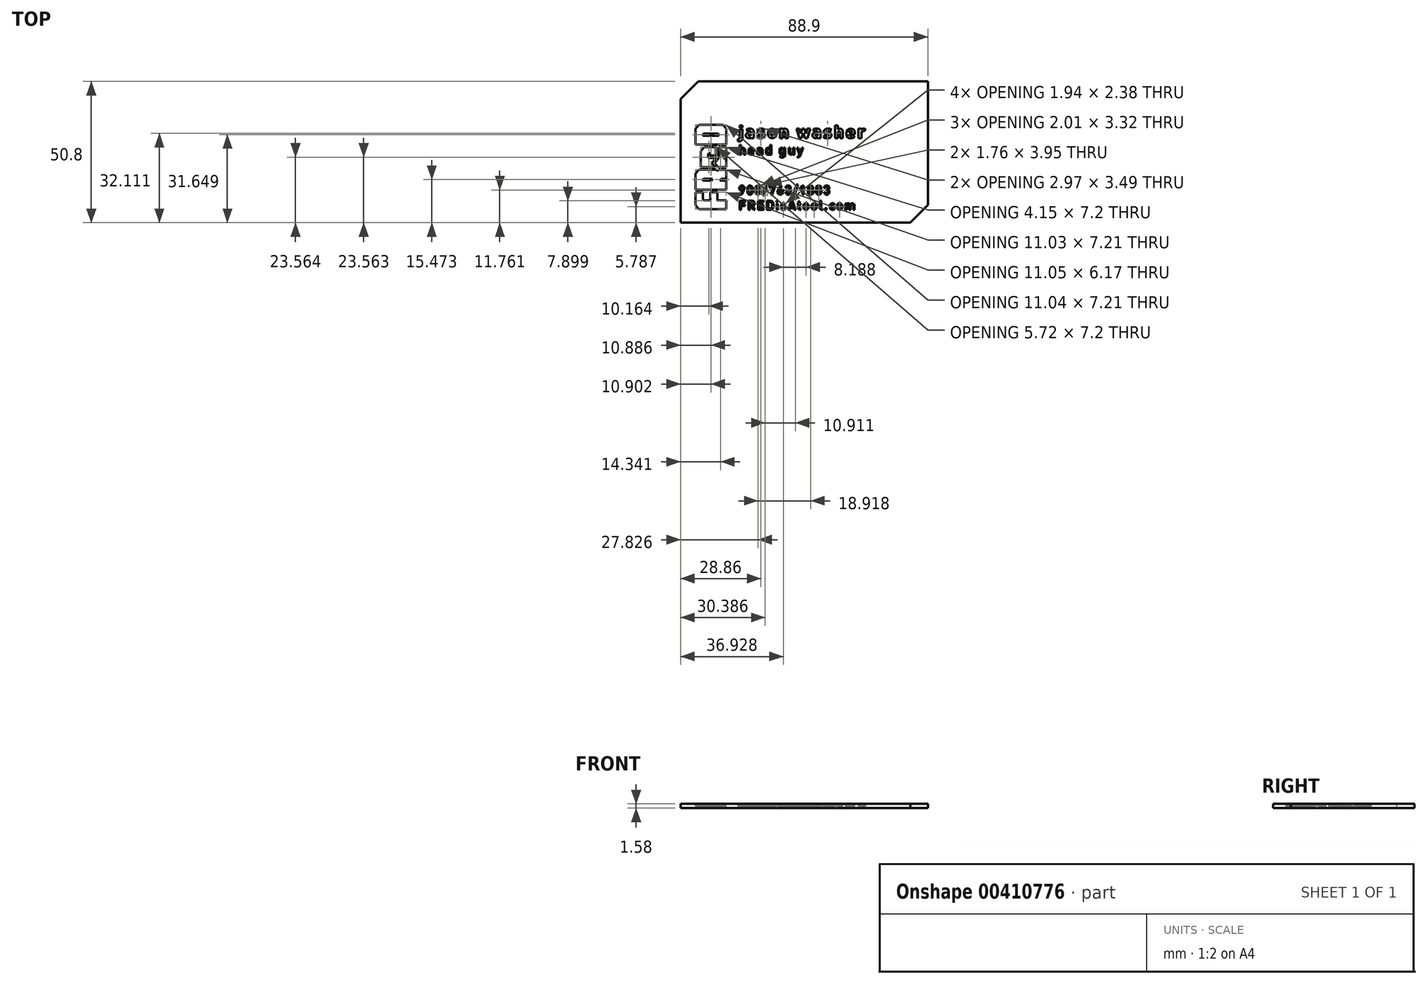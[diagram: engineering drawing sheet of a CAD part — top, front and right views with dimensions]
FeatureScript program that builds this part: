
annotation { "Feature Type Name" : "Feature", "Feature Type Description" : "" }
export const myFeature = defineFeature(function(context is Context, id is Id, definition is map)
    precondition{}
    {
        {
            var Q0;
            Q0=qCreatedBy(makeId("Top.planeOp"),FACE);
            var sketch = newSketch(context, id + "F0", { "sketchPlane" : qUnion([Q0])});
            skLineSegment(sketch, "E0", {"start": v(-19.03, 1.16) * mm, "end": v(-19.15, 1.16) * mm});
            skLineSegment(sketch, "E1", {"start": v(-19.15, 1.16) * mm, "end": v(-19.5, 0.9) * mm});
            skLineSegment(sketch, "E2", {"start": v(-19.5, 0.9) * mm, "end": v(-19.53, 0.84) * mm});
            skLineSegment(sketch, "E3", {"start": v(-19.53, 0.84) * mm, "end": v(-19.54, 0.82) * mm});
            skLineSegment(sketch, "E4", {"start": v(-19.54, 0.82) * mm, "end": v(-19.6, 0.54) * mm});
            skLineSegment(sketch, "E5", {"start": v(-19.6, 0.54) * mm, "end": v(-19.6, 0.5) * mm});
            skLineSegment(sketch, "E6", {"start": v(-19.6, 0.5) * mm, "end": v(-18.46, 0.5) * mm});
            skLineSegment(sketch, "E7", {"start": v(-18.46, 0.5) * mm, "end": v(-18.47, 0.54) * mm});
            skLineSegment(sketch, "E8", {"start": v(-18.47, 0.54) * mm, "end": v(-18.52, 0.82) * mm});
            skLineSegment(sketch, "E9", {"start": v(-18.52, 0.82) * mm, "end": v(-18.53, 0.84) * mm});
            skLineSegment(sketch, "E10", {"start": v(-18.53, 0.84) * mm, "end": v(-18.56, 0.9) * mm});
            skLineSegment(sketch, "E11", {"start": v(-18.56, 0.9) * mm, "end": v(-18.91, 1.16) * mm});
            skLineSegment(sketch, "E12", {"start": v(-18.91, 1.16) * mm, "end": v(-19.03, 1.16) * mm});
            skLineSegment(sketch, "E13", {"start": v(16.69, 7.6) * mm, "end": v(16.58, 7.6) * mm});
            skLineSegment(sketch, "E14", {"start": v(16.58, 7.6) * mm, "end": v(16.25, 7.37) * mm});
            skLineSegment(sketch, "E15", {"start": v(16.25, 7.37) * mm, "end": v(16.24, 7.33) * mm});
            skLineSegment(sketch, "E16", {"start": v(16.24, 7.33) * mm, "end": v(16.23, 7.31) * mm});
            skLineSegment(sketch, "E17", {"start": v(16.23, 7.31) * mm, "end": v(16.18, 7.13) * mm});
            skLineSegment(sketch, "E18", {"start": v(16.18, 7.13) * mm, "end": v(16.18, 7.07) * mm});
            skLineSegment(sketch, "E19", {"start": v(16.18, 7.07) * mm, "end": v(17.2, 7.07) * mm});
            skLineSegment(sketch, "E20", {"start": v(17.2, 7.07) * mm, "end": v(17.2, 7.13) * mm});
            skLineSegment(sketch, "E21", {"start": v(17.2, 7.13) * mm, "end": v(17.15, 7.31) * mm});
            skLineSegment(sketch, "E22", {"start": v(17.15, 7.31) * mm, "end": v(17.14, 7.33) * mm});
            skLineSegment(sketch, "E23", {"start": v(17.14, 7.33) * mm, "end": v(17.12, 7.37) * mm});
            skLineSegment(sketch, "E24", {"start": v(17.12, 7.37) * mm, "end": v(16.8, 7.6) * mm});
            skLineSegment(sketch, "E25", {"start": v(16.8, 7.6) * mm, "end": v(16.69, 7.6) * mm});
            skLineSegment(sketch, "E26", {"start": v(3.94, 6.1) * mm, "end": v(3.94, 6.05) * mm});
            skLineSegment(sketch, "E27", {"start": v(3.94, 6.05) * mm, "end": v(4.02, 5.9) * mm});
            skLineSegment(sketch, "E28", {"start": v(4.02, 5.9) * mm, "end": v(4.22, 5.82) * mm});
            skLineSegment(sketch, "E29", {"start": v(4.22, 5.82) * mm, "end": v(4.28, 5.82) * mm});
            skLineSegment(sketch, "E30", {"start": v(4.28, 5.82) * mm, "end": v(4.39, 5.82) * mm});
            skLineSegment(sketch, "E31", {"start": v(4.39, 5.82) * mm, "end": v(4.67, 5.92) * mm});
            skLineSegment(sketch, "E32", {"start": v(4.67, 5.92) * mm, "end": v(4.7, 5.94) * mm});
            skLineSegment(sketch, "E33", {"start": v(4.7, 5.94) * mm, "end": v(4.71, 5.96) * mm});
            skLineSegment(sketch, "E34", {"start": v(4.71, 5.96) * mm, "end": v(4.8, 6.2) * mm});
            skLineSegment(sketch, "E35", {"start": v(4.8, 6.2) * mm, "end": v(4.8, 6.29) * mm});
            skLineSegment(sketch, "E36", {"start": v(4.8, 6.29) * mm, "end": v(4.8, 6.37) * mm});
            skLineSegment(sketch, "E37", {"start": v(4.8, 6.37) * mm, "end": v(4.27, 6.37) * mm});
            skLineSegment(sketch, "E38", {"start": v(4.27, 6.37) * mm, "end": v(4.2, 6.37) * mm});
            skLineSegment(sketch, "E39", {"start": v(4.2, 6.37) * mm, "end": v(4.03, 6.3) * mm});
            skLineSegment(sketch, "E40", {"start": v(4.03, 6.3) * mm, "end": v(3.94, 6.15) * mm});
            skLineSegment(sketch, "E41", {"start": v(3.94, 6.15) * mm, "end": v(3.94, 6.1) * mm});
            skLineSegment(sketch, "E42", {"start": v(-12.79, -0.53) * mm, "end": v(-12.68, -0.53) * mm});
            skLineSegment(sketch, "E43", {"start": v(-12.68, -0.53) * mm, "end": v(-12.36, -0.28) * mm});
            skLineSegment(sketch, "E44", {"start": v(-12.36, -0.28) * mm, "end": v(-12.27, 0.16) * mm});
            skLineSegment(sketch, "E45", {"start": v(-12.27, 0.16) * mm, "end": v(-12.27, 0.3) * mm});
            skLineSegment(sketch, "E46", {"start": v(-12.27, 0.3) * mm, "end": v(-12.27, 0.45) * mm});
            skLineSegment(sketch, "E47", {"start": v(-12.27, 0.45) * mm, "end": v(-12.36, 0.88) * mm});
            skLineSegment(sketch, "E48", {"start": v(-12.36, 0.88) * mm, "end": v(-12.68, 1.13) * mm});
            skLineSegment(sketch, "E49", {"start": v(-12.68, 1.13) * mm, "end": v(-12.79, 1.13) * mm});
            skLineSegment(sketch, "E50", {"start": v(-12.79, 1.13) * mm, "end": v(-12.9, 1.13) * mm});
            skLineSegment(sketch, "E51", {"start": v(-12.9, 1.13) * mm, "end": v(-13.22, 0.88) * mm});
            skLineSegment(sketch, "E52", {"start": v(-13.22, 0.88) * mm, "end": v(-13.3, 0.45) * mm});
            skLineSegment(sketch, "E53", {"start": v(-13.3, 0.45) * mm, "end": v(-13.3, 0.3) * mm});
            skLineSegment(sketch, "E54", {"start": v(-13.3, 0.3) * mm, "end": v(-13.3, 0.16) * mm});
            skLineSegment(sketch, "E55", {"start": v(-13.3, 0.16) * mm, "end": v(-13.22, -0.28) * mm});
            skLineSegment(sketch, "E56", {"start": v(-13.22, -0.28) * mm, "end": v(-12.9, -0.53) * mm});
            skLineSegment(sketch, "E57", {"start": v(-12.9, -0.53) * mm, "end": v(-12.79, -0.53) * mm});
            skLineSegment(sketch, "E58", {"start": v(-38.1, 25.4) * mm, "end": v(-44.45, 19.05) * mm});
            skLineSegment(sketch, "E59", {"start": v(-44.45, 19.05) * mm, "end": v(-44.45, -25.4) * mm});
            skLineSegment(sketch, "E60", {"start": v(-44.45, -25.4) * mm, "end": v(38.1, -25.4) * mm});
            skLineSegment(sketch, "E61", {"start": v(38.1, -25.4) * mm, "end": v(44.45, -19.05) * mm});
            skLineSegment(sketch, "E62", {"start": v(44.45, -19.05) * mm, "end": v(44.45, 25.4) * mm});
            skLineSegment(sketch, "E63", {"start": v(44.45, 25.4) * mm, "end": v(-38.1, 25.4) * mm});
            skLineSegment(sketch, "E64", {"start": v(4.28, 7.58) * mm, "end": v(4.2, 7.58) * mm});
            skLineSegment(sketch, "E65", {"start": v(4.2, 7.58) * mm, "end": v(3.97, 7.53) * mm});
            skLineSegment(sketch, "E66", {"start": v(3.97, 7.53) * mm, "end": v(3.78, 7.4) * mm});
            skLineSegment(sketch, "E67", {"start": v(3.78, 7.4) * mm, "end": v(3.74, 7.35) * mm});
            skLineSegment(sketch, "E68", {"start": v(3.74, 7.35) * mm, "end": v(3.09, 8) * mm});
            skLineSegment(sketch, "E69", {"start": v(3.09, 8) * mm, "end": v(3.17, 8.09) * mm});
            skLineSegment(sketch, "E70", {"start": v(3.17, 8.09) * mm, "end": v(3.62, 8.36) * mm});
            skLineSegment(sketch, "E71", {"start": v(3.62, 8.36) * mm, "end": v(4.15, 8.46) * mm});
            skLineSegment(sketch, "E72", {"start": v(4.15, 8.46) * mm, "end": v(4.33, 8.46) * mm});
            skLineSegment(sketch, "E73", {"start": v(4.33, 8.46) * mm, "end": v(4.5, 8.46) * mm});
            skLineSegment(sketch, "E74", {"start": v(4.5, 8.46) * mm, "end": v(4.98, 8.38) * mm});
            skLineSegment(sketch, "E75", {"start": v(4.98, 8.38) * mm, "end": v(5.45, 8.15) * mm});
            skLineSegment(sketch, "E76", {"start": v(5.45, 8.15) * mm, "end": v(5.74, 7.76) * mm});
            skLineSegment(sketch, "E77", {"start": v(5.74, 7.76) * mm, "end": v(5.84, 7.35) * mm});
            skLineSegment(sketch, "E78", {"start": v(5.84, 7.35) * mm, "end": v(5.84, 7.22) * mm});
            skLineSegment(sketch, "E79", {"start": v(5.84, 7.22) * mm, "end": v(5.84, 5) * mm});
            skLineSegment(sketch, "E80", {"start": v(5.84, 5) * mm, "end": v(4.82, 5) * mm});
            skLineSegment(sketch, "E81", {"start": v(4.82, 5) * mm, "end": v(4.82, 5.28) * mm});
            skLineSegment(sketch, "E82", {"start": v(4.82, 5.28) * mm, "end": v(4.77, 5.23) * mm});
            skLineSegment(sketch, "E83", {"start": v(4.77, 5.23) * mm, "end": v(4.5, 5.05) * mm});
            skLineSegment(sketch, "E84", {"start": v(4.5, 5.05) * mm, "end": v(4.17, 4.97) * mm});
            skLineSegment(sketch, "E85", {"start": v(4.17, 4.97) * mm, "end": v(4.06, 4.97) * mm});
            skLineSegment(sketch, "E86", {"start": v(4.06, 4.97) * mm, "end": v(3.85, 4.97) * mm});
            skLineSegment(sketch, "E87", {"start": v(3.85, 4.97) * mm, "end": v(3.29, 5.23) * mm});
            skLineSegment(sketch, "E88", {"start": v(3.29, 5.23) * mm, "end": v(3.24, 5.28) * mm});
            skLineSegment(sketch, "E89", {"start": v(3.24, 5.28) * mm, "end": v(3.2, 5.32) * mm});
            skLineSegment(sketch, "E90", {"start": v(3.2, 5.32) * mm, "end": v(2.94, 5.89) * mm});
            skLineSegment(sketch, "E91", {"start": v(2.94, 5.89) * mm, "end": v(2.94, 6.08) * mm});
            skLineSegment(sketch, "E92", {"start": v(2.94, 6.08) * mm, "end": v(2.94, 6.17) * mm});
            skLineSegment(sketch, "E93", {"start": v(2.94, 6.17) * mm, "end": v(3, 6.45) * mm});
            skLineSegment(sketch, "E94", {"start": v(3, 6.45) * mm, "end": v(3.22, 6.76) * mm});
            skLineSegment(sketch, "E95", {"start": v(3.22, 6.76) * mm, "end": v(3.58, 6.99) * mm});
            skLineSegment(sketch, "E96", {"start": v(3.58, 6.99) * mm, "end": v(3.97, 7.07) * mm});
            skLineSegment(sketch, "E97", {"start": v(3.97, 7.07) * mm, "end": v(4.1, 7.07) * mm});
            skLineSegment(sketch, "E98", {"start": v(4.1, 7.07) * mm, "end": v(4.8, 7.07) * mm});
            skLineSegment(sketch, "E99", {"start": v(4.8, 7.07) * mm, "end": v(4.8, 7.15) * mm});
            skLineSegment(sketch, "E100", {"start": v(4.8, 7.15) * mm, "end": v(4.8, 7.24) * mm});
            skLineSegment(sketch, "E101", {"start": v(4.8, 7.24) * mm, "end": v(4.67, 7.49) * mm});
            skLineSegment(sketch, "E102", {"start": v(4.67, 7.49) * mm, "end": v(4.38, 7.58) * mm});
            skLineSegment(sketch, "E103", {"start": v(4.38, 7.58) * mm, "end": v(4.28, 7.58) * mm});
            skLineSegment(sketch, "E104", {"start": v(-1.72, 8.42) * mm, "end": v(-1.3, 6.65) * mm});
            skLineSegment(sketch, "E105", {"start": v(-1.3, 6.65) * mm, "end": v(-0.7, 8.42) * mm});
            skLineSegment(sketch, "E106", {"start": v(-0.7, 8.42) * mm, "end": v(0.02, 8.42) * mm});
            skLineSegment(sketch, "E107", {"start": v(0.02, 8.42) * mm, "end": v(0.61, 6.65) * mm});
            skLineSegment(sketch, "E108", {"start": v(0.61, 6.65) * mm, "end": v(1.04, 8.42) * mm});
            skLineSegment(sketch, "E109", {"start": v(1.04, 8.42) * mm, "end": v(2.14, 8.42) * mm});
            skLineSegment(sketch, "E110", {"start": v(2.14, 8.42) * mm, "end": v(1.1, 5) * mm});
            skLineSegment(sketch, "E111", {"start": v(1.1, 5) * mm, "end": v(0.28, 5) * mm});
            skLineSegment(sketch, "E112", {"start": v(0.28, 5) * mm, "end": v(-0.34, 6.88) * mm});
            skLineSegment(sketch, "E113", {"start": v(-0.34, 6.88) * mm, "end": v(-0.96, 5) * mm});
            skLineSegment(sketch, "E114", {"start": v(-0.96, 5) * mm, "end": v(-1.79, 5) * mm});
            skLineSegment(sketch, "E115", {"start": v(-1.79, 5) * mm, "end": v(-2.82, 8.42) * mm});
            skLineSegment(sketch, "E116", {"start": v(-2.82, 8.42) * mm, "end": v(-1.72, 8.42) * mm});
            skLineSegment(sketch, "E117", {"start": v(-2.4, -1.95) * mm, "end": v(-2.4, -1.5) * mm});
            skLineSegment(sketch, "E118", {"start": v(-2.4, -1.5) * mm, "end": v(-2.27, -1.5) * mm});
            skLineSegment(sketch, "E119", {"start": v(-2.27, -1.5) * mm, "end": v(-2.21, -1.5) * mm});
            skLineSegment(sketch, "E120", {"start": v(-2.21, -1.5) * mm, "end": v(-2.04, -1.43) * mm});
            skLineSegment(sketch, "E121", {"start": v(-2.04, -1.43) * mm, "end": v(-1.93, -1.27) * mm});
            skLineSegment(sketch, "E122", {"start": v(-1.93, -1.27) * mm, "end": v(-1.9, -1.23) * mm});
            skLineSegment(sketch, "E123", {"start": v(-1.9, -1.23) * mm, "end": v(-1.77, -0.84) * mm});
            skLineSegment(sketch, "E124", {"start": v(-1.77, -0.84) * mm, "end": v(-2.65, 1.55) * mm});
            skLineSegment(sketch, "E125", {"start": v(-2.65, 1.55) * mm, "end": v(-2.11, 1.55) * mm});
            skLineSegment(sketch, "E126", {"start": v(-2.11, 1.55) * mm, "end": v(-1.52, -0.21) * mm});
            skLineSegment(sketch, "E127", {"start": v(-1.52, -0.21) * mm, "end": v(-0.93, 1.55) * mm});
            skLineSegment(sketch, "E128", {"start": v(-0.93, 1.55) * mm, "end": v(-0.4, 1.55) * mm});
            skLineSegment(sketch, "E129", {"start": v(-0.4, 1.55) * mm, "end": v(-1.5, -1.45) * mm});
            skLineSegment(sketch, "E130", {"start": v(-1.5, -1.45) * mm, "end": v(-1.51, -1.49) * mm});
            skLineSegment(sketch, "E131", {"start": v(-1.51, -1.49) * mm, "end": v(-1.66, -1.74) * mm});
            skLineSegment(sketch, "E132", {"start": v(-1.66, -1.74) * mm, "end": v(-1.68, -1.76) * mm});
            skLineSegment(sketch, "E133", {"start": v(-1.68, -1.76) * mm, "end": v(-1.72, -1.8) * mm});
            skLineSegment(sketch, "E134", {"start": v(-1.72, -1.8) * mm, "end": v(-2.08, -1.95) * mm});
            skLineSegment(sketch, "E135", {"start": v(-2.08, -1.95) * mm, "end": v(-2.2, -1.95) * mm});
            skLineSegment(sketch, "E136", {"start": v(-2.2, -1.95) * mm, "end": v(-2.4, -1.95) * mm});
            skLineSegment(sketch, "E137", {"start": v(-2.27, -11.67) * mm, "end": v(-3.58, -15.61) * mm});
            skLineSegment(sketch, "E138", {"start": v(-3.58, -15.61) * mm, "end": v(-4.03, -15.61) * mm});
            skLineSegment(sketch, "E139", {"start": v(-4.03, -15.61) * mm, "end": v(-2.73, -11.67) * mm});
            skLineSegment(sketch, "E140", {"start": v(-2.73, -11.67) * mm, "end": v(-2.27, -11.67) * mm});
            skLineSegment(sketch, "E141", {"start": v(-5.6, 1.55) * mm, "end": v(-5.1, 1.55) * mm});
            skLineSegment(sketch, "E142", {"start": v(-5.1, 1.55) * mm, "end": v(-5.1, 0.02) * mm});
            skLineSegment(sketch, "E143", {"start": v(-5.1, 0.02) * mm, "end": v(-5.1, -0.08) * mm});
            skLineSegment(sketch, "E144", {"start": v(-5.1, -0.08) * mm, "end": v(-4.96, -0.4) * mm});
            skLineSegment(sketch, "E145", {"start": v(-4.96, -0.4) * mm, "end": v(-4.7, -0.53) * mm});
            skLineSegment(sketch, "E146", {"start": v(-4.7, -0.53) * mm, "end": v(-4.6, -0.53) * mm});
            skLineSegment(sketch, "E147", {"start": v(-4.6, -0.53) * mm, "end": v(-4.51, -0.53) * mm});
            skLineSegment(sketch, "E148", {"start": v(-4.51, -0.53) * mm, "end": v(-4.24, -0.4) * mm});
            skLineSegment(sketch, "E149", {"start": v(-4.24, -0.4) * mm, "end": v(-4.08, -0.08) * mm});
            skLineSegment(sketch, "E150", {"start": v(-4.08, -0.08) * mm, "end": v(-4.08, 0.02) * mm});
            skLineSegment(sketch, "E151", {"start": v(-4.08, 0.02) * mm, "end": v(-4.08, 1.55) * mm});
            skLineSegment(sketch, "E152", {"start": v(-4.08, 1.55) * mm, "end": v(-3.58, 1.55) * mm});
            skLineSegment(sketch, "E153", {"start": v(-3.58, 1.55) * mm, "end": v(-3.58, -0.95) * mm});
            skLineSegment(sketch, "E154", {"start": v(-3.58, -0.95) * mm, "end": v(-4.07, -0.95) * mm});
            skLineSegment(sketch, "E155", {"start": v(-4.07, -0.95) * mm, "end": v(-4.07, -0.7) * mm});
            skLineSegment(sketch, "E156", {"start": v(-4.07, -0.7) * mm, "end": v(-4.12, -0.75) * mm});
            skLineSegment(sketch, "E157", {"start": v(-4.12, -0.75) * mm, "end": v(-4.58, -0.98) * mm});
            skLineSegment(sketch, "E158", {"start": v(-4.58, -0.98) * mm, "end": v(-4.74, -0.98) * mm});
            skLineSegment(sketch, "E159", {"start": v(-4.74, -0.98) * mm, "end": v(-4.9, -0.98) * mm});
            skLineSegment(sketch, "E160", {"start": v(-4.9, -0.98) * mm, "end": v(-5.32, -0.8) * mm});
            skLineSegment(sketch, "E161", {"start": v(-5.32, -0.8) * mm, "end": v(-5.36, -0.76) * mm});
            skLineSegment(sketch, "E162", {"start": v(-5.36, -0.76) * mm, "end": v(-5.4, -0.7) * mm});
            skLineSegment(sketch, "E163", {"start": v(-5.4, -0.7) * mm, "end": v(-5.6, -0.21) * mm});
            skLineSegment(sketch, "E164", {"start": v(-5.6, -0.21) * mm, "end": v(-5.6, -0.05) * mm});
            skLineSegment(sketch, "E165", {"start": v(-5.6, -0.05) * mm, "end": v(-5.6, 1.55) * mm});
            skLineSegment(sketch, "E166", {"start": v(-8.78, 8.42) * mm, "end": v(-7.76, 8.42) * mm});
            skLineSegment(sketch, "E167", {"start": v(-7.76, 8.42) * mm, "end": v(-7.76, 8.14) * mm});
            skLineSegment(sketch, "E168", {"start": v(-7.76, 8.14) * mm, "end": v(-7.71, 8.2) * mm});
            skLineSegment(sketch, "E169", {"start": v(-7.71, 8.2) * mm, "end": v(-7.16, 8.46) * mm});
            skLineSegment(sketch, "E170", {"start": v(-7.16, 8.46) * mm, "end": v(-6.97, 8.46) * mm});
            skLineSegment(sketch, "E171", {"start": v(-6.97, 8.46) * mm, "end": v(-6.78, 8.46) * mm});
            skLineSegment(sketch, "E172", {"start": v(-6.78, 8.46) * mm, "end": v(-6.25, 8.21) * mm});
            skLineSegment(sketch, "E173", {"start": v(-6.25, 8.21) * mm, "end": v(-6.2, 8.17) * mm});
            skLineSegment(sketch, "E174", {"start": v(-6.2, 8.17) * mm, "end": v(-6.13, 8.1) * mm});
            skLineSegment(sketch, "E175", {"start": v(-6.13, 8.1) * mm, "end": v(-5.92, 7.7) * mm});
            skLineSegment(sketch, "E176", {"start": v(-5.92, 7.7) * mm, "end": v(-5.86, 7.32) * mm});
            skLineSegment(sketch, "E177", {"start": v(-5.86, 7.32) * mm, "end": v(-5.86, 7.19) * mm});
            skLineSegment(sketch, "E178", {"start": v(-5.86, 7.19) * mm, "end": v(-5.86, 5) * mm});
            skLineSegment(sketch, "E179", {"start": v(-5.86, 5) * mm, "end": v(-6.9, 5) * mm});
            skLineSegment(sketch, "E180", {"start": v(-6.9, 5) * mm, "end": v(-6.9, 7.05) * mm});
            skLineSegment(sketch, "E181", {"start": v(-6.9, 7.05) * mm, "end": v(-6.9, 7.14) * mm});
            skLineSegment(sketch, "E182", {"start": v(-6.9, 7.14) * mm, "end": v(-7.06, 7.43) * mm});
            skLineSegment(sketch, "E183", {"start": v(-7.06, 7.43) * mm, "end": v(-7.25, 7.52) * mm});
            skLineSegment(sketch, "E184", {"start": v(-7.25, 7.52) * mm, "end": v(-7.32, 7.52) * mm});
            skLineSegment(sketch, "E185", {"start": v(-7.32, 7.52) * mm, "end": v(-7.39, 7.52) * mm});
            skLineSegment(sketch, "E186", {"start": v(-7.39, 7.52) * mm, "end": v(-7.58, 7.43) * mm});
            skLineSegment(sketch, "E187", {"start": v(-7.58, 7.43) * mm, "end": v(-7.74, 7.14) * mm});
            skLineSegment(sketch, "E188", {"start": v(-7.74, 7.14) * mm, "end": v(-7.74, 7.05) * mm});
            skLineSegment(sketch, "E189", {"start": v(-7.74, 7.05) * mm, "end": v(-7.74, 5) * mm});
            skLineSegment(sketch, "E190", {"start": v(-7.74, 5) * mm, "end": v(-8.78, 5) * mm});
            skLineSegment(sketch, "E191", {"start": v(-8.78, 5) * mm, "end": v(-8.78, 8.42) * mm});
            skLineSegment(sketch, "E192", {"start": v(-8.63, 1.36) * mm, "end": v(-8.6, 1.4) * mm});
            skLineSegment(sketch, "E193", {"start": v(-8.6, 1.4) * mm, "end": v(-8.17, 1.58) * mm});
            skLineSegment(sketch, "E194", {"start": v(-8.17, 1.58) * mm, "end": v(-8.02, 1.58) * mm});
            skLineSegment(sketch, "E195", {"start": v(-8.02, 1.58) * mm, "end": v(-7.86, 1.58) * mm});
            skLineSegment(sketch, "E196", {"start": v(-7.86, 1.58) * mm, "end": v(-7.41, 1.34) * mm});
            skLineSegment(sketch, "E197", {"start": v(-7.41, 1.34) * mm, "end": v(-7.37, 1.29) * mm});
            skLineSegment(sketch, "E198", {"start": v(-7.37, 1.29) * mm, "end": v(-7.37, 1.55) * mm});
            skLineSegment(sketch, "E199", {"start": v(-7.37, 1.55) * mm, "end": v(-6.88, 1.55) * mm});
            skLineSegment(sketch, "E200", {"start": v(-6.88, 1.55) * mm, "end": v(-6.88, -0.94) * mm});
            skLineSegment(sketch, "E201", {"start": v(-6.88, -0.94) * mm, "end": v(-6.88, -1.13) * mm});
            skLineSegment(sketch, "E202", {"start": v(-6.88, -1.13) * mm, "end": v(-7.16, -1.7) * mm});
            skLineSegment(sketch, "E203", {"start": v(-7.16, -1.7) * mm, "end": v(-7.75, -2) * mm});
            skLineSegment(sketch, "E204", {"start": v(-7.75, -2) * mm, "end": v(-7.95, -2) * mm});
            skLineSegment(sketch, "E205", {"start": v(-7.95, -2) * mm, "end": v(-8.07, -2) * mm});
            skLineSegment(sketch, "E206", {"start": v(-8.07, -2) * mm, "end": v(-8.44, -1.92) * mm});
            skLineSegment(sketch, "E207", {"start": v(-8.44, -1.92) * mm, "end": v(-8.77, -1.73) * mm});
            skLineSegment(sketch, "E208", {"start": v(-8.77, -1.73) * mm, "end": v(-8.83, -1.66) * mm});
            skLineSegment(sketch, "E209", {"start": v(-8.83, -1.66) * mm, "end": v(-8.51, -1.34) * mm});
            skLineSegment(sketch, "E210", {"start": v(-8.51, -1.34) * mm, "end": v(-8.47, -1.38) * mm});
            skLineSegment(sketch, "E211", {"start": v(-8.47, -1.38) * mm, "end": v(-8.1, -1.57) * mm});
            skLineSegment(sketch, "E212", {"start": v(-8.1, -1.57) * mm, "end": v(-7.97, -1.57) * mm});
            skLineSegment(sketch, "E213", {"start": v(-7.97, -1.57) * mm, "end": v(-7.86, -1.57) * mm});
            skLineSegment(sketch, "E214", {"start": v(-7.86, -1.57) * mm, "end": v(-7.52, -1.37) * mm});
            skLineSegment(sketch, "E215", {"start": v(-7.52, -1.37) * mm, "end": v(-7.38, -1.04) * mm});
            skLineSegment(sketch, "E216", {"start": v(-7.38, -1.04) * mm, "end": v(-7.38, -0.93) * mm});
            skLineSegment(sketch, "E217", {"start": v(-7.38, -0.93) * mm, "end": v(-7.38, -0.6) * mm});
            skLineSegment(sketch, "E218", {"start": v(-7.38, -0.6) * mm, "end": v(-7.43, -0.66) * mm});
            skLineSegment(sketch, "E219", {"start": v(-7.43, -0.66) * mm, "end": v(-7.88, -0.9) * mm});
            skLineSegment(sketch, "E220", {"start": v(-7.88, -0.9) * mm, "end": v(-8.03, -0.9) * mm});
            skLineSegment(sketch, "E221", {"start": v(-8.03, -0.9) * mm, "end": v(-8.18, -0.9) * mm});
            skLineSegment(sketch, "E222", {"start": v(-8.18, -0.9) * mm, "end": v(-8.6, -0.7) * mm});
            skLineSegment(sketch, "E223", {"start": v(-8.6, -0.7) * mm, "end": v(-8.63, -0.67) * mm});
            skLineSegment(sketch, "E224", {"start": v(-8.63, -0.67) * mm, "end": v(-8.69, -0.61) * mm});
            skLineSegment(sketch, "E225", {"start": v(-8.69, -0.61) * mm, "end": v(-8.86, -0.23) * mm});
            skLineSegment(sketch, "E226", {"start": v(-8.86, -0.23) * mm, "end": v(-8.9, 0.2) * mm});
            skLineSegment(sketch, "E227", {"start": v(-8.9, 0.2) * mm, "end": v(-8.9, 0.35) * mm});
            skLineSegment(sketch, "E228", {"start": v(-8.9, 0.35) * mm, "end": v(-8.9, 0.5) * mm});
            skLineSegment(sketch, "E229", {"start": v(-8.9, 0.5) * mm, "end": v(-8.86, 0.92) * mm});
            skLineSegment(sketch, "E230", {"start": v(-8.86, 0.92) * mm, "end": v(-8.69, 1.3) * mm});
            skLineSegment(sketch, "E231", {"start": v(-8.69, 1.3) * mm, "end": v(-8.63, 1.36) * mm});
            skLineSegment(sketch, "E232", {"start": v(-13.53, 1.36) * mm, "end": v(-13.5, 1.4) * mm});
            skLineSegment(sketch, "E233", {"start": v(-13.5, 1.4) * mm, "end": v(-13.07, 1.58) * mm});
            skLineSegment(sketch, "E234", {"start": v(-13.07, 1.58) * mm, "end": v(-12.92, 1.58) * mm});
            skLineSegment(sketch, "E235", {"start": v(-12.92, 1.58) * mm, "end": v(-12.76, 1.58) * mm});
            skLineSegment(sketch, "E236", {"start": v(-12.76, 1.58) * mm, "end": v(-12.31, 1.35) * mm});
            skLineSegment(sketch, "E237", {"start": v(-12.31, 1.35) * mm, "end": v(-12.27, 1.3) * mm});
            skLineSegment(sketch, "E238", {"start": v(-12.27, 1.3) * mm, "end": v(-12.27, 2.56) * mm});
            skLineSegment(sketch, "E239", {"start": v(-12.27, 2.56) * mm, "end": v(-11.76, 2.56) * mm});
            skLineSegment(sketch, "E240", {"start": v(-11.76, 2.56) * mm, "end": v(-11.76, -0.95) * mm});
            skLineSegment(sketch, "E241", {"start": v(-11.76, -0.95) * mm, "end": v(-12.26, -0.95) * mm});
            skLineSegment(sketch, "E242", {"start": v(-12.26, -0.95) * mm, "end": v(-12.26, -0.69) * mm});
            skLineSegment(sketch, "E243", {"start": v(-12.26, -0.69) * mm, "end": v(-12.3, -0.74) * mm});
            skLineSegment(sketch, "E244", {"start": v(-12.3, -0.74) * mm, "end": v(-12.77, -0.98) * mm});
            skLineSegment(sketch, "E245", {"start": v(-12.77, -0.98) * mm, "end": v(-12.92, -0.98) * mm});
            skLineSegment(sketch, "E246", {"start": v(-12.92, -0.98) * mm, "end": v(-13.07, -0.98) * mm});
            skLineSegment(sketch, "E247", {"start": v(-13.07, -0.98) * mm, "end": v(-13.5, -0.8) * mm});
            skLineSegment(sketch, "E248", {"start": v(-13.5, -0.8) * mm, "end": v(-13.53, -0.76) * mm});
            skLineSegment(sketch, "E249", {"start": v(-13.53, -0.76) * mm, "end": v(-13.6, -0.7) * mm});
            skLineSegment(sketch, "E250", {"start": v(-13.6, -0.7) * mm, "end": v(-13.77, -0.28) * mm});
            skLineSegment(sketch, "E251", {"start": v(-13.77, -0.28) * mm, "end": v(-13.81, 0.16) * mm});
            skLineSegment(sketch, "E252", {"start": v(-13.81, 0.16) * mm, "end": v(-13.81, 0.3) * mm});
            skLineSegment(sketch, "E253", {"start": v(-13.81, 0.3) * mm, "end": v(-13.81, 0.45) * mm});
            skLineSegment(sketch, "E254", {"start": v(-13.81, 0.45) * mm, "end": v(-13.77, 0.88) * mm});
            skLineSegment(sketch, "E255", {"start": v(-13.77, 0.88) * mm, "end": v(-13.6, 1.3) * mm});
            skLineSegment(sketch, "E256", {"start": v(-13.6, 1.3) * mm, "end": v(-13.53, 1.36) * mm});
            skLineSegment(sketch, "E257", {"start": v(-15.37, 6.29) * mm, "end": v(-15.9, 6.34) * mm});
            skLineSegment(sketch, "E258", {"start": v(-15.9, 6.34) * mm, "end": v(-16.05, 6.35) * mm});
            skLineSegment(sketch, "E259", {"start": v(-16.05, 6.35) * mm, "end": v(-16.62, 6.6) * mm});
            skLineSegment(sketch, "E260", {"start": v(-16.62, 6.6) * mm, "end": v(-16.89, 7.15) * mm});
            skLineSegment(sketch, "E261", {"start": v(-16.89, 7.15) * mm, "end": v(-16.89, 7.33) * mm});
            skLineSegment(sketch, "E262", {"start": v(-16.89, 7.33) * mm, "end": v(-16.89, 7.45) * mm});
            skLineSegment(sketch, "E263", {"start": v(-16.89, 7.45) * mm, "end": v(-16.77, 7.82) * mm});
            skLineSegment(sketch, "E264", {"start": v(-16.77, 7.82) * mm, "end": v(-16.46, 8.18) * mm});
            skLineSegment(sketch, "E265", {"start": v(-16.46, 8.18) * mm, "end": v(-16.03, 8.39) * mm});
            skLineSegment(sketch, "E266", {"start": v(-16.03, 8.39) * mm, "end": v(-15.66, 8.46) * mm});
            skLineSegment(sketch, "E267", {"start": v(-15.66, 8.46) * mm, "end": v(-15.53, 8.46) * mm});
            skLineSegment(sketch, "E268", {"start": v(-15.53, 8.46) * mm, "end": v(-15.34, 8.46) * mm});
            skLineSegment(sketch, "E269", {"start": v(-15.34, 8.46) * mm, "end": v(-14.77, 8.37) * mm});
            skLineSegment(sketch, "E270", {"start": v(-14.77, 8.37) * mm, "end": v(-14.27, 8.12) * mm});
            skLineSegment(sketch, "E271", {"start": v(-14.27, 8.12) * mm, "end": v(-14.18, 8.04) * mm});
            skLineSegment(sketch, "E272", {"start": v(-14.18, 8.04) * mm, "end": v(-14.82, 7.4) * mm});
            skLineSegment(sketch, "E273", {"start": v(-14.82, 7.4) * mm, "end": v(-14.87, 7.44) * mm});
            skLineSegment(sketch, "E274", {"start": v(-14.87, 7.44) * mm, "end": v(-15.15, 7.56) * mm});
            skLineSegment(sketch, "E275", {"start": v(-15.15, 7.56) * mm, "end": v(-15.45, 7.6) * mm});
            skLineSegment(sketch, "E276", {"start": v(-15.45, 7.6) * mm, "end": v(-15.55, 7.6) * mm});
            skLineSegment(sketch, "E277", {"start": v(-15.55, 7.6) * mm, "end": v(-15.61, 7.6) * mm});
            skLineSegment(sketch, "E278", {"start": v(-15.61, 7.6) * mm, "end": v(-15.81, 7.53) * mm});
            skLineSegment(sketch, "E279", {"start": v(-15.81, 7.53) * mm, "end": v(-15.89, 7.44) * mm});
            skLineSegment(sketch, "E280", {"start": v(-15.89, 7.44) * mm, "end": v(-15.89, 7.4) * mm});
            skLineSegment(sketch, "E281", {"start": v(-15.89, 7.4) * mm, "end": v(-15.89, 7.38) * mm});
            skLineSegment(sketch, "E282", {"start": v(-15.89, 7.38) * mm, "end": v(-15.86, 7.3) * mm});
            skLineSegment(sketch, "E283", {"start": v(-15.86, 7.3) * mm, "end": v(-15.72, 7.22) * mm});
            skLineSegment(sketch, "E284", {"start": v(-15.72, 7.22) * mm, "end": v(-15.66, 7.21) * mm});
            skLineSegment(sketch, "E285", {"start": v(-15.66, 7.21) * mm, "end": v(-15.14, 7.16) * mm});
            skLineSegment(sketch, "E286", {"start": v(-15.14, 7.16) * mm, "end": v(-14.96, 7.15) * mm});
            skLineSegment(sketch, "E287", {"start": v(-14.96, 7.15) * mm, "end": v(-14.35, 6.82) * mm});
            skLineSegment(sketch, "E288", {"start": v(-14.35, 6.82) * mm, "end": v(-14.1, 6.3) * mm});
            skLineSegment(sketch, "E289", {"start": v(-14.1, 6.3) * mm, "end": v(-14.1, 6.12) * mm});
            skLineSegment(sketch, "E290", {"start": v(-14.1, 6.12) * mm, "end": v(-14.1, 6) * mm});
            skLineSegment(sketch, "E291", {"start": v(-14.1, 6) * mm, "end": v(-14.23, 5.6) * mm});
            skLineSegment(sketch, "E292", {"start": v(-14.23, 5.6) * mm, "end": v(-14.55, 5.24) * mm});
            skLineSegment(sketch, "E293", {"start": v(-14.55, 5.24) * mm, "end": v(-15.02, 5.03) * mm});
            skLineSegment(sketch, "E294", {"start": v(-15.02, 5.03) * mm, "end": v(-15.45, 4.96) * mm});
            skLineSegment(sketch, "E295", {"start": v(-15.45, 4.96) * mm, "end": v(-15.59, 4.96) * mm});
            skLineSegment(sketch, "E296", {"start": v(-15.59, 4.96) * mm, "end": v(-15.78, 4.96) * mm});
            skLineSegment(sketch, "E297", {"start": v(-15.78, 4.96) * mm, "end": v(-16.35, 5.04) * mm});
            skLineSegment(sketch, "E298", {"start": v(-16.35, 5.04) * mm, "end": v(-16.96, 5.34) * mm});
            skLineSegment(sketch, "E299", {"start": v(-16.96, 5.34) * mm, "end": v(-17.07, 5.46) * mm});
            skLineSegment(sketch, "E300", {"start": v(-17.07, 5.46) * mm, "end": v(-16.4, 6.13) * mm});
            skLineSegment(sketch, "E301", {"start": v(-16.4, 6.13) * mm, "end": v(-16.33, 6.06) * mm});
            skLineSegment(sketch, "E302", {"start": v(-16.33, 6.06) * mm, "end": v(-15.94, 5.88) * mm});
            skLineSegment(sketch, "E303", {"start": v(-15.94, 5.88) * mm, "end": v(-15.66, 5.85) * mm});
            skLineSegment(sketch, "E304", {"start": v(-15.66, 5.85) * mm, "end": v(-15.57, 5.85) * mm});
            skLineSegment(sketch, "E305", {"start": v(-15.57, 5.85) * mm, "end": v(-15.5, 5.85) * mm});
            skLineSegment(sketch, "E306", {"start": v(-15.5, 5.85) * mm, "end": v(-15.29, 5.9) * mm});
            skLineSegment(sketch, "E307", {"start": v(-15.29, 5.9) * mm, "end": v(-15.12, 6.02) * mm});
            skLineSegment(sketch, "E308", {"start": v(-15.12, 6.02) * mm, "end": v(-15.12, 6.07) * mm});
            skLineSegment(sketch, "E309", {"start": v(-15.12, 6.07) * mm, "end": v(-15.12, 6.1) * mm});
            skLineSegment(sketch, "E310", {"start": v(-15.12, 6.1) * mm, "end": v(-15.17, 6.2) * mm});
            skLineSegment(sketch, "E311", {"start": v(-15.17, 6.2) * mm, "end": v(-15.32, 6.28) * mm});
            skLineSegment(sketch, "E312", {"start": v(-15.32, 6.28) * mm, "end": v(-15.37, 6.29) * mm});
            skLineSegment(sketch, "E313", {"start": v(-16.12, -0.98) * mm, "end": v(-16.3, -0.98) * mm});
            skLineSegment(sketch, "E314", {"start": v(-16.3, -0.98) * mm, "end": v(-16.76, -0.8) * mm});
            skLineSegment(sketch, "E315", {"start": v(-16.76, -0.8) * mm, "end": v(-16.8, -0.76) * mm});
            skLineSegment(sketch, "E316", {"start": v(-16.8, -0.76) * mm, "end": v(-16.83, -0.72) * mm});
            skLineSegment(sketch, "E317", {"start": v(-16.83, -0.72) * mm, "end": v(-17, -0.34) * mm});
            skLineSegment(sketch, "E318", {"start": v(-17, -0.34) * mm, "end": v(-17, -0.22) * mm});
            skLineSegment(sketch, "E319", {"start": v(-17, -0.22) * mm, "end": v(-17, -0.09) * mm});
            skLineSegment(sketch, "E320", {"start": v(-17, -0.09) * mm, "end": v(-16.78, 0.3) * mm});
            skLineSegment(sketch, "E321", {"start": v(-16.78, 0.3) * mm, "end": v(-16.3, 0.5) * mm});
            skLineSegment(sketch, "E322", {"start": v(-16.3, 0.5) * mm, "end": v(-16.13, 0.5) * mm});
            skLineSegment(sketch, "E323", {"start": v(-16.13, 0.5) * mm, "end": v(-15.47, 0.5) * mm});
            skLineSegment(sketch, "E324", {"start": v(-15.47, 0.5) * mm, "end": v(-15.47, 0.68) * mm});
            skLineSegment(sketch, "E325", {"start": v(-15.47, 0.68) * mm, "end": v(-15.47, 0.77) * mm});
            skLineSegment(sketch, "E326", {"start": v(-15.47, 0.77) * mm, "end": v(-15.6, 1.04) * mm});
            skLineSegment(sketch, "E327", {"start": v(-15.6, 1.04) * mm, "end": v(-15.91, 1.15) * mm});
            skLineSegment(sketch, "E328", {"start": v(-15.91, 1.15) * mm, "end": v(-16.02, 1.15) * mm});
            skLineSegment(sketch, "E329", {"start": v(-16.02, 1.15) * mm, "end": v(-16.1, 1.15) * mm});
            skLineSegment(sketch, "E330", {"start": v(-16.1, 1.15) * mm, "end": v(-16.34, 1.1) * mm});
            skLineSegment(sketch, "E331", {"start": v(-16.34, 1.1) * mm, "end": v(-16.53, 0.95) * mm});
            skLineSegment(sketch, "E332", {"start": v(-16.53, 0.95) * mm, "end": v(-16.56, 0.9) * mm});
            skLineSegment(sketch, "E333", {"start": v(-16.56, 0.9) * mm, "end": v(-16.9, 1.22) * mm});
            skLineSegment(sketch, "E334", {"start": v(-16.9, 1.22) * mm, "end": v(-16.84, 1.3) * mm});
            skLineSegment(sketch, "E335", {"start": v(-16.84, 1.3) * mm, "end": v(-16.51, 1.5) * mm});
            skLineSegment(sketch, "E336", {"start": v(-16.51, 1.5) * mm, "end": v(-16.13, 1.58) * mm});
            skLineSegment(sketch, "E337", {"start": v(-16.13, 1.58) * mm, "end": v(-16, 1.58) * mm});
            skLineSegment(sketch, "E338", {"start": v(-16, 1.58) * mm, "end": v(-15.8, 1.58) * mm});
            skLineSegment(sketch, "E339", {"start": v(-15.8, 1.58) * mm, "end": v(-15.22, 1.37) * mm});
            skLineSegment(sketch, "E340", {"start": v(-15.22, 1.37) * mm, "end": v(-14.96, 0.88) * mm});
            skLineSegment(sketch, "E341", {"start": v(-14.96, 0.88) * mm, "end": v(-14.96, 0.72) * mm});
            skLineSegment(sketch, "E342", {"start": v(-14.96, 0.72) * mm, "end": v(-14.96, -0.95) * mm});
            skLineSegment(sketch, "E343", {"start": v(-14.96, -0.95) * mm, "end": v(-15.46, -0.95) * mm});
            skLineSegment(sketch, "E344", {"start": v(-15.46, -0.95) * mm, "end": v(-15.46, -0.73) * mm});
            skLineSegment(sketch, "E345", {"start": v(-15.46, -0.73) * mm, "end": v(-15.5, -0.77) * mm});
            skLineSegment(sketch, "E346", {"start": v(-15.5, -0.77) * mm, "end": v(-15.74, -0.92) * mm});
            skLineSegment(sketch, "E347", {"start": v(-15.74, -0.92) * mm, "end": v(-16.03, -0.98) * mm});
            skLineSegment(sketch, "E348", {"start": v(-16.03, -0.98) * mm, "end": v(-16.12, -0.98) * mm});
            skLineSegment(sketch, "E349", {"start": v(-18.95, -0.55) * mm, "end": v(-18.8, -0.55) * mm});
            skLineSegment(sketch, "E350", {"start": v(-18.8, -0.55) * mm, "end": v(-18.4, -0.33) * mm});
            skLineSegment(sketch, "E351", {"start": v(-18.4, -0.33) * mm, "end": v(-18.35, -0.3) * mm});
            skLineSegment(sketch, "E352", {"start": v(-18.35, -0.3) * mm, "end": v(-18.02, -0.6) * mm});
            skLineSegment(sketch, "E353", {"start": v(-18.02, -0.6) * mm, "end": v(-18.09, -0.66) * mm});
            skLineSegment(sketch, "E354", {"start": v(-18.09, -0.66) * mm, "end": v(-18.43, -0.88) * mm});
            skLineSegment(sketch, "E355", {"start": v(-18.43, -0.88) * mm, "end": v(-18.83, -0.98) * mm});
            skLineSegment(sketch, "E356", {"start": v(-18.83, -0.98) * mm, "end": v(-18.96, -0.98) * mm});
            skLineSegment(sketch, "E357", {"start": v(-18.96, -0.98) * mm, "end": v(-19.07, -0.98) * mm});
            skLineSegment(sketch, "E358", {"start": v(-19.07, -0.98) * mm, "end": v(-19.4, -0.91) * mm});
            skLineSegment(sketch, "E359", {"start": v(-19.4, -0.91) * mm, "end": v(-19.76, -0.7) * mm});
            skLineSegment(sketch, "E360", {"start": v(-19.76, -0.7) * mm, "end": v(-20, -0.3) * mm});
            skLineSegment(sketch, "E361", {"start": v(-20, -0.3) * mm, "end": v(-20.1, 0.15) * mm});
            skLineSegment(sketch, "E362", {"start": v(-20.1, 0.15) * mm, "end": v(-20.1, 0.3) * mm});
            skLineSegment(sketch, "E363", {"start": v(-20.1, 0.3) * mm, "end": v(-20.1, 0.54) * mm});
            skLineSegment(sketch, "E364", {"start": v(-20.1, 0.54) * mm, "end": v(-19.8, 1.25) * mm});
            skLineSegment(sketch, "E365", {"start": v(-19.8, 1.25) * mm, "end": v(-19.22, 1.58) * mm});
            skLineSegment(sketch, "E366", {"start": v(-19.22, 1.58) * mm, "end": v(-19.03, 1.58) * mm});
            skLineSegment(sketch, "E367", {"start": v(-19.03, 1.58) * mm, "end": v(-18.83, 1.58) * mm});
            skLineSegment(sketch, "E368", {"start": v(-18.83, 1.58) * mm, "end": v(-18.25, 1.25) * mm});
            skLineSegment(sketch, "E369", {"start": v(-18.25, 1.25) * mm, "end": v(-17.97, 0.6) * mm});
            skLineSegment(sketch, "E370", {"start": v(-17.97, 0.6) * mm, "end": v(-17.97, 0.38) * mm});
            skLineSegment(sketch, "E371", {"start": v(-17.97, 0.38) * mm, "end": v(-17.97, 0.15) * mm});
            skLineSegment(sketch, "E372", {"start": v(-17.97, 0.15) * mm, "end": v(-19.6, 0.15) * mm});
            skLineSegment(sketch, "E373", {"start": v(-19.6, 0.15) * mm, "end": v(-19.6, 0.03) * mm});
            skLineSegment(sketch, "E374", {"start": v(-19.6, 0.03) * mm, "end": v(-19.43, -0.36) * mm});
            skLineSegment(sketch, "E375", {"start": v(-19.43, -0.36) * mm, "end": v(-19.07, -0.55) * mm});
            skLineSegment(sketch, "E376", {"start": v(-19.07, -0.55) * mm, "end": v(-18.95, -0.55) * mm});
            skLineSegment(sketch, "E377", {"start": v(-21.23, 0.66) * mm, "end": v(-21.23, -0.95) * mm});
            skLineSegment(sketch, "E378", {"start": v(-21.23, -0.95) * mm, "end": v(-21.73, -0.95) * mm});
            skLineSegment(sketch, "E379", {"start": v(-21.73, -0.95) * mm, "end": v(-21.73, 0.58) * mm});
            skLineSegment(sketch, "E380", {"start": v(-21.73, 0.58) * mm, "end": v(-21.73, 0.69) * mm});
            skLineSegment(sketch, "E381", {"start": v(-21.73, 0.69) * mm, "end": v(-21.88, 1) * mm});
            skLineSegment(sketch, "E382", {"start": v(-21.88, 1) * mm, "end": v(-22.15, 1.13) * mm});
            skLineSegment(sketch, "E383", {"start": v(-22.15, 1.13) * mm, "end": v(-22.24, 1.13) * mm});
            skLineSegment(sketch, "E384", {"start": v(-22.24, 1.13) * mm, "end": v(-22.33, 1.13) * mm});
            skLineSegment(sketch, "E385", {"start": v(-22.33, 1.13) * mm, "end": v(-22.6, 1) * mm});
            skLineSegment(sketch, "E386", {"start": v(-22.6, 1) * mm, "end": v(-22.75, 0.69) * mm});
            skLineSegment(sketch, "E387", {"start": v(-22.75, 0.69) * mm, "end": v(-22.75, 0.58) * mm});
            skLineSegment(sketch, "E388", {"start": v(-22.75, 0.58) * mm, "end": v(-22.75, -0.95) * mm});
            skLineSegment(sketch, "E389", {"start": v(-22.75, -0.95) * mm, "end": v(-23.25, -0.95) * mm});
            skLineSegment(sketch, "E390", {"start": v(-23.25, -0.95) * mm, "end": v(-23.25, 2.56) * mm});
            skLineSegment(sketch, "E391", {"start": v(-23.25, 2.56) * mm, "end": v(-22.75, 2.56) * mm});
            skLineSegment(sketch, "E392", {"start": v(-22.75, 2.56) * mm, "end": v(-22.75, 1.3) * mm});
            skLineSegment(sketch, "E393", {"start": v(-22.75, 1.3) * mm, "end": v(-22.7, 1.35) * mm});
            skLineSegment(sketch, "E394", {"start": v(-22.7, 1.35) * mm, "end": v(-22.25, 1.58) * mm});
            skLineSegment(sketch, "E395", {"start": v(-22.25, 1.58) * mm, "end": v(-22.1, 1.58) * mm});
            skLineSegment(sketch, "E396", {"start": v(-22.1, 1.58) * mm, "end": v(-21.94, 1.58) * mm});
            skLineSegment(sketch, "E397", {"start": v(-21.94, 1.58) * mm, "end": v(-21.46, 1.33) * mm});
            skLineSegment(sketch, "E398", {"start": v(-21.46, 1.33) * mm, "end": v(-21.23, 0.83) * mm});
            skLineSegment(sketch, "E399", {"start": v(-21.23, 0.83) * mm, "end": v(-21.23, 0.66) * mm});
            skLineSegment(sketch, "E400", {"start": v(-23.25, 9.56) * mm, "end": v(-22.2, 9.56) * mm});
            skLineSegment(sketch, "E401", {"start": v(-22.2, 9.56) * mm, "end": v(-22.2, 8.77) * mm});
            skLineSegment(sketch, "E402", {"start": v(-22.2, 8.77) * mm, "end": v(-23.25, 8.77) * mm});
            skLineSegment(sketch, "E403", {"start": v(-23.25, 8.77) * mm, "end": v(-23.25, 9.56) * mm});
            skLineSegment(sketch, "E404", {"start": v(-28.03, -2.18) * mm, "end": v(-28.03, -5.44) * mm});
            skLineSegment(sketch, "E405", {"start": v(-28.03, -5.44) * mm, "end": v(-31, -5.44) * mm});
            skLineSegment(sketch, "E406", {"start": v(-31, -5.44) * mm, "end": v(-32.19, -4) * mm});
            skLineSegment(sketch, "E407", {"start": v(-32.19, -4) * mm, "end": v(-30.7, -2.18) * mm});
            skLineSegment(sketch, "E408", {"start": v(-30.7, -2.18) * mm, "end": v(-30.7, -2.18) * mm});
            skLineSegment(sketch, "E409", {"start": v(-30.7, -2.18) * mm, "end": v(-30.7, 1.77) * mm});
            skLineSegment(sketch, "E410", {"start": v(-30.7, 1.77) * mm, "end": v(-28.04, 1.77) * mm});
            skLineSegment(sketch, "E411", {"start": v(-28.04, 1.77) * mm, "end": v(-28.04, -2.18) * mm});
            skLineSegment(sketch, "E412", {"start": v(-28.04, -2.18) * mm, "end": v(-28.03, -2.18) * mm});
            skLineSegment(sketch, "E413", {"start": v(-28.03, -10.28) * mm, "end": v(-28.03, -13.53) * mm});
            skLineSegment(sketch, "E414", {"start": v(-28.03, -13.53) * mm, "end": v(-39.06, -13.53) * mm});
            skLineSegment(sketch, "E415", {"start": v(-39.06, -13.53) * mm, "end": v(-39.06, -7.76) * mm});
            skLineSegment(sketch, "E416", {"start": v(-39.06, -7.76) * mm, "end": v(-37.88, -6.32) * mm});
            skLineSegment(sketch, "E417", {"start": v(-37.88, -6.32) * mm, "end": v(-31.61, -6.32) * mm});
            skLineSegment(sketch, "E418", {"start": v(-31.61, -6.32) * mm, "end": v(-31.16, -6.87) * mm});
            skLineSegment(sketch, "E419", {"start": v(-31.16, -6.87) * mm, "end": v(-30.72, -6.32) * mm});
            skLineSegment(sketch, "E420", {"start": v(-30.72, -6.32) * mm, "end": v(-28.03, -6.32) * mm});
            skLineSegment(sketch, "E421", {"start": v(-28.03, -6.32) * mm, "end": v(-28.03, -9.57) * mm});
            skLineSegment(sketch, "E422", {"start": v(-28.03, -9.57) * mm, "end": v(-29.8, -9.57) * mm});
            skLineSegment(sketch, "E423", {"start": v(-29.8, -9.57) * mm, "end": v(-30.3, -10.28) * mm});
            skLineSegment(sketch, "E424", {"start": v(-30.3, -10.28) * mm, "end": v(-28.03, -10.28) * mm});
            skLineSegment(sketch, "E425", {"start": v(-34.2, -0.4) * mm, "end": v(-34.57, -0.87) * mm});
            skLineSegment(sketch, "E426", {"start": v(-34.57, -0.87) * mm, "end": v(-34.57, -2.17) * mm});
            skLineSegment(sketch, "E427", {"start": v(-34.57, -2.17) * mm, "end": v(-31.72, -2.18) * mm});
            skLineSegment(sketch, "E428", {"start": v(-31.72, -2.18) * mm, "end": v(-33.2, -4) * mm});
            skLineSegment(sketch, "E429", {"start": v(-33.2, -4) * mm, "end": v(-32.02, -5.44) * mm});
            skLineSegment(sketch, "E430", {"start": v(-32.02, -5.44) * mm, "end": v(-37.15, -5.44) * mm});
            skLineSegment(sketch, "E431", {"start": v(-37.15, -5.44) * mm, "end": v(-37.15, 0.34) * mm});
            skLineSegment(sketch, "E432", {"start": v(-37.15, 0.34) * mm, "end": v(-35.95, 1.76) * mm});
            skLineSegment(sketch, "E433", {"start": v(-35.95, 1.76) * mm, "end": v(-31.43, 1.76) * mm});
            skLineSegment(sketch, "E434", {"start": v(-31.43, 1.76) * mm, "end": v(-31.43, -1.29) * mm});
            skLineSegment(sketch, "E435", {"start": v(-31.43, -1.29) * mm, "end": v(-33.85, -1.29) * mm});
            skLineSegment(sketch, "E436", {"start": v(-33.85, -1.29) * mm, "end": v(-33.85, -1.29) * mm});
            skLineSegment(sketch, "E437", {"start": v(-33.85, -1.29) * mm, "end": v(-33.84, -1.29) * mm});
            skLineSegment(sketch, "E438", {"start": v(-33.84, -1.29) * mm, "end": v(-33.84, -0.4) * mm});
            skLineSegment(sketch, "E439", {"start": v(-33.84, -0.4) * mm, "end": v(-34.2, -0.4) * mm});
            skLineSegment(sketch, "E440", {"start": v(-39.08, 8.4) * mm, "end": v(-37.87, 9.85) * mm});
            skLineSegment(sketch, "E441", {"start": v(-37.87, 9.85) * mm, "end": v(-29.21, 9.85) * mm});
            skLineSegment(sketch, "E442", {"start": v(-29.21, 9.85) * mm, "end": v(-28.04, 8.4) * mm});
            skLineSegment(sketch, "E443", {"start": v(-28.04, 8.4) * mm, "end": v(-28.05, 2.65) * mm});
            skLineSegment(sketch, "E444", {"start": v(-28.05, 2.65) * mm, "end": v(-39.08, 2.65) * mm});
            skLineSegment(sketch, "E445", {"start": v(-39.08, 2.65) * mm, "end": v(-39.08, 8.4) * mm});
            skLineSegment(sketch, "E446", {"start": v(-28.01, -20.59) * mm, "end": v(-37.88, -20.59) * mm});
            skLineSegment(sketch, "E447", {"start": v(-37.88, -20.59) * mm, "end": v(-37.88, -20.57) * mm});
            skLineSegment(sketch, "E448", {"start": v(-37.88, -20.57) * mm, "end": v(-37.88, -20.58) * mm});
            skLineSegment(sketch, "E449", {"start": v(-37.88, -20.58) * mm, "end": v(-39.06, -19.13) * mm});
            skLineSegment(sketch, "E450", {"start": v(-39.06, -19.13) * mm, "end": v(-39.06, -19.13) * mm});
            skLineSegment(sketch, "E451", {"start": v(-39.06, -19.13) * mm, "end": v(-39.06, -14.42) * mm});
            skLineSegment(sketch, "E452", {"start": v(-39.06, -14.42) * mm, "end": v(-36.4, -14.42) * mm});
            skLineSegment(sketch, "E453", {"start": v(-36.4, -14.42) * mm, "end": v(-36.4, -17.04) * mm});
            skLineSegment(sketch, "E454", {"start": v(-36.4, -17.04) * mm, "end": v(-36.17, -17.33) * mm});
            skLineSegment(sketch, "E455", {"start": v(-36.17, -17.33) * mm, "end": v(-33.8, -17.33) * mm});
            skLineSegment(sketch, "E456", {"start": v(-33.8, -17.33) * mm, "end": v(-33.8, -14.42) * mm});
            skLineSegment(sketch, "E457", {"start": v(-33.8, -14.42) * mm, "end": v(-31.2, -14.42) * mm});
            skLineSegment(sketch, "E458", {"start": v(-31.2, -14.42) * mm, "end": v(-31.2, -17.33) * mm});
            skLineSegment(sketch, "E459", {"start": v(-31.2, -17.33) * mm, "end": v(-28.01, -17.33) * mm});
            skLineSegment(sketch, "E460", {"start": v(-28.01, -17.33) * mm, "end": v(-28.01, -20.59) * mm});
            skLineSegment(sketch, "E461", {"start": v(-23.82, 4.74) * mm, "end": v(-23.46, 4.74) * mm});
            skLineSegment(sketch, "E462", {"start": v(-23.46, 4.74) * mm, "end": v(-23.4, 4.74) * mm});
            skLineSegment(sketch, "E463", {"start": v(-23.4, 4.74) * mm, "end": v(-23.25, 4.9) * mm});
            skLineSegment(sketch, "E464", {"start": v(-23.25, 4.9) * mm, "end": v(-23.25, 4.94) * mm});
            skLineSegment(sketch, "E465", {"start": v(-23.25, 4.94) * mm, "end": v(-23.25, 8.29) * mm});
            skLineSegment(sketch, "E466", {"start": v(-23.25, 8.29) * mm, "end": v(-22.2, 8.29) * mm});
            skLineSegment(sketch, "E467", {"start": v(-22.2, 8.29) * mm, "end": v(-22.2, 4.87) * mm});
            skLineSegment(sketch, "E468", {"start": v(-22.2, 4.87) * mm, "end": v(-22.2, 4.78) * mm});
            skLineSegment(sketch, "E469", {"start": v(-22.2, 4.78) * mm, "end": v(-22.26, 4.51) * mm});
            skLineSegment(sketch, "E470", {"start": v(-22.26, 4.51) * mm, "end": v(-22.45, 4.19) * mm});
            skLineSegment(sketch, "E471", {"start": v(-22.45, 4.19) * mm, "end": v(-22.78, 3.95) * mm});
            skLineSegment(sketch, "E472", {"start": v(-22.78, 3.95) * mm, "end": v(-23.14, 3.86) * mm});
            skLineSegment(sketch, "E473", {"start": v(-23.14, 3.86) * mm, "end": v(-23.26, 3.86) * mm});
            skLineSegment(sketch, "E474", {"start": v(-23.26, 3.86) * mm, "end": v(-23.82, 3.86) * mm});
            skLineSegment(sketch, "E475", {"start": v(-23.82, 3.86) * mm, "end": v(-23.82, 4.74) * mm});
            skLineSegment(sketch, "E476", {"start": v(-22.43, -11.98) * mm, "end": v(-22.26, -11.98) * mm});
            skLineSegment(sketch, "E477", {"start": v(-22.26, -11.98) * mm, "end": v(-21.74, -12.24) * mm});
            skLineSegment(sketch, "E478", {"start": v(-21.74, -12.24) * mm, "end": v(-21.46, -12.78) * mm});
            skLineSegment(sketch, "E479", {"start": v(-21.46, -12.78) * mm, "end": v(-21.46, -12.96) * mm});
            skLineSegment(sketch, "E480", {"start": v(-21.46, -12.96) * mm, "end": v(-21.46, -13.16) * mm});
            skLineSegment(sketch, "E481", {"start": v(-21.46, -13.16) * mm, "end": v(-21.67, -13.69) * mm});
            skLineSegment(sketch, "E482", {"start": v(-21.67, -13.69) * mm, "end": v(-21.7, -13.76) * mm});
            skLineSegment(sketch, "E483", {"start": v(-21.7, -13.76) * mm, "end": v(-22.45, -15.27) * mm});
            skLineSegment(sketch, "E484", {"start": v(-22.45, -15.27) * mm, "end": v(-22.95, -15.27) * mm});
            skLineSegment(sketch, "E485", {"start": v(-22.95, -15.27) * mm, "end": v(-22.25, -13.87) * mm});
            skLineSegment(sketch, "E486", {"start": v(-22.25, -13.87) * mm, "end": v(-22.27, -13.88) * mm});
            skLineSegment(sketch, "E487", {"start": v(-22.27, -13.88) * mm, "end": v(-22.47, -13.92) * mm});
            skLineSegment(sketch, "E488", {"start": v(-22.47, -13.92) * mm, "end": v(-22.54, -13.92) * mm});
            skLineSegment(sketch, "E489", {"start": v(-22.54, -13.92) * mm, "end": v(-22.7, -13.92) * mm});
            skLineSegment(sketch, "E490", {"start": v(-22.7, -13.92) * mm, "end": v(-23.15, -13.66) * mm});
            skLineSegment(sketch, "E491", {"start": v(-23.15, -13.66) * mm, "end": v(-23.4, -13.15) * mm});
            skLineSegment(sketch, "E492", {"start": v(-23.4, -13.15) * mm, "end": v(-23.4, -12.97) * mm});
            skLineSegment(sketch, "E493", {"start": v(-23.4, -12.97) * mm, "end": v(-23.4, -12.8) * mm});
            skLineSegment(sketch, "E494", {"start": v(-23.4, -12.8) * mm, "end": v(-23.12, -12.25) * mm});
            skLineSegment(sketch, "E495", {"start": v(-23.12, -12.25) * mm, "end": v(-22.6, -11.98) * mm});
            skLineSegment(sketch, "E496", {"start": v(-22.6, -11.98) * mm, "end": v(-22.43, -11.98) * mm});
            skLineSegment(sketch, "E497", {"start": v(-21.14, -17.95) * mm, "end": v(-22.73, -17.95) * mm});
            skLineSegment(sketch, "E498", {"start": v(-22.73, -17.95) * mm, "end": v(-22.73, -18.95) * mm});
            skLineSegment(sketch, "E499", {"start": v(-22.73, -18.95) * mm, "end": v(-21.37, -18.95) * mm});
            skLineSegment(sketch, "E500", {"start": v(-21.37, -18.95) * mm, "end": v(-21.37, -19.4) * mm});
            skLineSegment(sketch, "E501", {"start": v(-21.37, -19.4) * mm, "end": v(-22.73, -19.4) * mm});
            skLineSegment(sketch, "E502", {"start": v(-22.73, -19.4) * mm, "end": v(-22.73, -20.78) * mm});
            skLineSegment(sketch, "E503", {"start": v(-22.73, -20.78) * mm, "end": v(-23.23, -20.78) * mm});
            skLineSegment(sketch, "E504", {"start": v(-23.23, -20.78) * mm, "end": v(-23.23, -17.5) * mm});
            skLineSegment(sketch, "E505", {"start": v(-23.23, -17.5) * mm, "end": v(-21.14, -17.5) * mm});
            skLineSegment(sketch, "E506", {"start": v(-21.14, -17.5) * mm, "end": v(-21.14, -17.95) * mm});
            skLineSegment(sketch, "E507", {"start": v(-21, 6.08) * mm, "end": v(-21, 6.25) * mm});
            skLineSegment(sketch, "E508", {"start": v(-21, 6.25) * mm, "end": v(-20.73, 6.76) * mm});
            skLineSegment(sketch, "E509", {"start": v(-20.73, 6.76) * mm, "end": v(-20.06, 7.07) * mm});
            skLineSegment(sketch, "E510", {"start": v(-20.06, 7.07) * mm, "end": v(-19.84, 7.07) * mm});
            skLineSegment(sketch, "E511", {"start": v(-19.84, 7.07) * mm, "end": v(-19.15, 7.07) * mm});
            skLineSegment(sketch, "E512", {"start": v(-19.15, 7.07) * mm, "end": v(-19.15, 7.15) * mm});
            skLineSegment(sketch, "E513", {"start": v(-19.15, 7.15) * mm, "end": v(-19.15, 7.24) * mm});
            skLineSegment(sketch, "E514", {"start": v(-19.15, 7.24) * mm, "end": v(-19.27, 7.49) * mm});
            skLineSegment(sketch, "E515", {"start": v(-19.27, 7.49) * mm, "end": v(-19.57, 7.58) * mm});
            skLineSegment(sketch, "E516", {"start": v(-19.57, 7.58) * mm, "end": v(-19.66, 7.58) * mm});
            skLineSegment(sketch, "E517", {"start": v(-19.66, 7.58) * mm, "end": v(-19.74, 7.58) * mm});
            skLineSegment(sketch, "E518", {"start": v(-19.74, 7.58) * mm, "end": v(-19.98, 7.53) * mm});
            skLineSegment(sketch, "E519", {"start": v(-19.98, 7.53) * mm, "end": v(-20.17, 7.4) * mm});
            skLineSegment(sketch, "E520", {"start": v(-20.17, 7.4) * mm, "end": v(-20.21, 7.35) * mm});
            skLineSegment(sketch, "E521", {"start": v(-20.21, 7.35) * mm, "end": v(-20.86, 8) * mm});
            skLineSegment(sketch, "E522", {"start": v(-20.86, 8) * mm, "end": v(-20.77, 8.09) * mm});
            skLineSegment(sketch, "E523", {"start": v(-20.77, 8.09) * mm, "end": v(-20.32, 8.36) * mm});
            skLineSegment(sketch, "E524", {"start": v(-20.32, 8.36) * mm, "end": v(-19.79, 8.46) * mm});
            skLineSegment(sketch, "E525", {"start": v(-19.79, 8.46) * mm, "end": v(-19.61, 8.46) * mm});
            skLineSegment(sketch, "E526", {"start": v(-19.61, 8.46) * mm, "end": v(-19.45, 8.46) * mm});
            skLineSegment(sketch, "E527", {"start": v(-19.45, 8.46) * mm, "end": v(-18.97, 8.38) * mm});
            skLineSegment(sketch, "E528", {"start": v(-18.97, 8.38) * mm, "end": v(-18.5, 8.15) * mm});
            skLineSegment(sketch, "E529", {"start": v(-18.5, 8.15) * mm, "end": v(-18.2, 7.76) * mm});
            skLineSegment(sketch, "E530", {"start": v(-18.2, 7.76) * mm, "end": v(-18.1, 7.35) * mm});
            skLineSegment(sketch, "E531", {"start": v(-18.1, 7.35) * mm, "end": v(-18.1, 7.22) * mm});
            skLineSegment(sketch, "E532", {"start": v(-18.1, 7.22) * mm, "end": v(-18.1, 5) * mm});
            skLineSegment(sketch, "E533", {"start": v(-18.1, 5) * mm, "end": v(-19.12, 5) * mm});
            skLineSegment(sketch, "E534", {"start": v(-19.12, 5) * mm, "end": v(-19.12, 5.28) * mm});
            skLineSegment(sketch, "E535", {"start": v(-19.12, 5.28) * mm, "end": v(-19.18, 5.23) * mm});
            skLineSegment(sketch, "E536", {"start": v(-19.18, 5.23) * mm, "end": v(-19.45, 5.05) * mm});
            skLineSegment(sketch, "E537", {"start": v(-19.45, 5.05) * mm, "end": v(-19.78, 4.97) * mm});
            skLineSegment(sketch, "E538", {"start": v(-19.78, 4.97) * mm, "end": v(-19.89, 4.97) * mm});
            skLineSegment(sketch, "E539", {"start": v(-19.89, 4.97) * mm, "end": v(-20.1, 4.97) * mm});
            skLineSegment(sketch, "E540", {"start": v(-20.1, 4.97) * mm, "end": v(-20.66, 5.23) * mm});
            skLineSegment(sketch, "E541", {"start": v(-20.66, 5.23) * mm, "end": v(-20.7, 5.28) * mm});
            skLineSegment(sketch, "E542", {"start": v(-20.7, 5.28) * mm, "end": v(-20.75, 5.32) * mm});
            skLineSegment(sketch, "E543", {"start": v(-20.75, 5.32) * mm, "end": v(-21, 5.89) * mm});
            skLineSegment(sketch, "E544", {"start": v(-21, 5.89) * mm, "end": v(-21, 6.08) * mm});
            skLineSegment(sketch, "E545", {"start": v(-20.47, -14.36) * mm, "end": v(-20.47, -12.91) * mm});
            skLineSegment(sketch, "E546", {"start": v(-20.47, -12.91) * mm, "end": v(-20.47, -12.74) * mm});
            skLineSegment(sketch, "E547", {"start": v(-20.47, -12.74) * mm, "end": v(-20.2, -12.23) * mm});
            skLineSegment(sketch, "E548", {"start": v(-20.2, -12.23) * mm, "end": v(-19.7, -11.98) * mm});
            skLineSegment(sketch, "E549", {"start": v(-19.7, -11.98) * mm, "end": v(-19.53, -11.98) * mm});
            skLineSegment(sketch, "E550", {"start": v(-19.53, -11.98) * mm, "end": v(-19.36, -11.98) * mm});
            skLineSegment(sketch, "E551", {"start": v(-19.36, -11.98) * mm, "end": v(-18.86, -12.23) * mm});
            skLineSegment(sketch, "E552", {"start": v(-18.86, -12.23) * mm, "end": v(-18.58, -12.74) * mm});
            skLineSegment(sketch, "E553", {"start": v(-18.58, -12.74) * mm, "end": v(-18.58, -12.91) * mm});
            skLineSegment(sketch, "E554", {"start": v(-18.58, -12.91) * mm, "end": v(-18.58, -14.36) * mm});
            skLineSegment(sketch, "E555", {"start": v(-18.58, -14.36) * mm, "end": v(-18.58, -14.54) * mm});
            skLineSegment(sketch, "E556", {"start": v(-18.58, -14.54) * mm, "end": v(-18.86, -15.05) * mm});
            skLineSegment(sketch, "E557", {"start": v(-18.86, -15.05) * mm, "end": v(-19.36, -15.3) * mm});
            skLineSegment(sketch, "E558", {"start": v(-19.36, -15.3) * mm, "end": v(-19.53, -15.3) * mm});
            skLineSegment(sketch, "E559", {"start": v(-19.53, -15.3) * mm, "end": v(-19.7, -15.3) * mm});
            skLineSegment(sketch, "E560", {"start": v(-19.7, -15.3) * mm, "end": v(-20.2, -15.05) * mm});
            skLineSegment(sketch, "E561", {"start": v(-20.2, -15.05) * mm, "end": v(-20.47, -14.54) * mm});
            skLineSegment(sketch, "E562", {"start": v(-20.47, -14.54) * mm, "end": v(-20.47, -14.36) * mm});
            skLineSegment(sketch, "E563", {"start": v(-18.28, -20.78) * mm, "end": v(-18.97, -19.4) * mm});
            skLineSegment(sketch, "E564", {"start": v(-18.97, -19.4) * mm, "end": v(-19.59, -19.4) * mm});
            skLineSegment(sketch, "E565", {"start": v(-19.59, -19.4) * mm, "end": v(-19.59, -20.78) * mm});
            skLineSegment(sketch, "E566", {"start": v(-19.59, -20.78) * mm, "end": v(-20.08, -20.78) * mm});
            skLineSegment(sketch, "E567", {"start": v(-20.08, -20.78) * mm, "end": v(-20.08, -17.5) * mm});
            skLineSegment(sketch, "E568", {"start": v(-20.08, -17.5) * mm, "end": v(-18.82, -17.5) * mm});
            skLineSegment(sketch, "E569", {"start": v(-18.82, -17.5) * mm, "end": v(-18.63, -17.5) * mm});
            skLineSegment(sketch, "E570", {"start": v(-18.63, -17.5) * mm, "end": v(-18.08, -17.78) * mm});
            skLineSegment(sketch, "E571", {"start": v(-18.08, -17.78) * mm, "end": v(-17.8, -18.3) * mm});
            skLineSegment(sketch, "E572", {"start": v(-17.8, -18.3) * mm, "end": v(-17.8, -18.46) * mm});
            skLineSegment(sketch, "E573", {"start": v(-17.8, -18.46) * mm, "end": v(-17.8, -18.6) * mm});
            skLineSegment(sketch, "E574", {"start": v(-17.8, -18.6) * mm, "end": v(-18, -19.03) * mm});
            skLineSegment(sketch, "E575", {"start": v(-18, -19.03) * mm, "end": v(-18.37, -19.3) * mm});
            skLineSegment(sketch, "E576", {"start": v(-18.37, -19.3) * mm, "end": v(-18.46, -19.33) * mm});
            skLineSegment(sketch, "E577", {"start": v(-18.46, -19.33) * mm, "end": v(-17.7, -20.78) * mm});
            skLineSegment(sketch, "E578", {"start": v(-17.7, -20.78) * mm, "end": v(-18.28, -20.78) * mm});
            skLineSegment(sketch, "E579", {"start": v(-17.63, -14.35) * mm, "end": v(-17.63, -14.23) * mm});
            skLineSegment(sketch, "E580", {"start": v(-17.63, -14.23) * mm, "end": v(-17.5, -13.87) * mm});
            skLineSegment(sketch, "E581", {"start": v(-17.5, -13.87) * mm, "end": v(-17.24, -13.62) * mm});
            skLineSegment(sketch, "E582", {"start": v(-17.24, -13.62) * mm, "end": v(-17.18, -13.58) * mm});
            skLineSegment(sketch, "E583", {"start": v(-17.18, -13.58) * mm, "end": v(-17.23, -13.55) * mm});
            skLineSegment(sketch, "E584", {"start": v(-17.23, -13.55) * mm, "end": v(-17.46, -13.31) * mm});
            skLineSegment(sketch, "E585", {"start": v(-17.46, -13.31) * mm, "end": v(-17.58, -13) * mm});
            skLineSegment(sketch, "E586", {"start": v(-17.58, -13) * mm, "end": v(-17.58, -12.88) * mm});
            skLineSegment(sketch, "E587", {"start": v(-17.58, -12.88) * mm, "end": v(-17.58, -12.72) * mm});
            skLineSegment(sketch, "E588", {"start": v(-17.58, -12.72) * mm, "end": v(-17.3, -12.23) * mm});
            skLineSegment(sketch, "E589", {"start": v(-17.3, -12.23) * mm, "end": v(-16.8, -11.98) * mm});
            skLineSegment(sketch, "E590", {"start": v(-16.8, -11.98) * mm, "end": v(-16.63, -11.98) * mm});
            skLineSegment(sketch, "E591", {"start": v(-16.63, -11.98) * mm, "end": v(-16.46, -11.98) * mm});
            skLineSegment(sketch, "E592", {"start": v(-16.46, -11.98) * mm, "end": v(-15.95, -12.23) * mm});
            skLineSegment(sketch, "E593", {"start": v(-15.95, -12.23) * mm, "end": v(-15.67, -12.72) * mm});
            skLineSegment(sketch, "E594", {"start": v(-15.67, -12.72) * mm, "end": v(-15.67, -12.88) * mm});
            skLineSegment(sketch, "E595", {"start": v(-15.67, -12.88) * mm, "end": v(-15.67, -13) * mm});
            skLineSegment(sketch, "E596", {"start": v(-15.67, -13) * mm, "end": v(-15.8, -13.31) * mm});
            skLineSegment(sketch, "E597", {"start": v(-15.8, -13.31) * mm, "end": v(-16.01, -13.55) * mm});
            skLineSegment(sketch, "E598", {"start": v(-16.01, -13.55) * mm, "end": v(-16.07, -13.58) * mm});
            skLineSegment(sketch, "E599", {"start": v(-16.07, -13.58) * mm, "end": v(-16, -13.62) * mm});
            skLineSegment(sketch, "E600", {"start": v(-16, -13.62) * mm, "end": v(-15.76, -13.87) * mm});
            skLineSegment(sketch, "E601", {"start": v(-15.76, -13.87) * mm, "end": v(-15.62, -14.23) * mm});
            skLineSegment(sketch, "E602", {"start": v(-15.62, -14.23) * mm, "end": v(-15.62, -14.35) * mm});
            skLineSegment(sketch, "E603", {"start": v(-15.62, -14.35) * mm, "end": v(-15.62, -14.52) * mm});
            skLineSegment(sketch, "E604", {"start": v(-15.62, -14.52) * mm, "end": v(-15.91, -15.05) * mm});
            skLineSegment(sketch, "E605", {"start": v(-15.91, -15.05) * mm, "end": v(-16.45, -15.3) * mm});
            skLineSegment(sketch, "E606", {"start": v(-16.45, -15.3) * mm, "end": v(-16.63, -15.3) * mm});
            skLineSegment(sketch, "E607", {"start": v(-16.63, -15.3) * mm, "end": v(-16.8, -15.3) * mm});
            skLineSegment(sketch, "E608", {"start": v(-16.8, -15.3) * mm, "end": v(-17.34, -15.05) * mm});
            skLineSegment(sketch, "E609", {"start": v(-17.34, -15.05) * mm, "end": v(-17.63, -14.52) * mm});
            skLineSegment(sketch, "E610", {"start": v(-17.63, -14.52) * mm, "end": v(-17.63, -14.35) * mm});
            skLineSegment(sketch, "E611", {"start": v(-14.53, -17.95) * mm, "end": v(-16.13, -17.95) * mm});
            skLineSegment(sketch, "E612", {"start": v(-16.13, -17.95) * mm, "end": v(-16.13, -18.9) * mm});
            skLineSegment(sketch, "E613", {"start": v(-16.13, -18.9) * mm, "end": v(-14.77, -18.9) * mm});
            skLineSegment(sketch, "E614", {"start": v(-14.77, -18.9) * mm, "end": v(-14.77, -19.35) * mm});
            skLineSegment(sketch, "E615", {"start": v(-14.77, -19.35) * mm, "end": v(-16.13, -19.35) * mm});
            skLineSegment(sketch, "E616", {"start": v(-16.13, -19.35) * mm, "end": v(-16.13, -20.33) * mm});
            skLineSegment(sketch, "E617", {"start": v(-16.13, -20.33) * mm, "end": v(-14.53, -20.33) * mm});
            skLineSegment(sketch, "E618", {"start": v(-14.53, -20.33) * mm, "end": v(-14.53, -20.78) * mm});
            skLineSegment(sketch, "E619", {"start": v(-14.53, -20.78) * mm, "end": v(-16.62, -20.78) * mm});
            skLineSegment(sketch, "E620", {"start": v(-16.62, -20.78) * mm, "end": v(-16.62, -17.5) * mm});
            skLineSegment(sketch, "E621", {"start": v(-16.62, -17.5) * mm, "end": v(-14.53, -17.5) * mm});
            skLineSegment(sketch, "E622", {"start": v(-14.53, -17.5) * mm, "end": v(-14.53, -17.95) * mm});
            skLineSegment(sketch, "E623", {"start": v(-14.94, -15.61) * mm, "end": v(-13.64, -11.67) * mm});
            skLineSegment(sketch, "E624", {"start": v(-13.64, -11.67) * mm, "end": v(-13.19, -11.67) * mm});
            skLineSegment(sketch, "E625", {"start": v(-13.19, -11.67) * mm, "end": v(-14.5, -15.61) * mm});
            skLineSegment(sketch, "E626", {"start": v(-14.5, -15.61) * mm, "end": v(-14.94, -15.61) * mm});
            skLineSegment(sketch, "E627", {"start": v(-11.4, -20.47) * mm, "end": v(-11.46, -20.52) * mm});
            skLineSegment(sketch, "E628", {"start": v(-11.46, -20.52) * mm, "end": v(-12.05, -20.78) * mm});
            skLineSegment(sketch, "E629", {"start": v(-12.05, -20.78) * mm, "end": v(-12.25, -20.78) * mm});
            skLineSegment(sketch, "E630", {"start": v(-12.25, -20.78) * mm, "end": v(-13.4, -20.78) * mm});
            skLineSegment(sketch, "E631", {"start": v(-13.4, -20.78) * mm, "end": v(-13.4, -17.5) * mm});
            skLineSegment(sketch, "E632", {"start": v(-13.4, -17.5) * mm, "end": v(-12.25, -17.5) * mm});
            skLineSegment(sketch, "E633", {"start": v(-12.25, -17.5) * mm, "end": v(-12.04, -17.5) * mm});
            skLineSegment(sketch, "E634", {"start": v(-12.04, -17.5) * mm, "end": v(-11.46, -17.76) * mm});
            skLineSegment(sketch, "E635", {"start": v(-11.46, -17.76) * mm, "end": v(-11.4, -17.82) * mm});
            skLineSegment(sketch, "E636", {"start": v(-11.4, -17.82) * mm, "end": v(-11.32, -17.9) * mm});
            skLineSegment(sketch, "E637", {"start": v(-11.32, -17.9) * mm, "end": v(-11.1, -18.42) * mm});
            skLineSegment(sketch, "E638", {"start": v(-11.1, -18.42) * mm, "end": v(-11.08, -18.94) * mm});
            skLineSegment(sketch, "E639", {"start": v(-11.08, -18.94) * mm, "end": v(-11.08, -19.12) * mm});
            skLineSegment(sketch, "E640", {"start": v(-11.08, -19.12) * mm, "end": v(-11.08, -19.3) * mm});
            skLineSegment(sketch, "E641", {"start": v(-11.08, -19.3) * mm, "end": v(-11.1, -19.84) * mm});
            skLineSegment(sketch, "E642", {"start": v(-11.1, -19.84) * mm, "end": v(-11.32, -20.38) * mm});
            skLineSegment(sketch, "E643", {"start": v(-11.32, -20.38) * mm, "end": v(-11.4, -20.47) * mm});
            skLineSegment(sketch, "E644", {"start": v(-10.5, -12.42) * mm, "end": v(-11.6, -15.27) * mm});
            skLineSegment(sketch, "E645", {"start": v(-11.6, -15.27) * mm, "end": v(-12.1, -15.27) * mm});
            skLineSegment(sketch, "E646", {"start": v(-12.1, -15.27) * mm, "end": v(-11, -12.42) * mm});
            skLineSegment(sketch, "E647", {"start": v(-11, -12.42) * mm, "end": v(-12, -12.42) * mm});
            skLineSegment(sketch, "E648", {"start": v(-12, -12.42) * mm, "end": v(-12, -12.94) * mm});
            skLineSegment(sketch, "E649", {"start": v(-12, -12.94) * mm, "end": v(-12.45, -12.94) * mm});
            skLineSegment(sketch, "E650", {"start": v(-12.45, -12.94) * mm, "end": v(-12.45, -12) * mm});
            skLineSegment(sketch, "E651", {"start": v(-12.45, -12) * mm, "end": v(-10.5, -12) * mm});
            skLineSegment(sketch, "E652", {"start": v(-10.5, -12) * mm, "end": v(-10.5, -12.42) * mm});
            skLineSegment(sketch, "E653", {"start": v(-10.46, 5.4) * mm, "end": v(-10.5, 5.35) * mm});
            skLineSegment(sketch, "E654", {"start": v(-10.5, 5.35) * mm, "end": v(-10.88, 5.1) * mm});
            skLineSegment(sketch, "E655", {"start": v(-10.88, 5.1) * mm, "end": v(-11.39, 4.96) * mm});
            skLineSegment(sketch, "E656", {"start": v(-11.39, 4.96) * mm, "end": v(-11.55, 4.96) * mm});
            skLineSegment(sketch, "E657", {"start": v(-11.55, 4.96) * mm, "end": v(-11.73, 4.96) * mm});
            skLineSegment(sketch, "E658", {"start": v(-11.73, 4.96) * mm, "end": v(-12.24, 5.1) * mm});
            skLineSegment(sketch, "E659", {"start": v(-12.24, 5.1) * mm, "end": v(-12.6, 5.35) * mm});
            skLineSegment(sketch, "E660", {"start": v(-12.6, 5.35) * mm, "end": v(-12.65, 5.4) * mm});
            skLineSegment(sketch, "E661", {"start": v(-12.65, 5.4) * mm, "end": v(-12.72, 5.48) * mm});
            skLineSegment(sketch, "E662", {"start": v(-12.72, 5.48) * mm, "end": v(-12.95, 5.92) * mm});
            skLineSegment(sketch, "E663", {"start": v(-12.95, 5.92) * mm, "end": v(-13.03, 6.51) * mm});
            skLineSegment(sketch, "E664", {"start": v(-13.03, 6.51) * mm, "end": v(-13.03, 6.71) * mm});
            skLineSegment(sketch, "E665", {"start": v(-13.03, 6.71) * mm, "end": v(-13.03, 6.9) * mm});
            skLineSegment(sketch, "E666", {"start": v(-13.03, 6.9) * mm, "end": v(-12.95, 7.5) * mm});
            skLineSegment(sketch, "E667", {"start": v(-12.95, 7.5) * mm, "end": v(-12.72, 7.94) * mm});
            skLineSegment(sketch, "E668", {"start": v(-12.72, 7.94) * mm, "end": v(-12.65, 8.02) * mm});
            skLineSegment(sketch, "E669", {"start": v(-12.65, 8.02) * mm, "end": v(-12.6, 8.07) * mm});
            skLineSegment(sketch, "E670", {"start": v(-12.6, 8.07) * mm, "end": v(-12.24, 8.32) * mm});
            skLineSegment(sketch, "E671", {"start": v(-12.24, 8.32) * mm, "end": v(-11.73, 8.46) * mm});
            skLineSegment(sketch, "E672", {"start": v(-11.73, 8.46) * mm, "end": v(-11.55, 8.46) * mm});
            skLineSegment(sketch, "E673", {"start": v(-11.55, 8.46) * mm, "end": v(-11.39, 8.46) * mm});
            skLineSegment(sketch, "E674", {"start": v(-11.39, 8.46) * mm, "end": v(-10.88, 8.32) * mm});
            skLineSegment(sketch, "E675", {"start": v(-10.88, 8.32) * mm, "end": v(-10.5, 8.07) * mm});
            skLineSegment(sketch, "E676", {"start": v(-10.5, 8.07) * mm, "end": v(-10.46, 8.02) * mm});
            skLineSegment(sketch, "E677", {"start": v(-10.46, 8.02) * mm, "end": v(-10.38, 7.94) * mm});
            skLineSegment(sketch, "E678", {"start": v(-10.38, 7.94) * mm, "end": v(-10.16, 7.5) * mm});
            skLineSegment(sketch, "E679", {"start": v(-10.16, 7.5) * mm, "end": v(-10.08, 6.9) * mm});
            skLineSegment(sketch, "E680", {"start": v(-10.08, 6.9) * mm, "end": v(-10.08, 6.71) * mm});
            skLineSegment(sketch, "E681", {"start": v(-10.08, 6.71) * mm, "end": v(-10.08, 6.51) * mm});
            skLineSegment(sketch, "E682", {"start": v(-10.08, 6.51) * mm, "end": v(-10.16, 5.92) * mm});
            skLineSegment(sketch, "E683", {"start": v(-10.16, 5.92) * mm, "end": v(-10.38, 5.48) * mm});
            skLineSegment(sketch, "E684", {"start": v(-10.38, 5.48) * mm, "end": v(-10.46, 5.4) * mm});
            skLineSegment(sketch, "E685", {"start": v(-9.47, -20.78) * mm, "end": v(-9.94, -20.78) * mm});
            skLineSegment(sketch, "E686", {"start": v(-9.94, -20.78) * mm, "end": v(-9.94, -18.45) * mm});
            skLineSegment(sketch, "E687", {"start": v(-9.94, -18.45) * mm, "end": v(-9.47, -18.45) * mm});
            skLineSegment(sketch, "E688", {"start": v(-9.47, -18.45) * mm, "end": v(-9.47, -20.78) * mm});
            skLineSegment(sketch, "E689", {"start": v(-9.46, -18) * mm, "end": v(-9.95, -18) * mm});
            skLineSegment(sketch, "E690", {"start": v(-9.95, -18) * mm, "end": v(-9.95, -17.5) * mm});
            skLineSegment(sketch, "E691", {"start": v(-9.95, -17.5) * mm, "end": v(-9.46, -17.5) * mm});
            skLineSegment(sketch, "E692", {"start": v(-9.46, -17.5) * mm, "end": v(-9.46, -18) * mm});
            skLineSegment(sketch, "E693", {"start": v(-9.58, -14.32) * mm, "end": v(-9.58, -14.12) * mm});
            skLineSegment(sketch, "E694", {"start": v(-9.58, -14.12) * mm, "end": v(-9.37, -13.6) * mm});
            skLineSegment(sketch, "E695", {"start": v(-9.37, -13.6) * mm, "end": v(-9.34, -13.52) * mm});
            skLineSegment(sketch, "E696", {"start": v(-9.34, -13.52) * mm, "end": v(-8.6, -12) * mm});
            skLineSegment(sketch, "E697", {"start": v(-8.6, -12) * mm, "end": v(-8.1, -12) * mm});
            skLineSegment(sketch, "E698", {"start": v(-8.1, -12) * mm, "end": v(-8.8, -13.4) * mm});
            skLineSegment(sketch, "E699", {"start": v(-8.8, -13.4) * mm, "end": v(-8.78, -13.4) * mm});
            skLineSegment(sketch, "E700", {"start": v(-8.78, -13.4) * mm, "end": v(-8.58, -13.36) * mm});
            skLineSegment(sketch, "E701", {"start": v(-8.58, -13.36) * mm, "end": v(-8.5, -13.36) * mm});
            skLineSegment(sketch, "E702", {"start": v(-8.5, -13.36) * mm, "end": v(-8.36, -13.36) * mm});
            skLineSegment(sketch, "E703", {"start": v(-8.36, -13.36) * mm, "end": v(-7.9, -13.62) * mm});
            skLineSegment(sketch, "E704", {"start": v(-7.9, -13.62) * mm, "end": v(-7.65, -14.13) * mm});
            skLineSegment(sketch, "E705", {"start": v(-7.65, -14.13) * mm, "end": v(-7.65, -14.3) * mm});
            skLineSegment(sketch, "E706", {"start": v(-7.65, -14.3) * mm, "end": v(-7.65, -14.48) * mm});
            skLineSegment(sketch, "E707", {"start": v(-7.65, -14.48) * mm, "end": v(-7.92, -15.03) * mm});
            skLineSegment(sketch, "E708", {"start": v(-7.92, -15.03) * mm, "end": v(-8.44, -15.3) * mm});
            skLineSegment(sketch, "E709", {"start": v(-8.44, -15.3) * mm, "end": v(-8.61, -15.3) * mm});
            skLineSegment(sketch, "E710", {"start": v(-8.61, -15.3) * mm, "end": v(-8.79, -15.3) * mm});
            skLineSegment(sketch, "E711", {"start": v(-8.79, -15.3) * mm, "end": v(-9.31, -15.04) * mm});
            skLineSegment(sketch, "E712", {"start": v(-9.31, -15.04) * mm, "end": v(-9.58, -14.5) * mm});
            skLineSegment(sketch, "E713", {"start": v(-9.58, -14.5) * mm, "end": v(-9.58, -14.32) * mm});
            skLineSegment(sketch, "E714", {"start": v(-7.52, -20.8) * mm, "end": v(-7.65, -20.8) * mm});
            skLineSegment(sketch, "E715", {"start": v(-7.65, -20.8) * mm, "end": v(-8.05, -20.74) * mm});
            skLineSegment(sketch, "E716", {"start": v(-8.05, -20.74) * mm, "end": v(-8.43, -20.54) * mm});
            skLineSegment(sketch, "E717", {"start": v(-8.43, -20.54) * mm, "end": v(-8.5, -20.47) * mm});
            skLineSegment(sketch, "E718", {"start": v(-8.5, -20.47) * mm, "end": v(-8.19, -20.16) * mm});
            skLineSegment(sketch, "E719", {"start": v(-8.19, -20.16) * mm, "end": v(-8.14, -20.2) * mm});
            skLineSegment(sketch, "E720", {"start": v(-8.14, -20.2) * mm, "end": v(-7.67, -20.4) * mm});
            skLineSegment(sketch, "E721", {"start": v(-7.67, -20.4) * mm, "end": v(-7.52, -20.4) * mm});
            skLineSegment(sketch, "E722", {"start": v(-7.52, -20.4) * mm, "end": v(-7.43, -20.4) * mm});
            skLineSegment(sketch, "E723", {"start": v(-7.43, -20.4) * mm, "end": v(-7.16, -20.33) * mm});
            skLineSegment(sketch, "E724", {"start": v(-7.16, -20.33) * mm, "end": v(-7, -20.14) * mm});
            skLineSegment(sketch, "E725", {"start": v(-7, -20.14) * mm, "end": v(-7, -20.08) * mm});
            skLineSegment(sketch, "E726", {"start": v(-7, -20.08) * mm, "end": v(-7, -20.01) * mm});
            skLineSegment(sketch, "E727", {"start": v(-7, -20.01) * mm, "end": v(-7.26, -19.81) * mm});
            skLineSegment(sketch, "E728", {"start": v(-7.26, -19.81) * mm, "end": v(-7.32, -19.8) * mm});
            skLineSegment(sketch, "E729", {"start": v(-7.32, -19.8) * mm, "end": v(-7.7, -19.78) * mm});
            skLineSegment(sketch, "E730", {"start": v(-7.7, -19.78) * mm, "end": v(-7.8, -19.77) * mm});
            skLineSegment(sketch, "E731", {"start": v(-7.8, -19.77) * mm, "end": v(-8.2, -19.6) * mm});
            skLineSegment(sketch, "E732", {"start": v(-8.2, -19.6) * mm, "end": v(-8.38, -19.25) * mm});
            skLineSegment(sketch, "E733", {"start": v(-8.38, -19.25) * mm, "end": v(-8.38, -19.13) * mm});
            skLineSegment(sketch, "E734", {"start": v(-8.38, -19.13) * mm, "end": v(-8.38, -19) * mm});
            skLineSegment(sketch, "E735", {"start": v(-8.38, -19) * mm, "end": v(-8.12, -18.6) * mm});
            skLineSegment(sketch, "E736", {"start": v(-8.12, -18.6) * mm, "end": v(-7.66, -18.42) * mm});
            skLineSegment(sketch, "E737", {"start": v(-7.66, -18.42) * mm, "end": v(-7.5, -18.42) * mm});
            skLineSegment(sketch, "E738", {"start": v(-7.5, -18.42) * mm, "end": v(-7.29, -18.42) * mm});
            skLineSegment(sketch, "E739", {"start": v(-7.29, -18.42) * mm, "end": v(-6.7, -18.64) * mm});
            skLineSegment(sketch, "E740", {"start": v(-6.7, -18.64) * mm, "end": v(-6.64, -18.68) * mm});
            skLineSegment(sketch, "E741", {"start": v(-6.64, -18.68) * mm, "end": v(-6.94, -18.98) * mm});
            skLineSegment(sketch, "E742", {"start": v(-6.94, -18.98) * mm, "end": v(-6.97, -18.95) * mm});
            skLineSegment(sketch, "E743", {"start": v(-6.97, -18.95) * mm, "end": v(-7.38, -18.81) * mm});
            skLineSegment(sketch, "E744", {"start": v(-7.38, -18.81) * mm, "end": v(-7.5, -18.81) * mm});
            skLineSegment(sketch, "E745", {"start": v(-7.5, -18.81) * mm, "end": v(-7.59, -18.81) * mm});
            skLineSegment(sketch, "E746", {"start": v(-7.59, -18.81) * mm, "end": v(-7.83, -18.9) * mm});
            skLineSegment(sketch, "E747", {"start": v(-7.83, -18.9) * mm, "end": v(-7.93, -19.06) * mm});
            skLineSegment(sketch, "E748", {"start": v(-7.93, -19.06) * mm, "end": v(-7.93, -19.11) * mm});
            skLineSegment(sketch, "E749", {"start": v(-7.93, -19.11) * mm, "end": v(-7.93, -19.15) * mm});
            skLineSegment(sketch, "E750", {"start": v(-7.93, -19.15) * mm, "end": v(-7.86, -19.29) * mm});
            skLineSegment(sketch, "E751", {"start": v(-7.86, -19.29) * mm, "end": v(-7.67, -19.37) * mm});
            skLineSegment(sketch, "E752", {"start": v(-7.67, -19.37) * mm, "end": v(-7.6, -19.38) * mm});
            skLineSegment(sketch, "E753", {"start": v(-7.6, -19.38) * mm, "end": v(-7.24, -19.4) * mm});
            skLineSegment(sketch, "E754", {"start": v(-7.24, -19.4) * mm, "end": v(-7.13, -19.42) * mm});
            skLineSegment(sketch, "E755", {"start": v(-7.13, -19.42) * mm, "end": v(-6.73, -19.6) * mm});
            skLineSegment(sketch, "E756", {"start": v(-6.73, -19.6) * mm, "end": v(-6.55, -19.95) * mm});
            skLineSegment(sketch, "E757", {"start": v(-6.55, -19.95) * mm, "end": v(-6.55, -20.06) * mm});
            skLineSegment(sketch, "E758", {"start": v(-6.55, -20.06) * mm, "end": v(-6.55, -20.2) * mm});
            skLineSegment(sketch, "E759", {"start": v(-6.55, -20.2) * mm, "end": v(-6.83, -20.62) * mm});
            skLineSegment(sketch, "E760", {"start": v(-6.83, -20.62) * mm, "end": v(-7.34, -20.8) * mm});
            skLineSegment(sketch, "E761", {"start": v(-7.34, -20.8) * mm, "end": v(-7.52, -20.8) * mm});
            skLineSegment(sketch, "E762", {"start": v(-6.74, -14.39) * mm, "end": v(-6.28, -14.39) * mm});
            skLineSegment(sketch, "E763", {"start": v(-6.28, -14.39) * mm, "end": v(-6.27, -14.47) * mm});
            skLineSegment(sketch, "E764", {"start": v(-6.27, -14.47) * mm, "end": v(-6.1, -14.76) * mm});
            skLineSegment(sketch, "E765", {"start": v(-6.1, -14.76) * mm, "end": v(-5.83, -14.88) * mm});
            skLineSegment(sketch, "E766", {"start": v(-5.83, -14.88) * mm, "end": v(-5.74, -14.88) * mm});
            skLineSegment(sketch, "E767", {"start": v(-5.74, -14.88) * mm, "end": v(-5.65, -14.88) * mm});
            skLineSegment(sketch, "E768", {"start": v(-5.65, -14.88) * mm, "end": v(-5.36, -14.74) * mm});
            skLineSegment(sketch, "E769", {"start": v(-5.36, -14.74) * mm, "end": v(-5.21, -14.44) * mm});
            skLineSegment(sketch, "E770", {"start": v(-5.21, -14.44) * mm, "end": v(-5.21, -14.34) * mm});
            skLineSegment(sketch, "E771", {"start": v(-5.21, -14.34) * mm, "end": v(-5.21, -14.24) * mm});
            skLineSegment(sketch, "E772", {"start": v(-5.21, -14.24) * mm, "end": v(-5.35, -13.95) * mm});
            skLineSegment(sketch, "E773", {"start": v(-5.35, -13.95) * mm, "end": v(-5.66, -13.8) * mm});
            skLineSegment(sketch, "E774", {"start": v(-5.66, -13.8) * mm, "end": v(-5.76, -13.8) * mm});
            skLineSegment(sketch, "E775", {"start": v(-5.76, -13.8) * mm, "end": v(-5.83, -13.8) * mm});
            skLineSegment(sketch, "E776", {"start": v(-5.83, -13.8) * mm, "end": v(-5.83, -13.4) * mm});
            skLineSegment(sketch, "E777", {"start": v(-5.83, -13.4) * mm, "end": v(-5.76, -13.4) * mm});
            skLineSegment(sketch, "E778", {"start": v(-5.76, -13.4) * mm, "end": v(-5.66, -13.4) * mm});
            skLineSegment(sketch, "E779", {"start": v(-5.66, -13.4) * mm, "end": v(-5.38, -13.26) * mm});
            skLineSegment(sketch, "E780", {"start": v(-5.38, -13.26) * mm, "end": v(-5.26, -13) * mm});
            skLineSegment(sketch, "E781", {"start": v(-5.26, -13) * mm, "end": v(-5.26, -12.9) * mm});
            skLineSegment(sketch, "E782", {"start": v(-5.26, -12.9) * mm, "end": v(-5.26, -12.8) * mm});
            skLineSegment(sketch, "E783", {"start": v(-5.26, -12.8) * mm, "end": v(-5.4, -12.52) * mm});
            skLineSegment(sketch, "E784", {"start": v(-5.4, -12.52) * mm, "end": v(-5.66, -12.4) * mm});
            skLineSegment(sketch, "E785", {"start": v(-5.66, -12.4) * mm, "end": v(-5.74, -12.4) * mm});
            skLineSegment(sketch, "E786", {"start": v(-5.74, -12.4) * mm, "end": v(-5.83, -12.4) * mm});
            skLineSegment(sketch, "E787", {"start": v(-5.83, -12.4) * mm, "end": v(-6.09, -12.52) * mm});
            skLineSegment(sketch, "E788", {"start": v(-6.09, -12.52) * mm, "end": v(-6.23, -12.8) * mm});
            skLineSegment(sketch, "E789", {"start": v(-6.23, -12.8) * mm, "end": v(-6.23, -12.86) * mm});
            skLineSegment(sketch, "E790", {"start": v(-6.23, -12.86) * mm, "end": v(-6.7, -12.86) * mm});
            skLineSegment(sketch, "E791", {"start": v(-6.7, -12.86) * mm, "end": v(-6.7, -12.72) * mm});
            skLineSegment(sketch, "E792", {"start": v(-6.7, -12.72) * mm, "end": v(-6.4, -12.21) * mm});
            skLineSegment(sketch, "E793", {"start": v(-6.4, -12.21) * mm, "end": v(-5.91, -11.97) * mm});
            skLineSegment(sketch, "E794", {"start": v(-5.91, -11.97) * mm, "end": v(-5.74, -11.97) * mm});
            skLineSegment(sketch, "E795", {"start": v(-5.74, -11.97) * mm, "end": v(-5.57, -11.97) * mm});
            skLineSegment(sketch, "E796", {"start": v(-5.57, -11.97) * mm, "end": v(-5.06, -12.23) * mm});
            skLineSegment(sketch, "E797", {"start": v(-5.06, -12.23) * mm, "end": v(-4.8, -12.72) * mm});
            skLineSegment(sketch, "E798", {"start": v(-4.8, -12.72) * mm, "end": v(-4.8, -12.89) * mm});
            skLineSegment(sketch, "E799", {"start": v(-4.8, -12.89) * mm, "end": v(-4.8, -13) * mm});
            skLineSegment(sketch, "E800", {"start": v(-4.8, -13) * mm, "end": v(-4.9, -13.32) * mm});
            skLineSegment(sketch, "E801", {"start": v(-4.9, -13.32) * mm, "end": v(-5.14, -13.55) * mm});
            skLineSegment(sketch, "E802", {"start": v(-5.14, -13.55) * mm, "end": v(-5.2, -13.58) * mm});
            skLineSegment(sketch, "E803", {"start": v(-5.2, -13.58) * mm, "end": v(-5.13, -13.61) * mm});
            skLineSegment(sketch, "E804", {"start": v(-5.13, -13.61) * mm, "end": v(-4.87, -13.86) * mm});
            skLineSegment(sketch, "E805", {"start": v(-4.87, -13.86) * mm, "end": v(-4.74, -14.23) * mm});
            skLineSegment(sketch, "E806", {"start": v(-4.74, -14.23) * mm, "end": v(-4.74, -14.35) * mm});
            skLineSegment(sketch, "E807", {"start": v(-4.74, -14.35) * mm, "end": v(-4.74, -14.53) * mm});
            skLineSegment(sketch, "E808", {"start": v(-4.74, -14.53) * mm, "end": v(-5.04, -15.06) * mm});
            skLineSegment(sketch, "E809", {"start": v(-5.04, -15.06) * mm, "end": v(-5.57, -15.3) * mm});
            skLineSegment(sketch, "E810", {"start": v(-5.57, -15.3) * mm, "end": v(-5.74, -15.3) * mm});
            skLineSegment(sketch, "E811", {"start": v(-5.74, -15.3) * mm, "end": v(-5.92, -15.3) * mm});
            skLineSegment(sketch, "E812", {"start": v(-5.92, -15.3) * mm, "end": v(-6.43, -15.08) * mm});
            skLineSegment(sketch, "E813", {"start": v(-6.43, -15.08) * mm, "end": v(-6.74, -14.55) * mm});
            skLineSegment(sketch, "E814", {"start": v(-6.74, -14.55) * mm, "end": v(-6.74, -14.39) * mm});
            skLineSegment(sketch, "E815", {"start": v(-3.6, -20.78) * mm, "end": v(-3.82, -20.12) * mm});
            skLineSegment(sketch, "E816", {"start": v(-3.82, -20.12) * mm, "end": v(-5.1, -20.12) * mm});
            skLineSegment(sketch, "E817", {"start": v(-5.1, -20.12) * mm, "end": v(-5.33, -20.78) * mm});
            skLineSegment(sketch, "E818", {"start": v(-5.33, -20.78) * mm, "end": v(-5.86, -20.78) * mm});
            skLineSegment(sketch, "E819", {"start": v(-5.86, -20.78) * mm, "end": v(-4.66, -17.5) * mm});
            skLineSegment(sketch, "E820", {"start": v(-4.66, -17.5) * mm, "end": v(-4.26, -17.5) * mm});
            skLineSegment(sketch, "E821", {"start": v(-4.26, -17.5) * mm, "end": v(-3.06, -20.78) * mm});
            skLineSegment(sketch, "E822", {"start": v(-3.06, -20.78) * mm, "end": v(-3.6, -20.78) * mm});
            skLineSegment(sketch, "E823", {"start": v(-1.23, -18.85) * mm, "end": v(-1.67, -18.85) * mm});
            skLineSegment(sketch, "E824", {"start": v(-1.67, -18.85) * mm, "end": v(-1.67, -20.1) * mm});
            skLineSegment(sketch, "E825", {"start": v(-1.67, -20.1) * mm, "end": v(-1.67, -20.17) * mm});
            skLineSegment(sketch, "E826", {"start": v(-1.67, -20.17) * mm, "end": v(-1.48, -20.38) * mm});
            skLineSegment(sketch, "E827", {"start": v(-1.48, -20.38) * mm, "end": v(-1.42, -20.38) * mm});
            skLineSegment(sketch, "E828", {"start": v(-1.42, -20.38) * mm, "end": v(-1.23, -20.38) * mm});
            skLineSegment(sketch, "E829", {"start": v(-1.23, -20.38) * mm, "end": v(-1.23, -20.78) * mm});
            skLineSegment(sketch, "E830", {"start": v(-1.23, -20.78) * mm, "end": v(-1.5, -20.78) * mm});
            skLineSegment(sketch, "E831", {"start": v(-1.5, -20.78) * mm, "end": v(-1.63, -20.78) * mm});
            skLineSegment(sketch, "E832", {"start": v(-1.63, -20.78) * mm, "end": v(-1.99, -20.58) * mm});
            skLineSegment(sketch, "E833", {"start": v(-1.99, -20.58) * mm, "end": v(-2.14, -20.24) * mm});
            skLineSegment(sketch, "E834", {"start": v(-2.14, -20.24) * mm, "end": v(-2.14, -20.13) * mm});
            skLineSegment(sketch, "E835", {"start": v(-2.14, -20.13) * mm, "end": v(-2.14, -18.85) * mm});
            skLineSegment(sketch, "E836", {"start": v(-2.14, -18.85) * mm, "end": v(-2.4, -18.85) * mm});
            skLineSegment(sketch, "E837", {"start": v(-2.4, -18.85) * mm, "end": v(-2.4, -18.5) * mm});
            skLineSegment(sketch, "E838", {"start": v(-2.4, -18.5) * mm, "end": v(-2.14, -18.5) * mm});
            skLineSegment(sketch, "E839", {"start": v(-2.14, -18.5) * mm, "end": v(-2.14, -17.78) * mm});
            skLineSegment(sketch, "E840", {"start": v(-2.14, -17.78) * mm, "end": v(-1.67, -17.78) * mm});
            skLineSegment(sketch, "E841", {"start": v(-1.67, -17.78) * mm, "end": v(-1.67, -18.5) * mm});
            skLineSegment(sketch, "E842", {"start": v(-1.67, -18.5) * mm, "end": v(-1.23, -18.5) * mm});
            skLineSegment(sketch, "E843", {"start": v(-1.23, -18.5) * mm, "end": v(-1.23, -18.85) * mm});
            skLineSegment(sketch, "E844", {"start": v(-1.3, -13.07) * mm, "end": v(-1.3, -12.56) * mm});
            skLineSegment(sketch, "E845", {"start": v(-1.3, -12.56) * mm, "end": v(-0.67, -12) * mm});
            skLineSegment(sketch, "E846", {"start": v(-0.67, -12) * mm, "end": v(-0.2, -12) * mm});
            skLineSegment(sketch, "E847", {"start": v(-0.2, -12) * mm, "end": v(-0.2, -15.27) * mm});
            skLineSegment(sketch, "E848", {"start": v(-0.2, -15.27) * mm, "end": v(-0.67, -15.27) * mm});
            skLineSegment(sketch, "E849", {"start": v(-0.67, -15.27) * mm, "end": v(-0.67, -12.52) * mm});
            skLineSegment(sketch, "E850", {"start": v(-0.67, -12.52) * mm, "end": v(-1.3, -13.07) * mm});
            skLineSegment(sketch, "E851", {"start": v(1.36, -20.53) * mm, "end": v(1.32, -20.57) * mm});
            skLineSegment(sketch, "E852", {"start": v(1.32, -20.57) * mm, "end": v(0.83, -20.8) * mm});
            skLineSegment(sketch, "E853", {"start": v(0.83, -20.8) * mm, "end": v(0.66, -20.8) * mm});
            skLineSegment(sketch, "E854", {"start": v(0.66, -20.8) * mm, "end": v(0.49, -20.8) * mm});
            skLineSegment(sketch, "E855", {"start": v(0.49, -20.8) * mm, "end": v(0, -20.57) * mm});
            skLineSegment(sketch, "E856", {"start": v(0, -20.57) * mm, "end": v(-0.03, -20.53) * mm});
            skLineSegment(sketch, "E857", {"start": v(-0.03, -20.53) * mm, "end": v(-0.08, -20.47) * mm});
            skLineSegment(sketch, "E858", {"start": v(-0.08, -20.47) * mm, "end": v(-0.25, -20.13) * mm});
            skLineSegment(sketch, "E859", {"start": v(-0.25, -20.13) * mm, "end": v(-0.3, -19.74) * mm});
            skLineSegment(sketch, "E860", {"start": v(-0.3, -19.74) * mm, "end": v(-0.3, -19.61) * mm});
            skLineSegment(sketch, "E861", {"start": v(-0.3, -19.61) * mm, "end": v(-0.3, -19.48) * mm});
            skLineSegment(sketch, "E862", {"start": v(-0.3, -19.48) * mm, "end": v(-0.25, -19.1) * mm});
            skLineSegment(sketch, "E863", {"start": v(-0.25, -19.1) * mm, "end": v(-0.08, -18.75) * mm});
            skLineSegment(sketch, "E864", {"start": v(-0.08, -18.75) * mm, "end": v(-0.03, -18.7) * mm});
            skLineSegment(sketch, "E865", {"start": v(-0.03, -18.7) * mm, "end": v(0, -18.66) * mm});
            skLineSegment(sketch, "E866", {"start": v(0, -18.66) * mm, "end": v(0.5, -18.42) * mm});
            skLineSegment(sketch, "E867", {"start": v(0.5, -18.42) * mm, "end": v(0.66, -18.42) * mm});
            skLineSegment(sketch, "E868", {"start": v(0.66, -18.42) * mm, "end": v(0.84, -18.42) * mm});
            skLineSegment(sketch, "E869", {"start": v(0.84, -18.42) * mm, "end": v(1.32, -18.66) * mm});
            skLineSegment(sketch, "E870", {"start": v(1.32, -18.66) * mm, "end": v(1.36, -18.7) * mm});
            skLineSegment(sketch, "E871", {"start": v(1.36, -18.7) * mm, "end": v(1.42, -18.75) * mm});
            skLineSegment(sketch, "E872", {"start": v(1.42, -18.75) * mm, "end": v(1.58, -19.1) * mm});
            skLineSegment(sketch, "E873", {"start": v(1.58, -19.1) * mm, "end": v(1.64, -19.48) * mm});
            skLineSegment(sketch, "E874", {"start": v(1.64, -19.48) * mm, "end": v(1.64, -19.61) * mm});
            skLineSegment(sketch, "E875", {"start": v(1.64, -19.61) * mm, "end": v(1.64, -19.74) * mm});
            skLineSegment(sketch, "E876", {"start": v(1.64, -19.74) * mm, "end": v(1.58, -20.13) * mm});
            skLineSegment(sketch, "E877", {"start": v(1.58, -20.13) * mm, "end": v(1.42, -20.47) * mm});
            skLineSegment(sketch, "E878", {"start": v(1.42, -20.47) * mm, "end": v(1.36, -20.53) * mm});
            skLineSegment(sketch, "E879", {"start": v(1.29, -14.35) * mm, "end": v(1.29, -14.23) * mm});
            skLineSegment(sketch, "E880", {"start": v(1.29, -14.23) * mm, "end": v(1.42, -13.87) * mm});
            skLineSegment(sketch, "E881", {"start": v(1.42, -13.87) * mm, "end": v(1.68, -13.62) * mm});
            skLineSegment(sketch, "E882", {"start": v(1.68, -13.62) * mm, "end": v(1.74, -13.58) * mm});
            skLineSegment(sketch, "E883", {"start": v(1.74, -13.58) * mm, "end": v(1.68, -13.55) * mm});
            skLineSegment(sketch, "E884", {"start": v(1.68, -13.55) * mm, "end": v(1.46, -13.31) * mm});
            skLineSegment(sketch, "E885", {"start": v(1.46, -13.31) * mm, "end": v(1.34, -13) * mm});
            skLineSegment(sketch, "E886", {"start": v(1.34, -13) * mm, "end": v(1.34, -12.88) * mm});
            skLineSegment(sketch, "E887", {"start": v(1.34, -12.88) * mm, "end": v(1.34, -12.72) * mm});
            skLineSegment(sketch, "E888", {"start": v(1.34, -12.72) * mm, "end": v(1.62, -12.23) * mm});
            skLineSegment(sketch, "E889", {"start": v(1.62, -12.23) * mm, "end": v(2.12, -11.98) * mm});
            skLineSegment(sketch, "E890", {"start": v(2.12, -11.98) * mm, "end": v(2.3, -11.98) * mm});
            skLineSegment(sketch, "E891", {"start": v(2.3, -11.98) * mm, "end": v(2.46, -11.98) * mm});
            skLineSegment(sketch, "E892", {"start": v(2.46, -11.98) * mm, "end": v(2.97, -12.23) * mm});
            skLineSegment(sketch, "E893", {"start": v(2.97, -12.23) * mm, "end": v(3.25, -12.72) * mm});
            skLineSegment(sketch, "E894", {"start": v(3.25, -12.72) * mm, "end": v(3.25, -12.88) * mm});
            skLineSegment(sketch, "E895", {"start": v(3.25, -12.88) * mm, "end": v(3.25, -13) * mm});
            skLineSegment(sketch, "E896", {"start": v(3.25, -13) * mm, "end": v(3.13, -13.31) * mm});
            skLineSegment(sketch, "E897", {"start": v(3.13, -13.31) * mm, "end": v(2.9, -13.55) * mm});
            skLineSegment(sketch, "E898", {"start": v(2.9, -13.55) * mm, "end": v(2.85, -13.58) * mm});
            skLineSegment(sketch, "E899", {"start": v(2.85, -13.58) * mm, "end": v(2.9, -13.62) * mm});
            skLineSegment(sketch, "E900", {"start": v(2.9, -13.62) * mm, "end": v(3.16, -13.87) * mm});
            skLineSegment(sketch, "E901", {"start": v(3.16, -13.87) * mm, "end": v(3.3, -14.23) * mm});
            skLineSegment(sketch, "E902", {"start": v(3.3, -14.23) * mm, "end": v(3.3, -14.35) * mm});
            skLineSegment(sketch, "E903", {"start": v(3.3, -14.35) * mm, "end": v(3.3, -14.52) * mm});
            skLineSegment(sketch, "E904", {"start": v(3.3, -14.52) * mm, "end": v(3, -15.05) * mm});
            skLineSegment(sketch, "E905", {"start": v(3, -15.05) * mm, "end": v(2.47, -15.3) * mm});
            skLineSegment(sketch, "E906", {"start": v(2.47, -15.3) * mm, "end": v(2.3, -15.3) * mm});
            skLineSegment(sketch, "E907", {"start": v(2.3, -15.3) * mm, "end": v(2.11, -15.3) * mm});
            skLineSegment(sketch, "E908", {"start": v(2.11, -15.3) * mm, "end": v(1.58, -15.05) * mm});
            skLineSegment(sketch, "E909", {"start": v(1.58, -15.05) * mm, "end": v(1.29, -14.52) * mm});
            skLineSegment(sketch, "E910", {"start": v(1.29, -14.52) * mm, "end": v(1.29, -14.35) * mm});
            skLineSegment(sketch, "E911", {"start": v(4.28, -20.53) * mm, "end": v(4.24, -20.57) * mm});
            skLineSegment(sketch, "E912", {"start": v(4.24, -20.57) * mm, "end": v(3.75, -20.8) * mm});
            skLineSegment(sketch, "E913", {"start": v(3.75, -20.8) * mm, "end": v(3.58, -20.8) * mm});
            skLineSegment(sketch, "E914", {"start": v(3.58, -20.8) * mm, "end": v(3.41, -20.8) * mm});
            skLineSegment(sketch, "E915", {"start": v(3.41, -20.8) * mm, "end": v(2.93, -20.57) * mm});
            skLineSegment(sketch, "E916", {"start": v(2.93, -20.57) * mm, "end": v(2.9, -20.53) * mm});
            skLineSegment(sketch, "E917", {"start": v(2.9, -20.53) * mm, "end": v(2.84, -20.47) * mm});
            skLineSegment(sketch, "E918", {"start": v(2.84, -20.47) * mm, "end": v(2.67, -20.13) * mm});
            skLineSegment(sketch, "E919", {"start": v(2.67, -20.13) * mm, "end": v(2.62, -19.74) * mm});
            skLineSegment(sketch, "E920", {"start": v(2.62, -19.74) * mm, "end": v(2.62, -19.61) * mm});
            skLineSegment(sketch, "E921", {"start": v(2.62, -19.61) * mm, "end": v(2.62, -19.48) * mm});
            skLineSegment(sketch, "E922", {"start": v(2.62, -19.48) * mm, "end": v(2.67, -19.1) * mm});
            skLineSegment(sketch, "E923", {"start": v(2.67, -19.1) * mm, "end": v(2.84, -18.75) * mm});
            skLineSegment(sketch, "E924", {"start": v(2.84, -18.75) * mm, "end": v(2.9, -18.7) * mm});
            skLineSegment(sketch, "E925", {"start": v(2.9, -18.7) * mm, "end": v(2.93, -18.66) * mm});
            skLineSegment(sketch, "E926", {"start": v(2.93, -18.66) * mm, "end": v(3.42, -18.42) * mm});
            skLineSegment(sketch, "E927", {"start": v(3.42, -18.42) * mm, "end": v(3.58, -18.42) * mm});
            skLineSegment(sketch, "E928", {"start": v(3.58, -18.42) * mm, "end": v(3.76, -18.42) * mm});
            skLineSegment(sketch, "E929", {"start": v(3.76, -18.42) * mm, "end": v(4.24, -18.66) * mm});
            skLineSegment(sketch, "E930", {"start": v(4.24, -18.66) * mm, "end": v(4.28, -18.7) * mm});
            skLineSegment(sketch, "E931", {"start": v(4.28, -18.7) * mm, "end": v(4.34, -18.75) * mm});
            skLineSegment(sketch, "E932", {"start": v(4.34, -18.75) * mm, "end": v(4.5, -19.1) * mm});
            skLineSegment(sketch, "E933", {"start": v(4.5, -19.1) * mm, "end": v(4.56, -19.48) * mm});
            skLineSegment(sketch, "E934", {"start": v(4.56, -19.48) * mm, "end": v(4.56, -19.61) * mm});
            skLineSegment(sketch, "E935", {"start": v(4.56, -19.61) * mm, "end": v(4.56, -19.74) * mm});
            skLineSegment(sketch, "E936", {"start": v(4.56, -19.74) * mm, "end": v(4.5, -20.13) * mm});
            skLineSegment(sketch, "E937", {"start": v(4.5, -20.13) * mm, "end": v(4.34, -20.47) * mm});
            skLineSegment(sketch, "E938", {"start": v(4.34, -20.47) * mm, "end": v(4.28, -20.53) * mm});
            skLineSegment(sketch, "E939", {"start": v(4.2, -14.35) * mm, "end": v(4.2, -14.23) * mm});
            skLineSegment(sketch, "E940", {"start": v(4.2, -14.23) * mm, "end": v(4.33, -13.87) * mm});
            skLineSegment(sketch, "E941", {"start": v(4.33, -13.87) * mm, "end": v(4.58, -13.62) * mm});
            skLineSegment(sketch, "E942", {"start": v(4.58, -13.62) * mm, "end": v(4.64, -13.58) * mm});
            skLineSegment(sketch, "E943", {"start": v(4.64, -13.58) * mm, "end": v(4.59, -13.55) * mm});
            skLineSegment(sketch, "E944", {"start": v(4.59, -13.55) * mm, "end": v(4.36, -13.31) * mm});
            skLineSegment(sketch, "E945", {"start": v(4.36, -13.31) * mm, "end": v(4.24, -13) * mm});
            skLineSegment(sketch, "E946", {"start": v(4.24, -13) * mm, "end": v(4.24, -12.88) * mm});
            skLineSegment(sketch, "E947", {"start": v(4.24, -12.88) * mm, "end": v(4.24, -12.72) * mm});
            skLineSegment(sketch, "E948", {"start": v(4.24, -12.72) * mm, "end": v(4.52, -12.23) * mm});
            skLineSegment(sketch, "E949", {"start": v(4.52, -12.23) * mm, "end": v(5.03, -11.98) * mm});
            skLineSegment(sketch, "E950", {"start": v(5.03, -11.98) * mm, "end": v(5.2, -11.98) * mm});
            skLineSegment(sketch, "E951", {"start": v(5.2, -11.98) * mm, "end": v(5.36, -11.98) * mm});
            skLineSegment(sketch, "E952", {"start": v(5.36, -11.98) * mm, "end": v(5.87, -12.23) * mm});
            skLineSegment(sketch, "E953", {"start": v(5.87, -12.23) * mm, "end": v(6.15, -12.72) * mm});
            skLineSegment(sketch, "E954", {"start": v(6.15, -12.72) * mm, "end": v(6.15, -12.88) * mm});
            skLineSegment(sketch, "E955", {"start": v(6.15, -12.88) * mm, "end": v(6.15, -13) * mm});
            skLineSegment(sketch, "E956", {"start": v(6.15, -13) * mm, "end": v(6.03, -13.31) * mm});
            skLineSegment(sketch, "E957", {"start": v(6.03, -13.31) * mm, "end": v(5.8, -13.55) * mm});
            skLineSegment(sketch, "E958", {"start": v(5.8, -13.55) * mm, "end": v(5.75, -13.58) * mm});
            skLineSegment(sketch, "E959", {"start": v(5.75, -13.58) * mm, "end": v(5.81, -13.62) * mm});
            skLineSegment(sketch, "E960", {"start": v(5.81, -13.62) * mm, "end": v(6.06, -13.87) * mm});
            skLineSegment(sketch, "E961", {"start": v(6.06, -13.87) * mm, "end": v(6.2, -14.23) * mm});
            skLineSegment(sketch, "E962", {"start": v(6.2, -14.23) * mm, "end": v(6.2, -14.35) * mm});
            skLineSegment(sketch, "E963", {"start": v(6.2, -14.35) * mm, "end": v(6.2, -14.52) * mm});
            skLineSegment(sketch, "E964", {"start": v(6.2, -14.52) * mm, "end": v(5.9, -15.05) * mm});
            skLineSegment(sketch, "E965", {"start": v(5.9, -15.05) * mm, "end": v(5.37, -15.3) * mm});
            skLineSegment(sketch, "E966", {"start": v(5.37, -15.3) * mm, "end": v(5.2, -15.3) * mm});
            skLineSegment(sketch, "E967", {"start": v(5.2, -15.3) * mm, "end": v(5.02, -15.3) * mm});
            skLineSegment(sketch, "E968", {"start": v(5.02, -15.3) * mm, "end": v(4.48, -15.05) * mm});
            skLineSegment(sketch, "E969", {"start": v(4.48, -15.05) * mm, "end": v(4.2, -14.52) * mm});
            skLineSegment(sketch, "E970", {"start": v(4.2, -14.52) * mm, "end": v(4.2, -14.35) * mm});
            skLineSegment(sketch, "E971", {"start": v(6.56, -20.78) * mm, "end": v(6.27, -20.78) * mm});
            skLineSegment(sketch, "E972", {"start": v(6.27, -20.78) * mm, "end": v(6.15, -20.78) * mm});
            skLineSegment(sketch, "E973", {"start": v(6.15, -20.78) * mm, "end": v(5.78, -20.58) * mm});
            skLineSegment(sketch, "E974", {"start": v(5.78, -20.58) * mm, "end": v(5.63, -20.24) * mm});
            skLineSegment(sketch, "E975", {"start": v(5.63, -20.24) * mm, "end": v(5.63, -20.13) * mm});
            skLineSegment(sketch, "E976", {"start": v(5.63, -20.13) * mm, "end": v(5.63, -17.5) * mm});
            skLineSegment(sketch, "E977", {"start": v(5.63, -17.5) * mm, "end": v(6.1, -17.5) * mm});
            skLineSegment(sketch, "E978", {"start": v(6.1, -17.5) * mm, "end": v(6.1, -20.1) * mm});
            skLineSegment(sketch, "E979", {"start": v(6.1, -20.1) * mm, "end": v(6.1, -20.17) * mm});
            skLineSegment(sketch, "E980", {"start": v(6.1, -20.17) * mm, "end": v(6.3, -20.38) * mm});
            skLineSegment(sketch, "E981", {"start": v(6.3, -20.38) * mm, "end": v(6.35, -20.38) * mm});
            skLineSegment(sketch, "E982", {"start": v(6.35, -20.38) * mm, "end": v(6.56, -20.38) * mm});
            skLineSegment(sketch, "E983", {"start": v(6.56, -20.38) * mm, "end": v(6.56, -20.78) * mm});
            skLineSegment(sketch, "E984", {"start": v(8.58, 6.29) * mm, "end": v(8.05, 6.34) * mm});
            skLineSegment(sketch, "E985", {"start": v(8.05, 6.34) * mm, "end": v(7.9, 6.35) * mm});
            skLineSegment(sketch, "E986", {"start": v(7.9, 6.35) * mm, "end": v(7.33, 6.6) * mm});
            skLineSegment(sketch, "E987", {"start": v(7.33, 6.6) * mm, "end": v(7.06, 7.15) * mm});
            skLineSegment(sketch, "E988", {"start": v(7.06, 7.15) * mm, "end": v(7.06, 7.33) * mm});
            skLineSegment(sketch, "E989", {"start": v(7.06, 7.33) * mm, "end": v(7.06, 7.45) * mm});
            skLineSegment(sketch, "E990", {"start": v(7.06, 7.45) * mm, "end": v(7.17, 7.82) * mm});
            skLineSegment(sketch, "E991", {"start": v(7.17, 7.82) * mm, "end": v(7.48, 8.18) * mm});
            skLineSegment(sketch, "E992", {"start": v(7.48, 8.18) * mm, "end": v(7.92, 8.39) * mm});
            skLineSegment(sketch, "E993", {"start": v(7.92, 8.39) * mm, "end": v(8.3, 8.46) * mm});
            skLineSegment(sketch, "E994", {"start": v(8.3, 8.46) * mm, "end": v(8.42, 8.46) * mm});
            skLineSegment(sketch, "E995", {"start": v(8.42, 8.46) * mm, "end": v(8.6, 8.46) * mm});
            skLineSegment(sketch, "E996", {"start": v(8.6, 8.46) * mm, "end": v(9.17, 8.37) * mm});
            skLineSegment(sketch, "E997", {"start": v(9.17, 8.37) * mm, "end": v(9.68, 8.12) * mm});
            skLineSegment(sketch, "E998", {"start": v(9.68, 8.12) * mm, "end": v(9.76, 8.04) * mm});
            skLineSegment(sketch, "E999", {"start": v(9.76, 8.04) * mm, "end": v(9.12, 7.4) * mm});
            skLineSegment(sketch, "E1000", {"start": v(9.12, 7.4) * mm, "end": v(9.08, 7.44) * mm});
            skLineSegment(sketch, "E1001", {"start": v(9.08, 7.44) * mm, "end": v(8.8, 7.56) * mm});
            skLineSegment(sketch, "E1002", {"start": v(8.8, 7.56) * mm, "end": v(8.5, 7.6) * mm});
            skLineSegment(sketch, "E1003", {"start": v(8.5, 7.6) * mm, "end": v(8.4, 7.6) * mm});
            skLineSegment(sketch, "E1004", {"start": v(8.4, 7.6) * mm, "end": v(8.33, 7.6) * mm});
            skLineSegment(sketch, "E1005", {"start": v(8.33, 7.6) * mm, "end": v(8.13, 7.53) * mm});
            skLineSegment(sketch, "E1006", {"start": v(8.13, 7.53) * mm, "end": v(8.06, 7.44) * mm});
            skLineSegment(sketch, "E1007", {"start": v(8.06, 7.44) * mm, "end": v(8.06, 7.4) * mm});
            skLineSegment(sketch, "E1008", {"start": v(8.06, 7.4) * mm, "end": v(8.06, 7.38) * mm});
            skLineSegment(sketch, "E1009", {"start": v(8.06, 7.38) * mm, "end": v(8.08, 7.3) * mm});
            skLineSegment(sketch, "E1010", {"start": v(8.08, 7.3) * mm, "end": v(8.23, 7.22) * mm});
            skLineSegment(sketch, "E1011", {"start": v(8.23, 7.22) * mm, "end": v(8.28, 7.21) * mm});
            skLineSegment(sketch, "E1012", {"start": v(8.28, 7.21) * mm, "end": v(8.8, 7.16) * mm});
            skLineSegment(sketch, "E1013", {"start": v(8.8, 7.16) * mm, "end": v(8.99, 7.15) * mm});
            skLineSegment(sketch, "E1014", {"start": v(8.99, 7.15) * mm, "end": v(9.6, 6.82) * mm});
            skLineSegment(sketch, "E1015", {"start": v(9.6, 6.82) * mm, "end": v(9.84, 6.3) * mm});
            skLineSegment(sketch, "E1016", {"start": v(9.84, 6.3) * mm, "end": v(9.84, 6.12) * mm});
            skLineSegment(sketch, "E1017", {"start": v(9.84, 6.12) * mm, "end": v(9.84, 6) * mm});
            skLineSegment(sketch, "E1018", {"start": v(9.84, 6) * mm, "end": v(9.72, 5.6) * mm});
            skLineSegment(sketch, "E1019", {"start": v(9.72, 5.6) * mm, "end": v(9.4, 5.24) * mm});
            skLineSegment(sketch, "E1020", {"start": v(9.4, 5.24) * mm, "end": v(8.92, 5.03) * mm});
            skLineSegment(sketch, "E1021", {"start": v(8.92, 5.03) * mm, "end": v(8.5, 4.96) * mm});
            skLineSegment(sketch, "E1022", {"start": v(8.5, 4.96) * mm, "end": v(8.36, 4.96) * mm});
            skLineSegment(sketch, "E1023", {"start": v(8.36, 4.96) * mm, "end": v(8.17, 4.96) * mm});
            skLineSegment(sketch, "E1024", {"start": v(8.17, 4.96) * mm, "end": v(7.6, 5.04) * mm});
            skLineSegment(sketch, "E1025", {"start": v(7.6, 5.04) * mm, "end": v(6.99, 5.34) * mm});
            skLineSegment(sketch, "E1026", {"start": v(6.99, 5.34) * mm, "end": v(6.87, 5.46) * mm});
            skLineSegment(sketch, "E1027", {"start": v(6.87, 5.46) * mm, "end": v(7.55, 6.13) * mm});
            skLineSegment(sketch, "E1028", {"start": v(7.55, 6.13) * mm, "end": v(7.62, 6.06) * mm});
            skLineSegment(sketch, "E1029", {"start": v(7.62, 6.06) * mm, "end": v(8, 5.88) * mm});
            skLineSegment(sketch, "E1030", {"start": v(8, 5.88) * mm, "end": v(8.28, 5.85) * mm});
            skLineSegment(sketch, "E1031", {"start": v(8.28, 5.85) * mm, "end": v(8.38, 5.85) * mm});
            skLineSegment(sketch, "E1032", {"start": v(8.38, 5.85) * mm, "end": v(8.45, 5.85) * mm});
            skLineSegment(sketch, "E1033", {"start": v(8.45, 5.85) * mm, "end": v(8.66, 5.9) * mm});
            skLineSegment(sketch, "E1034", {"start": v(8.66, 5.9) * mm, "end": v(8.82, 6.02) * mm});
            skLineSegment(sketch, "E1035", {"start": v(8.82, 6.02) * mm, "end": v(8.82, 6.07) * mm});
            skLineSegment(sketch, "E1036", {"start": v(8.82, 6.07) * mm, "end": v(8.82, 6.1) * mm});
            skLineSegment(sketch, "E1037", {"start": v(8.82, 6.1) * mm, "end": v(8.77, 6.2) * mm});
            skLineSegment(sketch, "E1038", {"start": v(8.77, 6.2) * mm, "end": v(8.63, 6.28) * mm});
            skLineSegment(sketch, "E1039", {"start": v(8.63, 6.28) * mm, "end": v(8.58, 6.29) * mm});
            skLineSegment(sketch, "E1040", {"start": v(8.08, -20.78) * mm, "end": v(7.52, -20.78) * mm});
            skLineSegment(sketch, "E1041", {"start": v(7.52, -20.78) * mm, "end": v(7.52, -20.22) * mm});
            skLineSegment(sketch, "E1042", {"start": v(7.52, -20.22) * mm, "end": v(8.08, -20.22) * mm});
            skLineSegment(sketch, "E1043", {"start": v(8.08, -20.22) * mm, "end": v(8.08, -20.78) * mm});
            skLineSegment(sketch, "E1044", {"start": v(8.07, -15.3) * mm, "end": v(7.9, -15.3) * mm});
            skLineSegment(sketch, "E1045", {"start": v(7.9, -15.3) * mm, "end": v(7.38, -15.08) * mm});
            skLineSegment(sketch, "E1046", {"start": v(7.38, -15.08) * mm, "end": v(7.07, -14.55) * mm});
            skLineSegment(sketch, "E1047", {"start": v(7.07, -14.55) * mm, "end": v(7.07, -14.39) * mm});
            skLineSegment(sketch, "E1048", {"start": v(7.07, -14.39) * mm, "end": v(7.54, -14.39) * mm});
            skLineSegment(sketch, "E1049", {"start": v(7.54, -14.39) * mm, "end": v(7.54, -14.47) * mm});
            skLineSegment(sketch, "E1050", {"start": v(7.54, -14.47) * mm, "end": v(7.7, -14.76) * mm});
            skLineSegment(sketch, "E1051", {"start": v(7.7, -14.76) * mm, "end": v(7.98, -14.88) * mm});
            skLineSegment(sketch, "E1052", {"start": v(7.98, -14.88) * mm, "end": v(8.07, -14.88) * mm});
            skLineSegment(sketch, "E1053", {"start": v(8.07, -14.88) * mm, "end": v(8.16, -14.88) * mm});
            skLineSegment(sketch, "E1054", {"start": v(8.16, -14.88) * mm, "end": v(8.45, -14.74) * mm});
            skLineSegment(sketch, "E1055", {"start": v(8.45, -14.74) * mm, "end": v(8.6, -14.44) * mm});
            skLineSegment(sketch, "E1056", {"start": v(8.6, -14.44) * mm, "end": v(8.6, -14.34) * mm});
            skLineSegment(sketch, "E1057", {"start": v(8.6, -14.34) * mm, "end": v(8.6, -14.24) * mm});
            skLineSegment(sketch, "E1058", {"start": v(8.6, -14.24) * mm, "end": v(8.47, -13.95) * mm});
            skLineSegment(sketch, "E1059", {"start": v(8.47, -13.95) * mm, "end": v(8.16, -13.8) * mm});
            skLineSegment(sketch, "E1060", {"start": v(8.16, -13.8) * mm, "end": v(8.06, -13.8) * mm});
            skLineSegment(sketch, "E1061", {"start": v(8.06, -13.8) * mm, "end": v(7.98, -13.8) * mm});
            skLineSegment(sketch, "E1062", {"start": v(7.98, -13.8) * mm, "end": v(7.98, -13.4) * mm});
            skLineSegment(sketch, "E1063", {"start": v(7.98, -13.4) * mm, "end": v(8.06, -13.4) * mm});
            skLineSegment(sketch, "E1064", {"start": v(8.06, -13.4) * mm, "end": v(8.15, -13.4) * mm});
            skLineSegment(sketch, "E1065", {"start": v(8.15, -13.4) * mm, "end": v(8.43, -13.26) * mm});
            skLineSegment(sketch, "E1066", {"start": v(8.43, -13.26) * mm, "end": v(8.55, -13) * mm});
            skLineSegment(sketch, "E1067", {"start": v(8.55, -13) * mm, "end": v(8.55, -12.9) * mm});
            skLineSegment(sketch, "E1068", {"start": v(8.55, -12.9) * mm, "end": v(8.55, -12.8) * mm});
            skLineSegment(sketch, "E1069", {"start": v(8.55, -12.8) * mm, "end": v(8.4, -12.52) * mm});
            skLineSegment(sketch, "E1070", {"start": v(8.4, -12.52) * mm, "end": v(8.15, -12.4) * mm});
            skLineSegment(sketch, "E1071", {"start": v(8.15, -12.4) * mm, "end": v(8.07, -12.4) * mm});
            skLineSegment(sketch, "E1072", {"start": v(8.07, -12.4) * mm, "end": v(7.98, -12.4) * mm});
            skLineSegment(sketch, "E1073", {"start": v(7.98, -12.4) * mm, "end": v(7.73, -12.52) * mm});
            skLineSegment(sketch, "E1074", {"start": v(7.73, -12.52) * mm, "end": v(7.58, -12.8) * mm});
            skLineSegment(sketch, "E1075", {"start": v(7.58, -12.8) * mm, "end": v(7.58, -12.86) * mm});
            skLineSegment(sketch, "E1076", {"start": v(7.58, -12.86) * mm, "end": v(7.11, -12.86) * mm});
            skLineSegment(sketch, "E1077", {"start": v(7.11, -12.86) * mm, "end": v(7.12, -12.72) * mm});
            skLineSegment(sketch, "E1078", {"start": v(7.12, -12.72) * mm, "end": v(7.4, -12.21) * mm});
            skLineSegment(sketch, "E1079", {"start": v(7.4, -12.21) * mm, "end": v(7.9, -11.97) * mm});
            skLineSegment(sketch, "E1080", {"start": v(7.9, -11.97) * mm, "end": v(8.07, -11.97) * mm});
            skLineSegment(sketch, "E1081", {"start": v(8.07, -11.97) * mm, "end": v(8.24, -11.97) * mm});
            skLineSegment(sketch, "E1082", {"start": v(8.24, -11.97) * mm, "end": v(8.75, -12.23) * mm});
            skLineSegment(sketch, "E1083", {"start": v(8.75, -12.23) * mm, "end": v(9.02, -12.72) * mm});
            skLineSegment(sketch, "E1084", {"start": v(9.02, -12.72) * mm, "end": v(9.02, -12.89) * mm});
            skLineSegment(sketch, "E1085", {"start": v(9.02, -12.89) * mm, "end": v(9.02, -13) * mm});
            skLineSegment(sketch, "E1086", {"start": v(9.02, -13) * mm, "end": v(8.9, -13.32) * mm});
            skLineSegment(sketch, "E1087", {"start": v(8.9, -13.32) * mm, "end": v(8.67, -13.55) * mm});
            skLineSegment(sketch, "E1088", {"start": v(8.67, -13.55) * mm, "end": v(8.61, -13.58) * mm});
            skLineSegment(sketch, "E1089", {"start": v(8.61, -13.58) * mm, "end": v(8.68, -13.61) * mm});
            skLineSegment(sketch, "E1090", {"start": v(8.68, -13.61) * mm, "end": v(8.94, -13.86) * mm});
            skLineSegment(sketch, "E1091", {"start": v(8.94, -13.86) * mm, "end": v(9.07, -14.23) * mm});
            skLineSegment(sketch, "E1092", {"start": v(9.07, -14.23) * mm, "end": v(9.07, -14.35) * mm});
            skLineSegment(sketch, "E1093", {"start": v(9.07, -14.35) * mm, "end": v(9.07, -14.53) * mm});
            skLineSegment(sketch, "E1094", {"start": v(9.07, -14.53) * mm, "end": v(8.77, -15.06) * mm});
            skLineSegment(sketch, "E1095", {"start": v(8.77, -15.06) * mm, "end": v(8.24, -15.3) * mm});
            skLineSegment(sketch, "E1096", {"start": v(8.24, -15.3) * mm, "end": v(8.07, -15.3) * mm});
            skLineSegment(sketch, "E1097", {"start": v(9.75, -20.18) * mm, "end": v(9.78, -20.21) * mm});
            skLineSegment(sketch, "E1098", {"start": v(9.78, -20.21) * mm, "end": v(10.08, -20.39) * mm});
            skLineSegment(sketch, "E1099", {"start": v(10.08, -20.39) * mm, "end": v(10.18, -20.39) * mm});
            skLineSegment(sketch, "E1100", {"start": v(10.18, -20.39) * mm, "end": v(10.3, -20.39) * mm});
            skLineSegment(sketch, "E1101", {"start": v(10.3, -20.39) * mm, "end": v(10.6, -20.2) * mm});
            skLineSegment(sketch, "E1102", {"start": v(10.6, -20.2) * mm, "end": v(10.63, -20.16) * mm});
            skLineSegment(sketch, "E1103", {"start": v(10.63, -20.16) * mm, "end": v(10.95, -20.47) * mm});
            skLineSegment(sketch, "E1104", {"start": v(10.95, -20.47) * mm, "end": v(10.9, -20.53) * mm});
            skLineSegment(sketch, "E1105", {"start": v(10.9, -20.53) * mm, "end": v(10.36, -20.8) * mm});
            skLineSegment(sketch, "E1106", {"start": v(10.36, -20.8) * mm, "end": v(10.18, -20.8) * mm});
            skLineSegment(sketch, "E1107", {"start": v(10.18, -20.8) * mm, "end": v(10.09, -20.8) * mm});
            skLineSegment(sketch, "E1108", {"start": v(10.09, -20.8) * mm, "end": v(9.8, -20.74) * mm});
            skLineSegment(sketch, "E1109", {"start": v(9.8, -20.74) * mm, "end": v(9.47, -20.53) * mm});
            skLineSegment(sketch, "E1110", {"start": v(9.47, -20.53) * mm, "end": v(9.24, -20.16) * mm});
            skLineSegment(sketch, "E1111", {"start": v(9.24, -20.16) * mm, "end": v(9.15, -19.75) * mm});
            skLineSegment(sketch, "E1112", {"start": v(9.15, -19.75) * mm, "end": v(9.15, -19.61) * mm});
            skLineSegment(sketch, "E1113", {"start": v(9.15, -19.61) * mm, "end": v(9.15, -19.47) * mm});
            skLineSegment(sketch, "E1114", {"start": v(9.15, -19.47) * mm, "end": v(9.24, -19.06) * mm});
            skLineSegment(sketch, "E1115", {"start": v(9.24, -19.06) * mm, "end": v(9.47, -18.69) * mm});
            skLineSegment(sketch, "E1116", {"start": v(9.47, -18.69) * mm, "end": v(9.8, -18.48) * mm});
            skLineSegment(sketch, "E1117", {"start": v(9.8, -18.48) * mm, "end": v(10.09, -18.42) * mm});
            skLineSegment(sketch, "E1118", {"start": v(10.09, -18.42) * mm, "end": v(10.18, -18.42) * mm});
            skLineSegment(sketch, "E1119", {"start": v(10.18, -18.42) * mm, "end": v(10.29, -18.42) * mm});
            skLineSegment(sketch, "E1120", {"start": v(10.29, -18.42) * mm, "end": v(10.6, -18.5) * mm});
            skLineSegment(sketch, "E1121", {"start": v(10.6, -18.5) * mm, "end": v(10.9, -18.69) * mm});
            skLineSegment(sketch, "E1122", {"start": v(10.9, -18.69) * mm, "end": v(10.95, -18.75) * mm});
            skLineSegment(sketch, "E1123", {"start": v(10.95, -18.75) * mm, "end": v(10.63, -19.06) * mm});
            skLineSegment(sketch, "E1124", {"start": v(10.63, -19.06) * mm, "end": v(10.6, -19.02) * mm});
            skLineSegment(sketch, "E1125", {"start": v(10.6, -19.02) * mm, "end": v(10.29, -18.84) * mm});
            skLineSegment(sketch, "E1126", {"start": v(10.29, -18.84) * mm, "end": v(10.18, -18.84) * mm});
            skLineSegment(sketch, "E1127", {"start": v(10.18, -18.84) * mm, "end": v(10.08, -18.84) * mm});
            skLineSegment(sketch, "E1128", {"start": v(10.08, -18.84) * mm, "end": v(9.78, -19.01) * mm});
            skLineSegment(sketch, "E1129", {"start": v(9.78, -19.01) * mm, "end": v(9.75, -19.05) * mm});
            skLineSegment(sketch, "E1130", {"start": v(9.75, -19.05) * mm, "end": v(9.73, -19.08) * mm});
            skLineSegment(sketch, "E1131", {"start": v(9.73, -19.08) * mm, "end": v(9.61, -19.48) * mm});
            skLineSegment(sketch, "E1132", {"start": v(9.61, -19.48) * mm, "end": v(9.61, -19.61) * mm});
            skLineSegment(sketch, "E1133", {"start": v(9.61, -19.61) * mm, "end": v(9.61, -19.75) * mm});
            skLineSegment(sketch, "E1134", {"start": v(9.61, -19.75) * mm, "end": v(9.73, -20.15) * mm});
            skLineSegment(sketch, "E1135", {"start": v(9.73, -20.15) * mm, "end": v(9.75, -20.18) * mm});
            skLineSegment(sketch, "E1136", {"start": v(13.43, -20.53) * mm, "end": v(13.39, -20.57) * mm});
            skLineSegment(sketch, "E1137", {"start": v(13.39, -20.57) * mm, "end": v(12.9, -20.8) * mm});
            skLineSegment(sketch, "E1138", {"start": v(12.9, -20.8) * mm, "end": v(12.73, -20.8) * mm});
            skLineSegment(sketch, "E1139", {"start": v(12.73, -20.8) * mm, "end": v(12.56, -20.8) * mm});
            skLineSegment(sketch, "E1140", {"start": v(12.56, -20.8) * mm, "end": v(12.07, -20.57) * mm});
            skLineSegment(sketch, "E1141", {"start": v(12.07, -20.57) * mm, "end": v(12.04, -20.53) * mm});
            skLineSegment(sketch, "E1142", {"start": v(12.04, -20.53) * mm, "end": v(11.98, -20.47) * mm});
            skLineSegment(sketch, "E1143", {"start": v(11.98, -20.47) * mm, "end": v(11.82, -20.13) * mm});
            skLineSegment(sketch, "E1144", {"start": v(11.82, -20.13) * mm, "end": v(11.76, -19.74) * mm});
            skLineSegment(sketch, "E1145", {"start": v(11.76, -19.74) * mm, "end": v(11.76, -19.61) * mm});
            skLineSegment(sketch, "E1146", {"start": v(11.76, -19.61) * mm, "end": v(11.76, -19.48) * mm});
            skLineSegment(sketch, "E1147", {"start": v(11.76, -19.48) * mm, "end": v(11.82, -19.1) * mm});
            skLineSegment(sketch, "E1148", {"start": v(11.82, -19.1) * mm, "end": v(11.98, -18.75) * mm});
            skLineSegment(sketch, "E1149", {"start": v(11.98, -18.75) * mm, "end": v(12.04, -18.7) * mm});
            skLineSegment(sketch, "E1150", {"start": v(12.04, -18.7) * mm, "end": v(12.07, -18.66) * mm});
            skLineSegment(sketch, "E1151", {"start": v(12.07, -18.66) * mm, "end": v(12.57, -18.42) * mm});
            skLineSegment(sketch, "E1152", {"start": v(12.57, -18.42) * mm, "end": v(12.73, -18.42) * mm});
            skLineSegment(sketch, "E1153", {"start": v(12.73, -18.42) * mm, "end": v(12.9, -18.42) * mm});
            skLineSegment(sketch, "E1154", {"start": v(12.9, -18.42) * mm, "end": v(13.39, -18.66) * mm});
            skLineSegment(sketch, "E1155", {"start": v(13.39, -18.66) * mm, "end": v(13.43, -18.7) * mm});
            skLineSegment(sketch, "E1156", {"start": v(13.43, -18.7) * mm, "end": v(13.48, -18.75) * mm});
            skLineSegment(sketch, "E1157", {"start": v(13.48, -18.75) * mm, "end": v(13.65, -19.1) * mm});
            skLineSegment(sketch, "E1158", {"start": v(13.65, -19.1) * mm, "end": v(13.7, -19.48) * mm});
            skLineSegment(sketch, "E1159", {"start": v(13.7, -19.48) * mm, "end": v(13.7, -19.61) * mm});
            skLineSegment(sketch, "E1160", {"start": v(13.7, -19.61) * mm, "end": v(13.7, -19.74) * mm});
            skLineSegment(sketch, "E1161", {"start": v(13.7, -19.74) * mm, "end": v(13.65, -20.13) * mm});
            skLineSegment(sketch, "E1162", {"start": v(13.65, -20.13) * mm, "end": v(13.48, -20.47) * mm});
            skLineSegment(sketch, "E1163", {"start": v(13.48, -20.47) * mm, "end": v(13.43, -20.53) * mm});
            skLineSegment(sketch, "E1164", {"start": v(13.92, 5) * mm, "end": v(12.88, 5) * mm});
            skLineSegment(sketch, "E1165", {"start": v(12.88, 5) * mm, "end": v(12.88, 7.07) * mm});
            skLineSegment(sketch, "E1166", {"start": v(12.88, 7.07) * mm, "end": v(12.88, 7.16) * mm});
            skLineSegment(sketch, "E1167", {"start": v(12.88, 7.16) * mm, "end": v(12.73, 7.43) * mm});
            skLineSegment(sketch, "E1168", {"start": v(12.73, 7.43) * mm, "end": v(12.54, 7.52) * mm});
            skLineSegment(sketch, "E1169", {"start": v(12.54, 7.52) * mm, "end": v(12.48, 7.52) * mm});
            skLineSegment(sketch, "E1170", {"start": v(12.48, 7.52) * mm, "end": v(12.42, 7.52) * mm});
            skLineSegment(sketch, "E1171", {"start": v(12.42, 7.52) * mm, "end": v(12.23, 7.43) * mm});
            skLineSegment(sketch, "E1172", {"start": v(12.23, 7.43) * mm, "end": v(12.08, 7.16) * mm});
            skLineSegment(sketch, "E1173", {"start": v(12.08, 7.16) * mm, "end": v(12.08, 7.07) * mm});
            skLineSegment(sketch, "E1174", {"start": v(12.08, 7.07) * mm, "end": v(12.08, 5) * mm});
            skLineSegment(sketch, "E1175", {"start": v(12.08, 5) * mm, "end": v(11.04, 5) * mm});
            skLineSegment(sketch, "E1176", {"start": v(11.04, 5) * mm, "end": v(11.04, 9.52) * mm});
            skLineSegment(sketch, "E1177", {"start": v(11.04, 9.52) * mm, "end": v(12.08, 9.52) * mm});
            skLineSegment(sketch, "E1178", {"start": v(12.08, 9.52) * mm, "end": v(12.08, 8.14) * mm});
            skLineSegment(sketch, "E1179", {"start": v(12.08, 8.14) * mm, "end": v(12.13, 8.2) * mm});
            skLineSegment(sketch, "E1180", {"start": v(12.13, 8.2) * mm, "end": v(12.65, 8.46) * mm});
            skLineSegment(sketch, "E1181", {"start": v(12.65, 8.46) * mm, "end": v(12.83, 8.46) * mm});
            skLineSegment(sketch, "E1182", {"start": v(12.83, 8.46) * mm, "end": v(13.03, 8.46) * mm});
            skLineSegment(sketch, "E1183", {"start": v(13.03, 8.46) * mm, "end": v(13.65, 8.1) * mm});
            skLineSegment(sketch, "E1184", {"start": v(13.65, 8.1) * mm, "end": v(13.92, 7.44) * mm});
            skLineSegment(sketch, "E1185", {"start": v(13.92, 7.44) * mm, "end": v(13.92, 7.22) * mm});
            skLineSegment(sketch, "E1186", {"start": v(13.92, 7.22) * mm, "end": v(13.92, 5) * mm});
            skLineSegment(sketch, "E1187", {"start": v(18.1, -20.78) * mm, "end": v(17.63, -20.78) * mm});
            skLineSegment(sketch, "E1188", {"start": v(17.63, -20.78) * mm, "end": v(17.63, -19.36) * mm});
            skLineSegment(sketch, "E1189", {"start": v(17.63, -19.36) * mm, "end": v(17.63, -19.26) * mm});
            skLineSegment(sketch, "E1190", {"start": v(17.63, -19.26) * mm, "end": v(17.5, -18.96) * mm});
            skLineSegment(sketch, "E1191", {"start": v(17.5, -18.96) * mm, "end": v(17.24, -18.84) * mm});
            skLineSegment(sketch, "E1192", {"start": v(17.24, -18.84) * mm, "end": v(17.16, -18.84) * mm});
            skLineSegment(sketch, "E1193", {"start": v(17.16, -18.84) * mm, "end": v(17.08, -18.84) * mm});
            skLineSegment(sketch, "E1194", {"start": v(17.08, -18.84) * mm, "end": v(16.82, -18.96) * mm});
            skLineSegment(sketch, "E1195", {"start": v(16.82, -18.96) * mm, "end": v(16.68, -19.24) * mm});
            skLineSegment(sketch, "E1196", {"start": v(16.68, -19.24) * mm, "end": v(16.68, -19.34) * mm});
            skLineSegment(sketch, "E1197", {"start": v(16.68, -19.34) * mm, "end": v(16.68, -20.78) * mm});
            skLineSegment(sketch, "E1198", {"start": v(16.68, -20.78) * mm, "end": v(16.2, -20.78) * mm});
            skLineSegment(sketch, "E1199", {"start": v(16.2, -20.78) * mm, "end": v(16.2, -19.36) * mm});
            skLineSegment(sketch, "E1200", {"start": v(16.2, -19.36) * mm, "end": v(16.2, -19.26) * mm});
            skLineSegment(sketch, "E1201", {"start": v(16.2, -19.26) * mm, "end": v(16.07, -18.96) * mm});
            skLineSegment(sketch, "E1202", {"start": v(16.07, -18.96) * mm, "end": v(15.82, -18.84) * mm});
            skLineSegment(sketch, "E1203", {"start": v(15.82, -18.84) * mm, "end": v(15.74, -18.84) * mm});
            skLineSegment(sketch, "E1204", {"start": v(15.74, -18.84) * mm, "end": v(15.66, -18.84) * mm});
            skLineSegment(sketch, "E1205", {"start": v(15.66, -18.84) * mm, "end": v(15.4, -18.96) * mm});
            skLineSegment(sketch, "E1206", {"start": v(15.4, -18.96) * mm, "end": v(15.26, -19.26) * mm});
            skLineSegment(sketch, "E1207", {"start": v(15.26, -19.26) * mm, "end": v(15.26, -19.36) * mm});
            skLineSegment(sketch, "E1208", {"start": v(15.26, -19.36) * mm, "end": v(15.26, -20.78) * mm});
            skLineSegment(sketch, "E1209", {"start": v(15.26, -20.78) * mm, "end": v(14.8, -20.78) * mm});
            skLineSegment(sketch, "E1210", {"start": v(14.8, -20.78) * mm, "end": v(14.8, -18.45) * mm});
            skLineSegment(sketch, "E1211", {"start": v(14.8, -18.45) * mm, "end": v(15.25, -18.45) * mm});
            skLineSegment(sketch, "E1212", {"start": v(15.25, -18.45) * mm, "end": v(15.25, -18.68) * mm});
            skLineSegment(sketch, "E1213", {"start": v(15.25, -18.68) * mm, "end": v(15.29, -18.64) * mm});
            skLineSegment(sketch, "E1214", {"start": v(15.29, -18.64) * mm, "end": v(15.72, -18.42) * mm});
            skLineSegment(sketch, "E1215", {"start": v(15.72, -18.42) * mm, "end": v(15.87, -18.42) * mm});
            skLineSegment(sketch, "E1216", {"start": v(15.87, -18.42) * mm, "end": v(16.03, -18.42) * mm});
            skLineSegment(sketch, "E1217", {"start": v(16.03, -18.42) * mm, "end": v(16.5, -18.7) * mm});
            skLineSegment(sketch, "E1218", {"start": v(16.5, -18.7) * mm, "end": v(16.53, -18.76) * mm});
            skLineSegment(sketch, "E1219", {"start": v(16.53, -18.76) * mm, "end": v(16.58, -18.7) * mm});
            skLineSegment(sketch, "E1220", {"start": v(16.58, -18.7) * mm, "end": v(17.09, -18.42) * mm});
            skLineSegment(sketch, "E1221", {"start": v(17.09, -18.42) * mm, "end": v(17.26, -18.42) * mm});
            skLineSegment(sketch, "E1222", {"start": v(17.26, -18.42) * mm, "end": v(17.4, -18.42) * mm});
            skLineSegment(sketch, "E1223", {"start": v(17.4, -18.42) * mm, "end": v(17.81, -18.6) * mm});
            skLineSegment(sketch, "E1224", {"start": v(17.81, -18.6) * mm, "end": v(17.85, -18.63) * mm});
            skLineSegment(sketch, "E1225", {"start": v(17.85, -18.63) * mm, "end": v(17.9, -18.68) * mm});
            skLineSegment(sketch, "E1226", {"start": v(17.9, -18.68) * mm, "end": v(18.1, -19.14) * mm});
            skLineSegment(sketch, "E1227", {"start": v(18.1, -19.14) * mm, "end": v(18.1, -19.29) * mm});
            skLineSegment(sketch, "E1228", {"start": v(18.1, -19.29) * mm, "end": v(18.1, -20.78) * mm});
            skLineSegment(sketch, "E1229", {"start": v(18.23, 6.37) * mm, "end": v(16.18, 6.37) * mm});
            skLineSegment(sketch, "E1230", {"start": v(16.18, 6.37) * mm, "end": v(16.18, 6.28) * mm});
            skLineSegment(sketch, "E1231", {"start": v(16.18, 6.28) * mm, "end": v(16.34, 6) * mm});
            skLineSegment(sketch, "E1232", {"start": v(16.34, 6) * mm, "end": v(16.67, 5.84) * mm});
            skLineSegment(sketch, "E1233", {"start": v(16.67, 5.84) * mm, "end": v(16.78, 5.84) * mm});
            skLineSegment(sketch, "E1234", {"start": v(16.78, 5.84) * mm, "end": v(16.89, 5.84) * mm});
            skLineSegment(sketch, "E1235", {"start": v(16.89, 5.84) * mm, "end": v(17.2, 5.91) * mm});
            skLineSegment(sketch, "E1236", {"start": v(17.2, 5.91) * mm, "end": v(17.44, 6.08) * mm});
            skLineSegment(sketch, "E1237", {"start": v(17.44, 6.08) * mm, "end": v(17.5, 6.13) * mm});
            skLineSegment(sketch, "E1238", {"start": v(17.5, 6.13) * mm, "end": v(18.11, 5.5) * mm});
            skLineSegment(sketch, "E1239", {"start": v(18.11, 5.5) * mm, "end": v(18.02, 5.42) * mm});
            skLineSegment(sketch, "E1240", {"start": v(18.02, 5.42) * mm, "end": v(17.55, 5.1) * mm});
            skLineSegment(sketch, "E1241", {"start": v(17.55, 5.1) * mm, "end": v(16.98, 4.96) * mm});
            skLineSegment(sketch, "E1242", {"start": v(16.98, 4.96) * mm, "end": v(16.78, 4.96) * mm});
            skLineSegment(sketch, "E1243", {"start": v(16.78, 4.96) * mm, "end": v(16.64, 4.96) * mm});
            skLineSegment(sketch, "E1244", {"start": v(16.64, 4.96) * mm, "end": v(16.21, 5.03) * mm});
            skLineSegment(sketch, "E1245", {"start": v(16.21, 5.03) * mm, "end": v(15.69, 5.28) * mm});
            skLineSegment(sketch, "E1246", {"start": v(15.69, 5.28) * mm, "end": v(15.3, 5.82) * mm});
            skLineSegment(sketch, "E1247", {"start": v(15.3, 5.82) * mm, "end": v(15.16, 6.49) * mm});
            skLineSegment(sketch, "E1248", {"start": v(15.16, 6.49) * mm, "end": v(15.16, 6.71) * mm});
            skLineSegment(sketch, "E1249", {"start": v(15.16, 6.71) * mm, "end": v(15.16, 6.9) * mm});
            skLineSegment(sketch, "E1250", {"start": v(15.16, 6.9) * mm, "end": v(15.27, 7.46) * mm});
            skLineSegment(sketch, "E1251", {"start": v(15.27, 7.46) * mm, "end": v(15.59, 8) * mm});
            skLineSegment(sketch, "E1252", {"start": v(15.59, 8) * mm, "end": v(16.07, 8.34) * mm});
            skLineSegment(sketch, "E1253", {"start": v(16.07, 8.34) * mm, "end": v(16.54, 8.46) * mm});
            skLineSegment(sketch, "E1254", {"start": v(16.54, 8.46) * mm, "end": v(16.69, 8.46) * mm});
            skLineSegment(sketch, "E1255", {"start": v(16.69, 8.46) * mm, "end": v(16.85, 8.46) * mm});
            skLineSegment(sketch, "E1256", {"start": v(16.85, 8.46) * mm, "end": v(17.35, 8.33) * mm});
            skLineSegment(sketch, "E1257", {"start": v(17.35, 8.33) * mm, "end": v(17.83, 7.98) * mm});
            skLineSegment(sketch, "E1258", {"start": v(17.83, 7.98) * mm, "end": v(18.13, 7.47) * mm});
            skLineSegment(sketch, "E1259", {"start": v(18.13, 7.47) * mm, "end": v(18.23, 7) * mm});
            skLineSegment(sketch, "E1260", {"start": v(18.23, 7) * mm, "end": v(18.23, 6.84) * mm});
            skLineSegment(sketch, "E1261", {"start": v(18.23, 6.84) * mm, "end": v(18.23, 6.37) * mm});
            skLineSegment(sketch, "E1262", {"start": v(21.33, 7.34) * mm, "end": v(21.3, 7.37) * mm});
            skLineSegment(sketch, "E1263", {"start": v(21.3, 7.37) * mm, "end": v(21.04, 7.52) * mm});
            skLineSegment(sketch, "E1264", {"start": v(21.04, 7.52) * mm, "end": v(20.96, 7.52) * mm});
            skLineSegment(sketch, "E1265", {"start": v(20.96, 7.52) * mm, "end": v(20.9, 7.52) * mm});
            skLineSegment(sketch, "E1266", {"start": v(20.9, 7.52) * mm, "end": v(20.7, 7.43) * mm});
            skLineSegment(sketch, "E1267", {"start": v(20.7, 7.43) * mm, "end": v(20.54, 7.14) * mm});
            skLineSegment(sketch, "E1268", {"start": v(20.54, 7.14) * mm, "end": v(20.54, 7.05) * mm});
            skLineSegment(sketch, "E1269", {"start": v(20.54, 7.05) * mm, "end": v(20.54, 5) * mm});
            skLineSegment(sketch, "E1270", {"start": v(20.54, 5) * mm, "end": v(19.5, 5) * mm});
            skLineSegment(sketch, "E1271", {"start": v(19.5, 5) * mm, "end": v(19.5, 8.42) * mm});
            skLineSegment(sketch, "E1272", {"start": v(19.5, 8.42) * mm, "end": v(20.51, 8.42) * mm});
            skLineSegment(sketch, "E1273", {"start": v(20.51, 8.42) * mm, "end": v(20.51, 8.14) * mm});
            skLineSegment(sketch, "E1274", {"start": v(20.51, 8.14) * mm, "end": v(20.55, 8.18) * mm});
            skLineSegment(sketch, "E1275", {"start": v(20.55, 8.18) * mm, "end": v(20.84, 8.36) * mm});
            skLineSegment(sketch, "E1276", {"start": v(20.84, 8.36) * mm, "end": v(21.2, 8.46) * mm});
            skLineSegment(sketch, "E1277", {"start": v(21.2, 8.46) * mm, "end": v(21.32, 8.46) * mm});
            skLineSegment(sketch, "E1278", {"start": v(21.32, 8.46) * mm, "end": v(21.43, 8.46) * mm});
            skLineSegment(sketch, "E1279", {"start": v(21.43, 8.46) * mm, "end": v(21.76, 8.39) * mm});
            skLineSegment(sketch, "E1280", {"start": v(21.76, 8.39) * mm, "end": v(22.06, 8.2) * mm});
            skLineSegment(sketch, "E1281", {"start": v(22.06, 8.2) * mm, "end": v(22.12, 8.14) * mm});
            skLineSegment(sketch, "E1282", {"start": v(22.12, 8.14) * mm, "end": v(21.33, 7.34) * mm});
            skLineSegment(sketch, "E1283", {"start": v(-7.9, -0.44) * mm, "end": v(-7.78, -0.44) * mm});
            skLineSegment(sketch, "E1284", {"start": v(-7.78, -0.44) * mm, "end": v(-7.47, -0.2) * mm});
            skLineSegment(sketch, "E1285", {"start": v(-7.47, -0.2) * mm, "end": v(-7.38, 0.21) * mm});
            skLineSegment(sketch, "E1286", {"start": v(-7.38, 0.21) * mm, "end": v(-7.38, 0.35) * mm});
            skLineSegment(sketch, "E1287", {"start": v(-7.38, 0.35) * mm, "end": v(-7.38, 0.48) * mm});
            skLineSegment(sketch, "E1288", {"start": v(-7.38, 0.48) * mm, "end": v(-7.47, 0.89) * mm});
            skLineSegment(sketch, "E1289", {"start": v(-7.47, 0.89) * mm, "end": v(-7.78, 1.13) * mm});
            skLineSegment(sketch, "E1290", {"start": v(-7.78, 1.13) * mm, "end": v(-7.9, 1.13) * mm});
            skLineSegment(sketch, "E1291", {"start": v(-7.9, 1.13) * mm, "end": v(-8, 1.13) * mm});
            skLineSegment(sketch, "E1292", {"start": v(-8, 1.13) * mm, "end": v(-8.32, 0.89) * mm});
            skLineSegment(sketch, "E1293", {"start": v(-8.32, 0.89) * mm, "end": v(-8.4, 0.48) * mm});
            skLineSegment(sketch, "E1294", {"start": v(-8.4, 0.48) * mm, "end": v(-8.4, 0.35) * mm});
            skLineSegment(sketch, "E1295", {"start": v(-8.4, 0.35) * mm, "end": v(-8.4, 0.21) * mm});
            skLineSegment(sketch, "E1296", {"start": v(-8.4, 0.21) * mm, "end": v(-8.32, -0.2) * mm});
            skLineSegment(sketch, "E1297", {"start": v(-8.32, -0.2) * mm, "end": v(-8, -0.44) * mm});
            skLineSegment(sketch, "E1298", {"start": v(-8, -0.44) * mm, "end": v(-7.9, -0.44) * mm});
            skLineSegment(sketch, "E1299", {"start": v(12.73, -18.84) * mm, "end": v(12.64, -18.84) * mm});
            skLineSegment(sketch, "E1300", {"start": v(12.64, -18.84) * mm, "end": v(12.41, -18.95) * mm});
            skLineSegment(sketch, "E1301", {"start": v(12.41, -18.95) * mm, "end": v(12.39, -18.97) * mm});
            skLineSegment(sketch, "E1302", {"start": v(12.39, -18.97) * mm, "end": v(12.35, -19) * mm});
            skLineSegment(sketch, "E1303", {"start": v(12.35, -19) * mm, "end": v(12.23, -19.46) * mm});
            skLineSegment(sketch, "E1304", {"start": v(12.23, -19.46) * mm, "end": v(12.23, -19.61) * mm});
            skLineSegment(sketch, "E1305", {"start": v(12.23, -19.61) * mm, "end": v(12.23, -19.77) * mm});
            skLineSegment(sketch, "E1306", {"start": v(12.23, -19.77) * mm, "end": v(12.35, -20.21) * mm});
            skLineSegment(sketch, "E1307", {"start": v(12.35, -20.21) * mm, "end": v(12.39, -20.25) * mm});
            skLineSegment(sketch, "E1308", {"start": v(12.39, -20.25) * mm, "end": v(12.41, -20.27) * mm});
            skLineSegment(sketch, "E1309", {"start": v(12.41, -20.27) * mm, "end": v(12.65, -20.39) * mm});
            skLineSegment(sketch, "E1310", {"start": v(12.65, -20.39) * mm, "end": v(12.73, -20.39) * mm});
            skLineSegment(sketch, "E1311", {"start": v(12.73, -20.39) * mm, "end": v(12.81, -20.39) * mm});
            skLineSegment(sketch, "E1312", {"start": v(12.81, -20.39) * mm, "end": v(13.05, -20.27) * mm});
            skLineSegment(sketch, "E1313", {"start": v(13.05, -20.27) * mm, "end": v(13.07, -20.25) * mm});
            skLineSegment(sketch, "E1314", {"start": v(13.07, -20.25) * mm, "end": v(13.1, -20.21) * mm});
            skLineSegment(sketch, "E1315", {"start": v(13.1, -20.21) * mm, "end": v(13.23, -19.76) * mm});
            skLineSegment(sketch, "E1316", {"start": v(13.23, -19.76) * mm, "end": v(13.23, -19.61) * mm});
            skLineSegment(sketch, "E1317", {"start": v(13.23, -19.61) * mm, "end": v(13.23, -19.45) * mm});
            skLineSegment(sketch, "E1318", {"start": v(13.23, -19.45) * mm, "end": v(13.1, -19) * mm});
            skLineSegment(sketch, "E1319", {"start": v(13.1, -19) * mm, "end": v(13.07, -18.97) * mm});
            skLineSegment(sketch, "E1320", {"start": v(13.07, -18.97) * mm, "end": v(13.05, -18.95) * mm});
            skLineSegment(sketch, "E1321", {"start": v(13.05, -18.95) * mm, "end": v(12.8, -18.84) * mm});
            skLineSegment(sketch, "E1322", {"start": v(12.8, -18.84) * mm, "end": v(12.73, -18.84) * mm});
            skLineSegment(sketch, "E1323", {"start": v(-16.5, -0.2) * mm, "end": v(-16.5, -0.27) * mm});
            skLineSegment(sketch, "E1324", {"start": v(-16.5, -0.27) * mm, "end": v(-16.4, -0.47) * mm});
            skLineSegment(sketch, "E1325", {"start": v(-16.4, -0.47) * mm, "end": v(-16.13, -0.56) * mm});
            skLineSegment(sketch, "E1326", {"start": v(-16.13, -0.56) * mm, "end": v(-16.04, -0.56) * mm});
            skLineSegment(sketch, "E1327", {"start": v(-16.04, -0.56) * mm, "end": v(-15.93, -0.56) * mm});
            skLineSegment(sketch, "E1328", {"start": v(-15.93, -0.56) * mm, "end": v(-15.61, -0.45) * mm});
            skLineSegment(sketch, "E1329", {"start": v(-15.61, -0.45) * mm, "end": v(-15.58, -0.42) * mm});
            skLineSegment(sketch, "E1330", {"start": v(-15.58, -0.42) * mm, "end": v(-15.56, -0.4) * mm});
            skLineSegment(sketch, "E1331", {"start": v(-15.56, -0.4) * mm, "end": v(-15.47, -0.14) * mm});
            skLineSegment(sketch, "E1332", {"start": v(-15.47, -0.14) * mm, "end": v(-15.47, -0.05) * mm});
            skLineSegment(sketch, "E1333", {"start": v(-15.47, -0.05) * mm, "end": v(-15.47, 0.15) * mm});
            skLineSegment(sketch, "E1334", {"start": v(-15.47, 0.15) * mm, "end": v(-16.06, 0.15) * mm});
            skLineSegment(sketch, "E1335", {"start": v(-16.06, 0.15) * mm, "end": v(-16.14, 0.15) * mm});
            skLineSegment(sketch, "E1336", {"start": v(-16.14, 0.15) * mm, "end": v(-16.4, 0.06) * mm});
            skLineSegment(sketch, "E1337", {"start": v(-16.4, 0.06) * mm, "end": v(-16.5, -0.14) * mm});
            skLineSegment(sketch, "E1338", {"start": v(-16.5, -0.14) * mm, "end": v(-16.5, -0.2) * mm});
            skLineSegment(sketch, "E1339", {"start": v(-8.62, -13.75) * mm, "end": v(-8.7, -13.75) * mm});
            skLineSegment(sketch, "E1340", {"start": v(-8.7, -13.75) * mm, "end": v(-8.98, -13.9) * mm});
            skLineSegment(sketch, "E1341", {"start": v(-8.98, -13.9) * mm, "end": v(-9.11, -14.2) * mm});
            skLineSegment(sketch, "E1342", {"start": v(-9.11, -14.2) * mm, "end": v(-9.11, -14.31) * mm});
            skLineSegment(sketch, "E1343", {"start": v(-9.11, -14.31) * mm, "end": v(-9.11, -14.42) * mm});
            skLineSegment(sketch, "E1344", {"start": v(-9.11, -14.42) * mm, "end": v(-8.98, -14.73) * mm});
            skLineSegment(sketch, "E1345", {"start": v(-8.98, -14.73) * mm, "end": v(-8.7, -14.88) * mm});
            skLineSegment(sketch, "E1346", {"start": v(-8.7, -14.88) * mm, "end": v(-8.62, -14.88) * mm});
            skLineSegment(sketch, "E1347", {"start": v(-8.62, -14.88) * mm, "end": v(-8.53, -14.88) * mm});
            skLineSegment(sketch, "E1348", {"start": v(-8.53, -14.88) * mm, "end": v(-8.26, -14.73) * mm});
            skLineSegment(sketch, "E1349", {"start": v(-8.26, -14.73) * mm, "end": v(-8.12, -14.42) * mm});
            skLineSegment(sketch, "E1350", {"start": v(-8.12, -14.42) * mm, "end": v(-8.12, -14.31) * mm});
            skLineSegment(sketch, "E1351", {"start": v(-8.12, -14.31) * mm, "end": v(-8.12, -14.21) * mm});
            skLineSegment(sketch, "E1352", {"start": v(-8.12, -14.21) * mm, "end": v(-8.25, -13.91) * mm});
            skLineSegment(sketch, "E1353", {"start": v(-8.25, -13.91) * mm, "end": v(-8.53, -13.75) * mm});
            skLineSegment(sketch, "E1354", {"start": v(-8.53, -13.75) * mm, "end": v(-8.62, -13.75) * mm});
            skLineSegment(sketch, "E1355", {"start": v(-16.63, -13.8) * mm, "end": v(-16.72, -13.8) * mm});
            skLineSegment(sketch, "E1356", {"start": v(-16.72, -13.8) * mm, "end": v(-17, -13.95) * mm});
            skLineSegment(sketch, "E1357", {"start": v(-17, -13.95) * mm, "end": v(-17.16, -14.24) * mm});
            skLineSegment(sketch, "E1358", {"start": v(-17.16, -14.24) * mm, "end": v(-17.16, -14.34) * mm});
            skLineSegment(sketch, "E1359", {"start": v(-17.16, -14.34) * mm, "end": v(-17.16, -14.44) * mm});
            skLineSegment(sketch, "E1360", {"start": v(-17.16, -14.44) * mm, "end": v(-17, -14.73) * mm});
            skLineSegment(sketch, "E1361", {"start": v(-17, -14.73) * mm, "end": v(-16.72, -14.88) * mm});
            skLineSegment(sketch, "E1362", {"start": v(-16.72, -14.88) * mm, "end": v(-16.63, -14.88) * mm});
            skLineSegment(sketch, "E1363", {"start": v(-16.63, -14.88) * mm, "end": v(-16.53, -14.88) * mm});
            skLineSegment(sketch, "E1364", {"start": v(-16.53, -14.88) * mm, "end": v(-16.24, -14.73) * mm});
            skLineSegment(sketch, "E1365", {"start": v(-16.24, -14.73) * mm, "end": v(-16.09, -14.44) * mm});
            skLineSegment(sketch, "E1366", {"start": v(-16.09, -14.44) * mm, "end": v(-16.09, -14.34) * mm});
            skLineSegment(sketch, "E1367", {"start": v(-16.09, -14.34) * mm, "end": v(-16.09, -14.24) * mm});
            skLineSegment(sketch, "E1368", {"start": v(-16.09, -14.24) * mm, "end": v(-16.24, -13.95) * mm});
            skLineSegment(sketch, "E1369", {"start": v(-16.24, -13.95) * mm, "end": v(-16.53, -13.8) * mm});
            skLineSegment(sketch, "E1370", {"start": v(-16.53, -13.8) * mm, "end": v(-16.63, -13.8) * mm});
            skLineSegment(sketch, "E1371", {"start": v(-36.4, -9.82) * mm, "end": v(-36.4, -10.28) * mm});
            skLineSegment(sketch, "E1372", {"start": v(-36.4, -10.28) * mm, "end": v(-33.44, -10.28) * mm});
            skLineSegment(sketch, "E1373", {"start": v(-33.44, -10.28) * mm, "end": v(-32.94, -9.57) * mm});
            skLineSegment(sketch, "E1374", {"start": v(-32.94, -9.57) * mm, "end": v(-36.2, -9.57) * mm});
            skLineSegment(sketch, "E1375", {"start": v(-36.2, -9.57) * mm, "end": v(-36.4, -9.82) * mm});
            skLineSegment(sketch, "E1376", {"start": v(-16.63, -13.4) * mm, "end": v(-16.54, -13.4) * mm});
            skLineSegment(sketch, "E1377", {"start": v(-16.54, -13.4) * mm, "end": v(-16.28, -13.25) * mm});
            skLineSegment(sketch, "E1378", {"start": v(-16.28, -13.25) * mm, "end": v(-16.14, -12.99) * mm});
            skLineSegment(sketch, "E1379", {"start": v(-16.14, -12.99) * mm, "end": v(-16.14, -12.9) * mm});
            skLineSegment(sketch, "E1380", {"start": v(-16.14, -12.9) * mm, "end": v(-16.14, -12.8) * mm});
            skLineSegment(sketch, "E1381", {"start": v(-16.14, -12.8) * mm, "end": v(-16.28, -12.54) * mm});
            skLineSegment(sketch, "E1382", {"start": v(-16.28, -12.54) * mm, "end": v(-16.54, -12.4) * mm});
            skLineSegment(sketch, "E1383", {"start": v(-16.54, -12.4) * mm, "end": v(-16.63, -12.4) * mm});
            skLineSegment(sketch, "E1384", {"start": v(-16.63, -12.4) * mm, "end": v(-16.71, -12.4) * mm});
            skLineSegment(sketch, "E1385", {"start": v(-16.71, -12.4) * mm, "end": v(-16.97, -12.54) * mm});
            skLineSegment(sketch, "E1386", {"start": v(-16.97, -12.54) * mm, "end": v(-17.1, -12.8) * mm});
            skLineSegment(sketch, "E1387", {"start": v(-17.1, -12.8) * mm, "end": v(-17.1, -12.9) * mm});
            skLineSegment(sketch, "E1388", {"start": v(-17.1, -12.9) * mm, "end": v(-17.1, -12.99) * mm});
            skLineSegment(sketch, "E1389", {"start": v(-17.1, -12.99) * mm, "end": v(-16.97, -13.25) * mm});
            skLineSegment(sketch, "E1390", {"start": v(-16.97, -13.25) * mm, "end": v(-16.71, -13.4) * mm});
            skLineSegment(sketch, "E1391", {"start": v(-16.71, -13.4) * mm, "end": v(-16.63, -13.4) * mm});
            skLineSegment(sketch, "E1392", {"start": v(2.3, -13.4) * mm, "end": v(2.38, -13.4) * mm});
            skLineSegment(sketch, "E1393", {"start": v(2.38, -13.4) * mm, "end": v(2.64, -13.25) * mm});
            skLineSegment(sketch, "E1394", {"start": v(2.64, -13.25) * mm, "end": v(2.78, -12.99) * mm});
            skLineSegment(sketch, "E1395", {"start": v(2.78, -12.99) * mm, "end": v(2.78, -12.9) * mm});
            skLineSegment(sketch, "E1396", {"start": v(2.78, -12.9) * mm, "end": v(2.78, -12.8) * mm});
            skLineSegment(sketch, "E1397", {"start": v(2.78, -12.8) * mm, "end": v(2.64, -12.54) * mm});
            skLineSegment(sketch, "E1398", {"start": v(2.64, -12.54) * mm, "end": v(2.38, -12.4) * mm});
            skLineSegment(sketch, "E1399", {"start": v(2.38, -12.4) * mm, "end": v(2.3, -12.4) * mm});
            skLineSegment(sketch, "E1400", {"start": v(2.3, -12.4) * mm, "end": v(2.2, -12.4) * mm});
            skLineSegment(sketch, "E1401", {"start": v(2.2, -12.4) * mm, "end": v(1.94, -12.54) * mm});
            skLineSegment(sketch, "E1402", {"start": v(1.94, -12.54) * mm, "end": v(1.81, -12.8) * mm});
            skLineSegment(sketch, "E1403", {"start": v(1.81, -12.8) * mm, "end": v(1.81, -12.9) * mm});
            skLineSegment(sketch, "E1404", {"start": v(1.81, -12.9) * mm, "end": v(1.81, -12.99) * mm});
            skLineSegment(sketch, "E1405", {"start": v(1.81, -12.99) * mm, "end": v(1.94, -13.25) * mm});
            skLineSegment(sketch, "E1406", {"start": v(1.94, -13.25) * mm, "end": v(2.2, -13.4) * mm});
            skLineSegment(sketch, "E1407", {"start": v(2.2, -13.4) * mm, "end": v(2.3, -13.4) * mm});
            skLineSegment(sketch, "E1408", {"start": v(-4.96, -19.7) * mm, "end": v(-3.95, -19.7) * mm});
            skLineSegment(sketch, "E1409", {"start": v(-3.95, -19.7) * mm, "end": v(-4.45, -18.25) * mm});
            skLineSegment(sketch, "E1410", {"start": v(-4.45, -18.25) * mm, "end": v(-4.96, -19.7) * mm});
            skLineSegment(sketch, "E1411", {"start": v(-19.05, -14.35) * mm, "end": v(-19.05, -12.93) * mm});
            skLineSegment(sketch, "E1412", {"start": v(-19.05, -12.93) * mm, "end": v(-19.05, -12.83) * mm});
            skLineSegment(sketch, "E1413", {"start": v(-19.05, -12.83) * mm, "end": v(-19.18, -12.54) * mm});
            skLineSegment(sketch, "E1414", {"start": v(-19.18, -12.54) * mm, "end": v(-19.44, -12.4) * mm});
            skLineSegment(sketch, "E1415", {"start": v(-19.44, -12.4) * mm, "end": v(-19.53, -12.4) * mm});
            skLineSegment(sketch, "E1416", {"start": v(-19.53, -12.4) * mm, "end": v(-19.62, -12.4) * mm});
            skLineSegment(sketch, "E1417", {"start": v(-19.62, -12.4) * mm, "end": v(-19.88, -12.54) * mm});
            skLineSegment(sketch, "E1418", {"start": v(-19.88, -12.54) * mm, "end": v(-20, -12.83) * mm});
            skLineSegment(sketch, "E1419", {"start": v(-20, -12.83) * mm, "end": v(-20, -12.93) * mm});
            skLineSegment(sketch, "E1420", {"start": v(-20, -12.93) * mm, "end": v(-20, -14.35) * mm});
            skLineSegment(sketch, "E1421", {"start": v(-20, -14.35) * mm, "end": v(-20, -14.45) * mm});
            skLineSegment(sketch, "E1422", {"start": v(-20, -14.45) * mm, "end": v(-19.88, -14.73) * mm});
            skLineSegment(sketch, "E1423", {"start": v(-19.88, -14.73) * mm, "end": v(-19.62, -14.88) * mm});
            skLineSegment(sketch, "E1424", {"start": v(-19.62, -14.88) * mm, "end": v(-19.53, -14.88) * mm});
            skLineSegment(sketch, "E1425", {"start": v(-19.53, -14.88) * mm, "end": v(-19.44, -14.88) * mm});
            skLineSegment(sketch, "E1426", {"start": v(-19.44, -14.88) * mm, "end": v(-19.18, -14.73) * mm});
            skLineSegment(sketch, "E1427", {"start": v(-19.18, -14.73) * mm, "end": v(-19.05, -14.45) * mm});
            skLineSegment(sketch, "E1428", {"start": v(-19.05, -14.45) * mm, "end": v(-19.05, -14.35) * mm});
            skLineSegment(sketch, "E1429", {"start": v(-11.55, 7.52) * mm, "end": v(-11.63, 7.52) * mm});
            skLineSegment(sketch, "E1430", {"start": v(-11.63, 7.52) * mm, "end": v(-11.82, 7.44) * mm});
            skLineSegment(sketch, "E1431", {"start": v(-11.82, 7.44) * mm, "end": v(-11.83, 7.42) * mm});
            skLineSegment(sketch, "E1432", {"start": v(-11.83, 7.42) * mm, "end": v(-11.87, 7.39) * mm});
            skLineSegment(sketch, "E1433", {"start": v(-11.87, 7.39) * mm, "end": v(-11.99, 6.88) * mm});
            skLineSegment(sketch, "E1434", {"start": v(-11.99, 6.88) * mm, "end": v(-11.99, 6.71) * mm});
            skLineSegment(sketch, "E1435", {"start": v(-11.99, 6.71) * mm, "end": v(-11.99, 6.53) * mm});
            skLineSegment(sketch, "E1436", {"start": v(-11.99, 6.53) * mm, "end": v(-11.87, 6.03) * mm});
            skLineSegment(sketch, "E1437", {"start": v(-11.87, 6.03) * mm, "end": v(-11.83, 6) * mm});
            skLineSegment(sketch, "E1438", {"start": v(-11.83, 6) * mm, "end": v(-11.82, 5.98) * mm});
            skLineSegment(sketch, "E1439", {"start": v(-11.82, 5.98) * mm, "end": v(-11.62, 5.9) * mm});
            skLineSegment(sketch, "E1440", {"start": v(-11.62, 5.9) * mm, "end": v(-11.55, 5.9) * mm});
            skLineSegment(sketch, "E1441", {"start": v(-11.55, 5.9) * mm, "end": v(-11.49, 5.9) * mm});
            skLineSegment(sketch, "E1442", {"start": v(-11.49, 5.9) * mm, "end": v(-11.3, 5.98) * mm});
            skLineSegment(sketch, "E1443", {"start": v(-11.3, 5.98) * mm, "end": v(-11.28, 6) * mm});
            skLineSegment(sketch, "E1444", {"start": v(-11.28, 6) * mm, "end": v(-11.24, 6.03) * mm});
            skLineSegment(sketch, "E1445", {"start": v(-11.24, 6.03) * mm, "end": v(-11.12, 6.54) * mm});
            skLineSegment(sketch, "E1446", {"start": v(-11.12, 6.54) * mm, "end": v(-11.12, 6.71) * mm});
            skLineSegment(sketch, "E1447", {"start": v(-11.12, 6.71) * mm, "end": v(-11.12, 6.89) * mm});
            skLineSegment(sketch, "E1448", {"start": v(-11.12, 6.89) * mm, "end": v(-11.24, 7.39) * mm});
            skLineSegment(sketch, "E1449", {"start": v(-11.24, 7.39) * mm, "end": v(-11.28, 7.42) * mm});
            skLineSegment(sketch, "E1450", {"start": v(-11.28, 7.42) * mm, "end": v(-11.3, 7.44) * mm});
            skLineSegment(sketch, "E1451", {"start": v(-11.3, 7.44) * mm, "end": v(-11.49, 7.52) * mm});
            skLineSegment(sketch, "E1452", {"start": v(-11.49, 7.52) * mm, "end": v(-11.55, 7.52) * mm});
            skLineSegment(sketch, "E1453", {"start": v(-12.3, -17.95) * mm, "end": v(-12.9, -17.95) * mm});
            skLineSegment(sketch, "E1454", {"start": v(-12.9, -17.95) * mm, "end": v(-12.9, -20.33) * mm});
            skLineSegment(sketch, "E1455", {"start": v(-12.9, -20.33) * mm, "end": v(-12.3, -20.33) * mm});
            skLineSegment(sketch, "E1456", {"start": v(-12.3, -20.33) * mm, "end": v(-12.16, -20.33) * mm});
            skLineSegment(sketch, "E1457", {"start": v(-12.16, -20.33) * mm, "end": v(-11.78, -20.15) * mm});
            skLineSegment(sketch, "E1458", {"start": v(-11.78, -20.15) * mm, "end": v(-11.75, -20.11) * mm});
            skLineSegment(sketch, "E1459", {"start": v(-11.75, -20.11) * mm, "end": v(-11.7, -20.06) * mm});
            skLineSegment(sketch, "E1460", {"start": v(-11.7, -20.06) * mm, "end": v(-11.6, -19.71) * mm});
            skLineSegment(sketch, "E1461", {"start": v(-11.6, -19.71) * mm, "end": v(-11.57, -19.27) * mm});
            skLineSegment(sketch, "E1462", {"start": v(-11.57, -19.27) * mm, "end": v(-11.57, -19.12) * mm});
            skLineSegment(sketch, "E1463", {"start": v(-11.57, -19.12) * mm, "end": v(-11.57, -18.98) * mm});
            skLineSegment(sketch, "E1464", {"start": v(-11.57, -18.98) * mm, "end": v(-11.6, -18.55) * mm});
            skLineSegment(sketch, "E1465", {"start": v(-11.6, -18.55) * mm, "end": v(-11.7, -18.22) * mm});
            skLineSegment(sketch, "E1466", {"start": v(-11.7, -18.22) * mm, "end": v(-11.75, -18.17) * mm});
            skLineSegment(sketch, "E1467", {"start": v(-11.75, -18.17) * mm, "end": v(-11.78, -18.14) * mm});
            skLineSegment(sketch, "E1468", {"start": v(-11.78, -18.14) * mm, "end": v(-12.17, -17.95) * mm});
            skLineSegment(sketch, "E1469", {"start": v(-12.17, -17.95) * mm, "end": v(-12.3, -17.95) * mm});
            skLineSegment(sketch, "E1470", {"start": v(0.66, -18.84) * mm, "end": v(0.58, -18.84) * mm});
            skLineSegment(sketch, "E1471", {"start": v(0.58, -18.84) * mm, "end": v(0.34, -18.95) * mm});
            skLineSegment(sketch, "E1472", {"start": v(0.34, -18.95) * mm, "end": v(0.32, -18.97) * mm});
            skLineSegment(sketch, "E1473", {"start": v(0.32, -18.97) * mm, "end": v(0.29, -19) * mm});
            skLineSegment(sketch, "E1474", {"start": v(0.29, -19) * mm, "end": v(0.16, -19.46) * mm});
            skLineSegment(sketch, "E1475", {"start": v(0.16, -19.46) * mm, "end": v(0.16, -19.61) * mm});
            skLineSegment(sketch, "E1476", {"start": v(0.16, -19.61) * mm, "end": v(0.16, -19.77) * mm});
            skLineSegment(sketch, "E1477", {"start": v(0.16, -19.77) * mm, "end": v(0.29, -20.21) * mm});
            skLineSegment(sketch, "E1478", {"start": v(0.29, -20.21) * mm, "end": v(0.32, -20.25) * mm});
            skLineSegment(sketch, "E1479", {"start": v(0.32, -20.25) * mm, "end": v(0.34, -20.27) * mm});
            skLineSegment(sketch, "E1480", {"start": v(0.34, -20.27) * mm, "end": v(0.58, -20.39) * mm});
            skLineSegment(sketch, "E1481", {"start": v(0.58, -20.39) * mm, "end": v(0.66, -20.39) * mm});
            skLineSegment(sketch, "E1482", {"start": v(0.66, -20.39) * mm, "end": v(0.75, -20.39) * mm});
            skLineSegment(sketch, "E1483", {"start": v(0.75, -20.39) * mm, "end": v(0.99, -20.27) * mm});
            skLineSegment(sketch, "E1484", {"start": v(0.99, -20.27) * mm, "end": v(1, -20.25) * mm});
            skLineSegment(sketch, "E1485", {"start": v(1, -20.25) * mm, "end": v(1.04, -20.21) * mm});
            skLineSegment(sketch, "E1486", {"start": v(1.04, -20.21) * mm, "end": v(1.17, -19.76) * mm});
            skLineSegment(sketch, "E1487", {"start": v(1.17, -19.76) * mm, "end": v(1.17, -19.61) * mm});
            skLineSegment(sketch, "E1488", {"start": v(1.17, -19.61) * mm, "end": v(1.17, -19.45) * mm});
            skLineSegment(sketch, "E1489", {"start": v(1.17, -19.45) * mm, "end": v(1.04, -19) * mm});
            skLineSegment(sketch, "E1490", {"start": v(1.04, -19) * mm, "end": v(1, -18.97) * mm});
            skLineSegment(sketch, "E1491", {"start": v(1, -18.97) * mm, "end": v(0.99, -18.95) * mm});
            skLineSegment(sketch, "E1492", {"start": v(0.99, -18.95) * mm, "end": v(0.74, -18.84) * mm});
            skLineSegment(sketch, "E1493", {"start": v(0.74, -18.84) * mm, "end": v(0.66, -18.84) * mm});
            skLineSegment(sketch, "E1494", {"start": v(-18.3, -18.47) * mm, "end": v(-18.3, -18.37) * mm});
            skLineSegment(sketch, "E1495", {"start": v(-18.3, -18.37) * mm, "end": v(-18.45, -18.1) * mm});
            skLineSegment(sketch, "E1496", {"start": v(-18.45, -18.1) * mm, "end": v(-18.76, -17.95) * mm});
            skLineSegment(sketch, "E1497", {"start": v(-18.76, -17.95) * mm, "end": v(-18.85, -17.95) * mm});
            skLineSegment(sketch, "E1498", {"start": v(-18.85, -17.95) * mm, "end": v(-19.59, -17.95) * mm});
            skLineSegment(sketch, "E1499", {"start": v(-19.59, -17.95) * mm, "end": v(-19.59, -18.98) * mm});
            skLineSegment(sketch, "E1500", {"start": v(-19.59, -18.98) * mm, "end": v(-18.85, -18.98) * mm});
            skLineSegment(sketch, "E1501", {"start": v(-18.85, -18.98) * mm, "end": v(-18.76, -18.98) * mm});
            skLineSegment(sketch, "E1502", {"start": v(-18.76, -18.98) * mm, "end": v(-18.45, -18.84) * mm});
            skLineSegment(sketch, "E1503", {"start": v(-18.45, -18.84) * mm, "end": v(-18.3, -18.56) * mm});
            skLineSegment(sketch, "E1504", {"start": v(-18.3, -18.56) * mm, "end": v(-18.3, -18.47) * mm});
            skLineSegment(sketch, "E1505", {"start": v(-36.15, 6.6) * mm, "end": v(-36.43, 6.26) * mm});
            skLineSegment(sketch, "E1506", {"start": v(-36.43, 6.26) * mm, "end": v(-36.43, 5.9) * mm});
            skLineSegment(sketch, "E1507", {"start": v(-36.43, 5.9) * mm, "end": v(-30.7, 5.9) * mm});
            skLineSegment(sketch, "E1508", {"start": v(-30.7, 5.9) * mm, "end": v(-30.7, 6.29) * mm});
            skLineSegment(sketch, "E1509", {"start": v(-30.7, 6.29) * mm, "end": v(-30.95, 6.6) * mm});
            skLineSegment(sketch, "E1510", {"start": v(-30.95, 6.6) * mm, "end": v(-36.15, 6.6) * mm});
            skLineSegment(sketch, "E1511", {"start": v(5.2, -13.8) * mm, "end": v(5.1, -13.8) * mm});
            skLineSegment(sketch, "E1512", {"start": v(5.1, -13.8) * mm, "end": v(4.81, -13.95) * mm});
            skLineSegment(sketch, "E1513", {"start": v(4.81, -13.95) * mm, "end": v(4.66, -14.24) * mm});
            skLineSegment(sketch, "E1514", {"start": v(4.66, -14.24) * mm, "end": v(4.66, -14.34) * mm});
            skLineSegment(sketch, "E1515", {"start": v(4.66, -14.34) * mm, "end": v(4.66, -14.44) * mm});
            skLineSegment(sketch, "E1516", {"start": v(4.66, -14.44) * mm, "end": v(4.81, -14.73) * mm});
            skLineSegment(sketch, "E1517", {"start": v(4.81, -14.73) * mm, "end": v(5.1, -14.88) * mm});
            skLineSegment(sketch, "E1518", {"start": v(5.1, -14.88) * mm, "end": v(5.2, -14.88) * mm});
            skLineSegment(sketch, "E1519", {"start": v(5.2, -14.88) * mm, "end": v(5.3, -14.88) * mm});
            skLineSegment(sketch, "E1520", {"start": v(5.3, -14.88) * mm, "end": v(5.58, -14.73) * mm});
            skLineSegment(sketch, "E1521", {"start": v(5.58, -14.73) * mm, "end": v(5.73, -14.44) * mm});
            skLineSegment(sketch, "E1522", {"start": v(5.73, -14.44) * mm, "end": v(5.73, -14.34) * mm});
            skLineSegment(sketch, "E1523", {"start": v(5.73, -14.34) * mm, "end": v(5.73, -14.24) * mm});
            skLineSegment(sketch, "E1524", {"start": v(5.73, -14.24) * mm, "end": v(5.58, -13.95) * mm});
            skLineSegment(sketch, "E1525", {"start": v(5.58, -13.95) * mm, "end": v(5.3, -13.8) * mm});
            skLineSegment(sketch, "E1526", {"start": v(5.3, -13.8) * mm, "end": v(5.2, -13.8) * mm});
            skLineSegment(sketch, "E1527", {"start": v(-22.43, -13.53) * mm, "end": v(-22.34, -13.53) * mm});
            skLineSegment(sketch, "E1528", {"start": v(-22.34, -13.53) * mm, "end": v(-22.07, -13.38) * mm});
            skLineSegment(sketch, "E1529", {"start": v(-22.07, -13.38) * mm, "end": v(-21.93, -13.07) * mm});
            skLineSegment(sketch, "E1530", {"start": v(-21.93, -13.07) * mm, "end": v(-21.93, -12.97) * mm});
            skLineSegment(sketch, "E1531", {"start": v(-21.93, -12.97) * mm, "end": v(-21.93, -12.86) * mm});
            skLineSegment(sketch, "E1532", {"start": v(-21.93, -12.86) * mm, "end": v(-22.07, -12.55) * mm});
            skLineSegment(sketch, "E1533", {"start": v(-22.07, -12.55) * mm, "end": v(-22.34, -12.4) * mm});
            skLineSegment(sketch, "E1534", {"start": v(-22.34, -12.4) * mm, "end": v(-22.43, -12.4) * mm});
            skLineSegment(sketch, "E1535", {"start": v(-22.43, -12.4) * mm, "end": v(-22.52, -12.4) * mm});
            skLineSegment(sketch, "E1536", {"start": v(-22.52, -12.4) * mm, "end": v(-22.79, -12.55) * mm});
            skLineSegment(sketch, "E1537", {"start": v(-22.79, -12.55) * mm, "end": v(-22.93, -12.86) * mm});
            skLineSegment(sketch, "E1538", {"start": v(-22.93, -12.86) * mm, "end": v(-22.93, -12.97) * mm});
            skLineSegment(sketch, "E1539", {"start": v(-22.93, -12.97) * mm, "end": v(-22.93, -13.07) * mm});
            skLineSegment(sketch, "E1540", {"start": v(-22.93, -13.07) * mm, "end": v(-22.8, -13.37) * mm});
            skLineSegment(sketch, "E1541", {"start": v(-22.8, -13.37) * mm, "end": v(-22.52, -13.53) * mm});
            skLineSegment(sketch, "E1542", {"start": v(-22.52, -13.53) * mm, "end": v(-22.43, -13.53) * mm});
            skLineSegment(sketch, "E1543", {"start": v(3.58, -18.84) * mm, "end": v(3.5, -18.84) * mm});
            skLineSegment(sketch, "E1544", {"start": v(3.5, -18.84) * mm, "end": v(3.27, -18.95) * mm});
            skLineSegment(sketch, "E1545", {"start": v(3.27, -18.95) * mm, "end": v(3.25, -18.97) * mm});
            skLineSegment(sketch, "E1546", {"start": v(3.25, -18.97) * mm, "end": v(3.2, -19) * mm});
            skLineSegment(sketch, "E1547", {"start": v(3.2, -19) * mm, "end": v(3.08, -19.46) * mm});
            skLineSegment(sketch, "E1548", {"start": v(3.08, -19.46) * mm, "end": v(3.08, -19.61) * mm});
            skLineSegment(sketch, "E1549", {"start": v(3.08, -19.61) * mm, "end": v(3.08, -19.77) * mm});
            skLineSegment(sketch, "E1550", {"start": v(3.08, -19.77) * mm, "end": v(3.2, -20.21) * mm});
            skLineSegment(sketch, "E1551", {"start": v(3.2, -20.21) * mm, "end": v(3.25, -20.25) * mm});
            skLineSegment(sketch, "E1552", {"start": v(3.25, -20.25) * mm, "end": v(3.27, -20.27) * mm});
            skLineSegment(sketch, "E1553", {"start": v(3.27, -20.27) * mm, "end": v(3.5, -20.39) * mm});
            skLineSegment(sketch, "E1554", {"start": v(3.5, -20.39) * mm, "end": v(3.58, -20.39) * mm});
            skLineSegment(sketch, "E1555", {"start": v(3.58, -20.39) * mm, "end": v(3.67, -20.39) * mm});
            skLineSegment(sketch, "E1556", {"start": v(3.67, -20.39) * mm, "end": v(3.9, -20.27) * mm});
            skLineSegment(sketch, "E1557", {"start": v(3.9, -20.27) * mm, "end": v(3.93, -20.25) * mm});
            skLineSegment(sketch, "E1558", {"start": v(3.93, -20.25) * mm, "end": v(3.96, -20.21) * mm});
            skLineSegment(sketch, "E1559", {"start": v(3.96, -20.21) * mm, "end": v(4.09, -19.76) * mm});
            skLineSegment(sketch, "E1560", {"start": v(4.09, -19.76) * mm, "end": v(4.09, -19.61) * mm});
            skLineSegment(sketch, "E1561", {"start": v(4.09, -19.61) * mm, "end": v(4.09, -19.45) * mm});
            skLineSegment(sketch, "E1562", {"start": v(4.09, -19.45) * mm, "end": v(3.96, -19) * mm});
            skLineSegment(sketch, "E1563", {"start": v(3.96, -19) * mm, "end": v(3.93, -18.97) * mm});
            skLineSegment(sketch, "E1564", {"start": v(3.93, -18.97) * mm, "end": v(3.9, -18.95) * mm});
            skLineSegment(sketch, "E1565", {"start": v(3.9, -18.95) * mm, "end": v(3.66, -18.84) * mm});
            skLineSegment(sketch, "E1566", {"start": v(3.66, -18.84) * mm, "end": v(3.58, -18.84) * mm});
            skLineSegment(sketch, "E1567", {"start": v(-19.25, 5.94) * mm, "end": v(-19.23, 5.96) * mm});
            skLineSegment(sketch, "E1568", {"start": v(-19.23, 5.96) * mm, "end": v(-19.15, 6.2) * mm});
            skLineSegment(sketch, "E1569", {"start": v(-19.15, 6.2) * mm, "end": v(-19.15, 6.29) * mm});
            skLineSegment(sketch, "E1570", {"start": v(-19.15, 6.29) * mm, "end": v(-19.15, 6.37) * mm});
            skLineSegment(sketch, "E1571", {"start": v(-19.15, 6.37) * mm, "end": v(-19.68, 6.37) * mm});
            skLineSegment(sketch, "E1572", {"start": v(-19.68, 6.37) * mm, "end": v(-19.74, 6.37) * mm});
            skLineSegment(sketch, "E1573", {"start": v(-19.74, 6.37) * mm, "end": v(-19.92, 6.3) * mm});
            skLineSegment(sketch, "E1574", {"start": v(-19.92, 6.3) * mm, "end": v(-20, 6.15) * mm});
            skLineSegment(sketch, "E1575", {"start": v(-20, 6.15) * mm, "end": v(-20, 6.1) * mm});
            skLineSegment(sketch, "E1576", {"start": v(-20, 6.1) * mm, "end": v(-20, 6.05) * mm});
            skLineSegment(sketch, "E1577", {"start": v(-20, 6.05) * mm, "end": v(-19.92, 5.9) * mm});
            skLineSegment(sketch, "E1578", {"start": v(-19.92, 5.9) * mm, "end": v(-19.73, 5.82) * mm});
            skLineSegment(sketch, "E1579", {"start": v(-19.73, 5.82) * mm, "end": v(-19.66, 5.82) * mm});
            skLineSegment(sketch, "E1580", {"start": v(-19.66, 5.82) * mm, "end": v(-19.56, 5.82) * mm});
            skLineSegment(sketch, "E1581", {"start": v(-19.56, 5.82) * mm, "end": v(-19.28, 5.92) * mm});
            skLineSegment(sketch, "E1582", {"start": v(-19.28, 5.92) * mm, "end": v(-19.25, 5.94) * mm});
            skLineSegment(sketch, "E1583", {"start": v(2.3, -13.8) * mm, "end": v(2.2, -13.8) * mm});
            skLineSegment(sketch, "E1584", {"start": v(2.2, -13.8) * mm, "end": v(1.91, -13.95) * mm});
            skLineSegment(sketch, "E1585", {"start": v(1.91, -13.95) * mm, "end": v(1.76, -14.24) * mm});
            skLineSegment(sketch, "E1586", {"start": v(1.76, -14.24) * mm, "end": v(1.76, -14.34) * mm});
            skLineSegment(sketch, "E1587", {"start": v(1.76, -14.34) * mm, "end": v(1.76, -14.44) * mm});
            skLineSegment(sketch, "E1588", {"start": v(1.76, -14.44) * mm, "end": v(1.91, -14.73) * mm});
            skLineSegment(sketch, "E1589", {"start": v(1.91, -14.73) * mm, "end": v(2.2, -14.88) * mm});
            skLineSegment(sketch, "E1590", {"start": v(2.2, -14.88) * mm, "end": v(2.3, -14.88) * mm});
            skLineSegment(sketch, "E1591", {"start": v(2.3, -14.88) * mm, "end": v(2.39, -14.88) * mm});
            skLineSegment(sketch, "E1592", {"start": v(2.39, -14.88) * mm, "end": v(2.67, -14.73) * mm});
            skLineSegment(sketch, "E1593", {"start": v(2.67, -14.73) * mm, "end": v(2.83, -14.44) * mm});
            skLineSegment(sketch, "E1594", {"start": v(2.83, -14.44) * mm, "end": v(2.83, -14.34) * mm});
            skLineSegment(sketch, "E1595", {"start": v(2.83, -14.34) * mm, "end": v(2.83, -14.24) * mm});
            skLineSegment(sketch, "E1596", {"start": v(2.83, -14.24) * mm, "end": v(2.67, -13.95) * mm});
            skLineSegment(sketch, "E1597", {"start": v(2.67, -13.95) * mm, "end": v(2.39, -13.8) * mm});
            skLineSegment(sketch, "E1598", {"start": v(2.39, -13.8) * mm, "end": v(2.3, -13.8) * mm});
            skLineSegment(sketch, "E1599", {"start": v(5.2, -13.4) * mm, "end": v(5.28, -13.4) * mm});
            skLineSegment(sketch, "E1600", {"start": v(5.28, -13.4) * mm, "end": v(5.54, -13.25) * mm});
            skLineSegment(sketch, "E1601", {"start": v(5.54, -13.25) * mm, "end": v(5.68, -12.99) * mm});
            skLineSegment(sketch, "E1602", {"start": v(5.68, -12.99) * mm, "end": v(5.68, -12.9) * mm});
            skLineSegment(sketch, "E1603", {"start": v(5.68, -12.9) * mm, "end": v(5.68, -12.8) * mm});
            skLineSegment(sketch, "E1604", {"start": v(5.68, -12.8) * mm, "end": v(5.54, -12.54) * mm});
            skLineSegment(sketch, "E1605", {"start": v(5.54, -12.54) * mm, "end": v(5.28, -12.4) * mm});
            skLineSegment(sketch, "E1606", {"start": v(5.28, -12.4) * mm, "end": v(5.2, -12.4) * mm});
            skLineSegment(sketch, "E1607", {"start": v(5.2, -12.4) * mm, "end": v(5.1, -12.4) * mm});
            skLineSegment(sketch, "E1608", {"start": v(5.1, -12.4) * mm, "end": v(4.85, -12.54) * mm});
            skLineSegment(sketch, "E1609", {"start": v(4.85, -12.54) * mm, "end": v(4.71, -12.8) * mm});
            skLineSegment(sketch, "E1610", {"start": v(4.71, -12.8) * mm, "end": v(4.71, -12.9) * mm});
            skLineSegment(sketch, "E1611", {"start": v(4.71, -12.9) * mm, "end": v(4.71, -12.99) * mm});
            skLineSegment(sketch, "E1612", {"start": v(4.71, -12.99) * mm, "end": v(4.85, -13.25) * mm});
            skLineSegment(sketch, "E1613", {"start": v(4.85, -13.25) * mm, "end": v(5.1, -13.4) * mm});
            skLineSegment(sketch, "E1614", {"start": v(5.1, -13.4) * mm, "end": v(5.2, -13.4) * mm});
            skSolve(sketch);
        }
        {
            var Q0;
            Q0=makeQuery(id+"F0.imprint","IMPRINT",FACE,{"disambiguationData":[TD([[makeQuery(id+"F0.imprint","IMPRINT",EDGE,{"derivedFrom":sQuery(id+"F0.wireOp",EDGE,"E58")}),1.0]])]});
            var Q1;
            Q1=makeQuery(id+"F0.imprint","IMPRINT",FACE,{"disambiguationData":[TD([[makeQuery(id+"F0.imprint","IMPRINT",EDGE,{"derivedFrom":sQuery(id+"F0.wireOp",EDGE,"E1505")}),1.0]])]});
            var Q2;
            Q2=makeQuery(id+"F0.imprint","IMPRINT",FACE,{"disambiguationData":[TD([[makeQuery(id+"F0.imprint","IMPRINT",EDGE,{"derivedFrom":sQuery(id+"F0.wireOp",EDGE,"E1371")}),1.0]])]});
            var Q3;
            Q3=makeQuery(id+"F0.imprint","IMPRINT",FACE,{"disambiguationData":[TD([[makeQuery(id+"F0.imprint","IMPRINT",EDGE,{"derivedFrom":sQuery(id+"F0.wireOp",EDGE,"E1567")}),1.0]])]});
            var Q4;
            Q4=makeQuery(id+"F0.imprint","IMPRINT",FACE,{"disambiguationData":[TD([[makeQuery(id+"F0.imprint","IMPRINT",EDGE,{"derivedFrom":sQuery(id+"F0.wireOp",EDGE,"E1429")}),1.0]])]});
            var Q5;
            Q5=makeQuery(id+"F0.imprint","IMPRINT",FACE,{"disambiguationData":[TD([[makeQuery(id+"F0.imprint","IMPRINT",EDGE,{"derivedFrom":sQuery(id+"F0.wireOp",EDGE,"E0")}),1.0]])]});
            var Q6;
            Q6=makeQuery(id+"F0.imprint","IMPRINT",FACE,{"disambiguationData":[TD([[makeQuery(id+"F0.imprint","IMPRINT",EDGE,{"derivedFrom":sQuery(id+"F0.wireOp",EDGE,"E1323")}),1.0]])]});
            var Q7;
            Q7=makeQuery(id+"F0.imprint","IMPRINT",FACE,{"disambiguationData":[TD([[makeQuery(id+"F0.imprint","IMPRINT",EDGE,{"derivedFrom":sQuery(id+"F0.wireOp",EDGE,"E42")}),1.0]])]});
            var Q8;
            Q8=makeQuery(id+"F0.imprint","IMPRINT",FACE,{"disambiguationData":[TD([[makeQuery(id+"F0.imprint","IMPRINT",EDGE,{"derivedFrom":sQuery(id+"F0.wireOp",EDGE,"E1283")}),1.0]])]});
            var Q9;
            Q9=makeQuery(id+"F0.imprint","IMPRINT",FACE,{"disambiguationData":[TD([[makeQuery(id+"F0.imprint","IMPRINT",EDGE,{"derivedFrom":sQuery(id+"F0.wireOp",EDGE,"E26")}),1.0]])]});
            var Q10;
            Q10=makeQuery(id+"F0.imprint","IMPRINT",FACE,{"disambiguationData":[TD([[makeQuery(id+"F0.imprint","IMPRINT",EDGE,{"derivedFrom":sQuery(id+"F0.wireOp",EDGE,"E13")}),1.0]])]});
            var Q11;
            Q11=makeQuery(id+"F0.imprint","IMPRINT",FACE,{"disambiguationData":[TD([[makeQuery(id+"F0.imprint","IMPRINT",EDGE,{"derivedFrom":sQuery(id+"F0.wireOp",EDGE,"E1527")}),1.0]])]});
            var Q12;
            Q12=makeQuery(id+"F0.imprint","IMPRINT",FACE,{"disambiguationData":[TD([[makeQuery(id+"F0.imprint","IMPRINT",EDGE,{"derivedFrom":sQuery(id+"F0.wireOp",EDGE,"E1411")}),1.0]])]});
            var Q13;
            Q13=makeQuery(id+"F0.imprint","IMPRINT",FACE,{"disambiguationData":[TD([[makeQuery(id+"F0.imprint","IMPRINT",EDGE,{"derivedFrom":sQuery(id+"F0.wireOp",EDGE,"E1376")}),1.0]])]});
            var Q14;
            Q14=makeQuery(id+"F0.imprint","IMPRINT",FACE,{"disambiguationData":[TD([[makeQuery(id+"F0.imprint","IMPRINT",EDGE,{"derivedFrom":sQuery(id+"F0.wireOp",EDGE,"E1355")}),1.0]])]});
            var Q15;
            Q15=makeQuery(id+"F0.imprint","IMPRINT",FACE,{"disambiguationData":[TD([[makeQuery(id+"F0.imprint","IMPRINT",EDGE,{"derivedFrom":sQuery(id+"F0.wireOp",EDGE,"E1339")}),1.0]])]});
            var Q16;
            Q16=makeQuery(id+"F0.imprint","IMPRINT",FACE,{"disambiguationData":[TD([[makeQuery(id+"F0.imprint","IMPRINT",EDGE,{"derivedFrom":sQuery(id+"F0.wireOp",EDGE,"E1392")}),1.0]])]});
            var Q17;
            Q17=makeQuery(id+"F0.imprint","IMPRINT",FACE,{"disambiguationData":[TD([[makeQuery(id+"F0.imprint","IMPRINT",EDGE,{"derivedFrom":sQuery(id+"F0.wireOp",EDGE,"E1583")}),1.0]])]});
            var Q18;
            Q18=makeQuery(id+"F0.imprint","IMPRINT",FACE,{"disambiguationData":[TD([[makeQuery(id+"F0.imprint","IMPRINT",EDGE,{"derivedFrom":sQuery(id+"F0.wireOp",EDGE,"E1599")}),1.0]])]});
            var Q19;
            Q19=makeQuery(id+"F0.imprint","IMPRINT",FACE,{"disambiguationData":[TD([[makeQuery(id+"F0.imprint","IMPRINT",EDGE,{"derivedFrom":sQuery(id+"F0.wireOp",EDGE,"E1511")}),1.0]])]});
            var Q20;
            Q20=makeQuery(id+"F0.imprint","IMPRINT",FACE,{"disambiguationData":[TD([[makeQuery(id+"F0.imprint","IMPRINT",EDGE,{"derivedFrom":sQuery(id+"F0.wireOp",EDGE,"E1299")}),1.0]])]});
            var Q21;
            Q21=makeQuery(id+"F0.imprint","IMPRINT",FACE,{"disambiguationData":[TD([[makeQuery(id+"F0.imprint","IMPRINT",EDGE,{"derivedFrom":sQuery(id+"F0.wireOp",EDGE,"E1543")}),1.0]])]});
            var Q22;
            Q22=makeQuery(id+"F0.imprint","IMPRINT",FACE,{"disambiguationData":[TD([[makeQuery(id+"F0.imprint","IMPRINT",EDGE,{"derivedFrom":sQuery(id+"F0.wireOp",EDGE,"E1470")}),1.0]])]});
            var Q23;
            Q23=makeQuery(id+"F0.imprint","IMPRINT",FACE,{"disambiguationData":[TD([[makeQuery(id+"F0.imprint","IMPRINT",EDGE,{"derivedFrom":sQuery(id+"F0.wireOp",EDGE,"E1408")}),1.0]])]});
            var Q24;
            Q24=makeQuery(id+"F0.imprint","IMPRINT",FACE,{"disambiguationData":[TD([[makeQuery(id+"F0.imprint","IMPRINT",EDGE,{"derivedFrom":sQuery(id+"F0.wireOp",EDGE,"E1453")}),1.0]])]});
            var Q25;
            Q25=makeQuery(id+"F0.imprint","IMPRINT",FACE,{"disambiguationData":[TD([[makeQuery(id+"F0.imprint","IMPRINT",EDGE,{"derivedFrom":sQuery(id+"F0.wireOp",EDGE,"E1494")}),1.0]])]});
            extrude(context, id + "F1", {"entities" : qUnion([Q0, Q1, Q2, Q3, Q4, Q5, Q6, Q7, Q8, Q9, Q10, Q11, Q12, Q13, Q14, Q15, Q16, Q17, Q18, Q19, Q20, Q21, Q22, Q23, Q24, Q25]), "oppositeDirection" : true, "depth" : 1.59 * mm, "offsetDistance" : 25.4 * mm, "symmetric" : true});
        }
        {
            var Q0;
            Q0=makeQuery(id+"F0.imprint","IMPRINT",FACE,{"disambiguationData":[TD([[makeQuery(id+"F0.imprint","IMPRINT",EDGE,{"derivedFrom":sQuery(id+"F0.wireOp",EDGE,"E440")}),-1.0]])]});
            var Q1;
            Q1=makeQuery(id+"F0.imprint","IMPRINT",FACE,{"disambiguationData":[TD([[makeQuery(id+"F0.imprint","IMPRINT",EDGE,{"derivedFrom":sQuery(id+"F0.wireOp",EDGE,"E425")}),-1.0]])]});
            var Q2;
            Q2=makeQuery(id+"F0.imprint","IMPRINT",FACE,{"disambiguationData":[TD([[makeQuery(id+"F0.imprint","IMPRINT",EDGE,{"derivedFrom":sQuery(id+"F0.wireOp",EDGE,"E404")}),-1.0]])]});
            var Q3;
            Q3=makeQuery(id+"F0.imprint","IMPRINT",FACE,{"disambiguationData":[TD([[makeQuery(id+"F0.imprint","IMPRINT",EDGE,{"derivedFrom":sQuery(id+"F0.wireOp",EDGE,"E413")}),-1.0]])]});
            var Q4;
            Q4=makeQuery(id+"F0.imprint","IMPRINT",FACE,{"disambiguationData":[TD([[makeQuery(id+"F0.imprint","IMPRINT",EDGE,{"derivedFrom":sQuery(id+"F0.wireOp",EDGE,"E446")}),-1.0]])]});
            var Q5;
            Q5=makeQuery(id+"F0.imprint","IMPRINT",FACE,{"disambiguationData":[TD([[makeQuery(id+"F0.imprint","IMPRINT",EDGE,{"derivedFrom":sQuery(id+"F0.wireOp",EDGE,"E461")}),-1.0]])]});
            var Q6;
            Q6=makeQuery(id+"F0.imprint","IMPRINT",FACE,{"disambiguationData":[TD([[makeQuery(id+"F0.imprint","IMPRINT",EDGE,{"derivedFrom":sQuery(id+"F0.wireOp",EDGE,"E400")}),-1.0]])]});
            var Q7;
            Q7=makeQuery(id+"F0.imprint","IMPRINT",FACE,{"disambiguationData":[TD([[makeQuery(id+"F0.imprint","IMPRINT",EDGE,{"derivedFrom":sQuery(id+"F0.wireOp",EDGE,"E507")}),-1.0]])]});
            var Q8;
            Q8=makeQuery(id+"F0.imprint","IMPRINT",FACE,{"disambiguationData":[TD([[makeQuery(id+"F0.imprint","IMPRINT",EDGE,{"derivedFrom":sQuery(id+"F0.wireOp",EDGE,"E257")}),-1.0]])]});
            var Q9;
            Q9=makeQuery(id+"F0.imprint","IMPRINT",FACE,{"disambiguationData":[TD([[makeQuery(id+"F0.imprint","IMPRINT",EDGE,{"derivedFrom":sQuery(id+"F0.wireOp",EDGE,"E653")}),-1.0]])]});
            var Q10;
            Q10=makeQuery(id+"F0.imprint","IMPRINT",FACE,{"disambiguationData":[TD([[makeQuery(id+"F0.imprint","IMPRINT",EDGE,{"derivedFrom":sQuery(id+"F0.wireOp",EDGE,"E166")}),-1.0]])]});
            var Q11;
            Q11=makeQuery(id+"F0.imprint","IMPRINT",FACE,{"disambiguationData":[TD([[makeQuery(id+"F0.imprint","IMPRINT",EDGE,{"derivedFrom":sQuery(id+"F0.wireOp",EDGE,"E104")}),-1.0]])]});
            var Q12;
            Q12=makeQuery(id+"F0.imprint","IMPRINT",FACE,{"disambiguationData":[TD([[makeQuery(id+"F0.imprint","IMPRINT",EDGE,{"derivedFrom":sQuery(id+"F0.wireOp",EDGE,"E26")}),-1.0]])]});
            var Q13;
            Q13=makeQuery(id+"F0.imprint","IMPRINT",FACE,{"disambiguationData":[TD([[makeQuery(id+"F0.imprint","IMPRINT",EDGE,{"derivedFrom":sQuery(id+"F0.wireOp",EDGE,"E984")}),-1.0]])]});
            var Q14;
            Q14=makeQuery(id+"F0.imprint","IMPRINT",FACE,{"disambiguationData":[TD([[makeQuery(id+"F0.imprint","IMPRINT",EDGE,{"derivedFrom":sQuery(id+"F0.wireOp",EDGE,"E1164")}),-1.0]])]});
            var Q15;
            Q15=makeQuery(id+"F0.imprint","IMPRINT",FACE,{"disambiguationData":[TD([[makeQuery(id+"F0.imprint","IMPRINT",EDGE,{"derivedFrom":sQuery(id+"F0.wireOp",EDGE,"E13")}),-1.0]])]});
            var Q16;
            Q16=makeQuery(id+"F0.imprint","IMPRINT",FACE,{"disambiguationData":[TD([[makeQuery(id+"F0.imprint","IMPRINT",EDGE,{"derivedFrom":sQuery(id+"F0.wireOp",EDGE,"E1262")}),-1.0]])]});
            var Q17;
            Q17=makeQuery(id+"F0.imprint","IMPRINT",FACE,{"disambiguationData":[TD([[makeQuery(id+"F0.imprint","IMPRINT",EDGE,{"derivedFrom":sQuery(id+"F0.wireOp",EDGE,"E117")}),-1.0]])]});
            var Q18;
            Q18=makeQuery(id+"F0.imprint","IMPRINT",FACE,{"disambiguationData":[TD([[makeQuery(id+"F0.imprint","IMPRINT",EDGE,{"derivedFrom":sQuery(id+"F0.wireOp",EDGE,"E141")}),-1.0]])]});
            var Q19;
            Q19=makeQuery(id+"F0.imprint","IMPRINT",FACE,{"disambiguationData":[TD([[makeQuery(id+"F0.imprint","IMPRINT",EDGE,{"derivedFrom":sQuery(id+"F0.wireOp",EDGE,"E192")}),-1.0]])]});
            var Q20;
            Q20=makeQuery(id+"F0.imprint","IMPRINT",FACE,{"disambiguationData":[TD([[makeQuery(id+"F0.imprint","IMPRINT",EDGE,{"derivedFrom":sQuery(id+"F0.wireOp",EDGE,"E42")}),-1.0]])]});
            var Q21;
            Q21=makeQuery(id+"F0.imprint","IMPRINT",FACE,{"disambiguationData":[TD([[makeQuery(id+"F0.imprint","IMPRINT",EDGE,{"derivedFrom":sQuery(id+"F0.wireOp",EDGE,"E313")}),-1.0]])]});
            var Q22;
            Q22=makeQuery(id+"F0.imprint","IMPRINT",FACE,{"disambiguationData":[TD([[makeQuery(id+"F0.imprint","IMPRINT",EDGE,{"derivedFrom":sQuery(id+"F0.wireOp",EDGE,"E0")}),-1.0]])]});
            var Q23;
            Q23=makeQuery(id+"F0.imprint","IMPRINT",FACE,{"disambiguationData":[TD([[makeQuery(id+"F0.imprint","IMPRINT",EDGE,{"derivedFrom":sQuery(id+"F0.wireOp",EDGE,"E377")}),-1.0]])]});
            var Q24;
            Q24=makeQuery(id+"F0.imprint","IMPRINT",FACE,{"disambiguationData":[TD([[makeQuery(id+"F0.imprint","IMPRINT",EDGE,{"derivedFrom":sQuery(id+"F0.wireOp",EDGE,"E476")}),-1.0]])]});
            var Q25;
            Q25=makeQuery(id+"F0.imprint","IMPRINT",FACE,{"disambiguationData":[TD([[makeQuery(id+"F0.imprint","IMPRINT",EDGE,{"derivedFrom":sQuery(id+"F0.wireOp",EDGE,"E545")}),-1.0]])]});
            var Q26;
            Q26=makeQuery(id+"F0.imprint","IMPRINT",FACE,{"disambiguationData":[TD([[makeQuery(id+"F0.imprint","IMPRINT",EDGE,{"derivedFrom":sQuery(id+"F0.wireOp",EDGE,"E579")}),-1.0]])]});
            var Q27;
            Q27=makeQuery(id+"F0.imprint","IMPRINT",FACE,{"disambiguationData":[TD([[makeQuery(id+"F0.imprint","IMPRINT",EDGE,{"derivedFrom":sQuery(id+"F0.wireOp",EDGE,"E623")}),-1.0]])]});
            var Q28;
            Q28=makeQuery(id+"F0.imprint","IMPRINT",FACE,{"disambiguationData":[TD([[makeQuery(id+"F0.imprint","IMPRINT",EDGE,{"derivedFrom":sQuery(id+"F0.wireOp",EDGE,"E644")}),-1.0]])]});
            var Q29;
            Q29=makeQuery(id+"F0.imprint","IMPRINT",FACE,{"disambiguationData":[TD([[makeQuery(id+"F0.imprint","IMPRINT",EDGE,{"derivedFrom":sQuery(id+"F0.wireOp",EDGE,"E693")}),-1.0]])]});
            var Q30;
            Q30=makeQuery(id+"F0.imprint","IMPRINT",FACE,{"disambiguationData":[TD([[makeQuery(id+"F0.imprint","IMPRINT",EDGE,{"derivedFrom":sQuery(id+"F0.wireOp",EDGE,"E762")}),-1.0]])]});
            var Q31;
            Q31=makeQuery(id+"F0.imprint","IMPRINT",FACE,{"disambiguationData":[TD([[makeQuery(id+"F0.imprint","IMPRINT",EDGE,{"derivedFrom":sQuery(id+"F0.wireOp",EDGE,"E137")}),-1.0]])]});
            var Q32;
            Q32=makeQuery(id+"F0.imprint","IMPRINT",FACE,{"disambiguationData":[TD([[makeQuery(id+"F0.imprint","IMPRINT",EDGE,{"derivedFrom":sQuery(id+"F0.wireOp",EDGE,"E844")}),-1.0]])]});
            var Q33;
            Q33=makeQuery(id+"F0.imprint","IMPRINT",FACE,{"disambiguationData":[TD([[makeQuery(id+"F0.imprint","IMPRINT",EDGE,{"derivedFrom":sQuery(id+"F0.wireOp",EDGE,"E879")}),-1.0]])]});
            var Q34;
            Q34=makeQuery(id+"F0.imprint","IMPRINT",FACE,{"disambiguationData":[TD([[makeQuery(id+"F0.imprint","IMPRINT",EDGE,{"derivedFrom":sQuery(id+"F0.wireOp",EDGE,"E939")}),-1.0]])]});
            var Q35;
            Q35=makeQuery(id+"F0.imprint","IMPRINT",FACE,{"disambiguationData":[TD([[makeQuery(id+"F0.imprint","IMPRINT",EDGE,{"derivedFrom":sQuery(id+"F0.wireOp",EDGE,"E1044")}),-1.0]])]});
            var Q36;
            Q36=makeQuery(id+"F0.imprint","IMPRINT",FACE,{"disambiguationData":[TD([[makeQuery(id+"F0.imprint","IMPRINT",EDGE,{"derivedFrom":sQuery(id+"F0.wireOp",EDGE,"E1187")}),-1.0]])]});
            var Q37;
            Q37=makeQuery(id+"F0.imprint","IMPRINT",FACE,{"disambiguationData":[TD([[makeQuery(id+"F0.imprint","IMPRINT",EDGE,{"derivedFrom":sQuery(id+"F0.wireOp",EDGE,"E1136")}),-1.0]])]});
            var Q38;
            Q38=makeQuery(id+"F0.imprint","IMPRINT",FACE,{"disambiguationData":[TD([[makeQuery(id+"F0.imprint","IMPRINT",EDGE,{"derivedFrom":sQuery(id+"F0.wireOp",EDGE,"E1097")}),-1.0]])]});
            var Q39;
            Q39=makeQuery(id+"F0.imprint","IMPRINT",FACE,{"disambiguationData":[TD([[makeQuery(id+"F0.imprint","IMPRINT",EDGE,{"derivedFrom":sQuery(id+"F0.wireOp",EDGE,"E1040")}),-1.0]])]});
            var Q40;
            Q40=makeQuery(id+"F0.imprint","IMPRINT",FACE,{"disambiguationData":[TD([[makeQuery(id+"F0.imprint","IMPRINT",EDGE,{"derivedFrom":sQuery(id+"F0.wireOp",EDGE,"E971")}),-1.0]])]});
            var Q41;
            Q41=makeQuery(id+"F0.imprint","IMPRINT",FACE,{"disambiguationData":[TD([[makeQuery(id+"F0.imprint","IMPRINT",EDGE,{"derivedFrom":sQuery(id+"F0.wireOp",EDGE,"E911")}),-1.0]])]});
            var Q42;
            Q42=makeQuery(id+"F0.imprint","IMPRINT",FACE,{"disambiguationData":[TD([[makeQuery(id+"F0.imprint","IMPRINT",EDGE,{"derivedFrom":sQuery(id+"F0.wireOp",EDGE,"E851")}),-1.0]])]});
            var Q43;
            Q43=makeQuery(id+"F0.imprint","IMPRINT",FACE,{"disambiguationData":[TD([[makeQuery(id+"F0.imprint","IMPRINT",EDGE,{"derivedFrom":sQuery(id+"F0.wireOp",EDGE,"E823")}),-1.0]])]});
            var Q44;
            Q44=makeQuery(id+"F0.imprint","IMPRINT",FACE,{"disambiguationData":[TD([[makeQuery(id+"F0.imprint","IMPRINT",EDGE,{"derivedFrom":sQuery(id+"F0.wireOp",EDGE,"E815")}),-1.0]])]});
            var Q45;
            Q45=makeQuery(id+"F0.imprint","IMPRINT",FACE,{"disambiguationData":[TD([[makeQuery(id+"F0.imprint","IMPRINT",EDGE,{"derivedFrom":sQuery(id+"F0.wireOp",EDGE,"E714")}),-1.0]])]});
            var Q46;
            Q46=makeQuery(id+"F0.imprint","IMPRINT",FACE,{"disambiguationData":[TD([[makeQuery(id+"F0.imprint","IMPRINT",EDGE,{"derivedFrom":sQuery(id+"F0.wireOp",EDGE,"E689")}),-1.0]])]});
            var Q47;
            Q47=makeQuery(id+"F0.imprint","IMPRINT",FACE,{"disambiguationData":[TD([[makeQuery(id+"F0.imprint","IMPRINT",EDGE,{"derivedFrom":sQuery(id+"F0.wireOp",EDGE,"E685")}),-1.0]])]});
            var Q48;
            Q48=makeQuery(id+"F0.imprint","IMPRINT",FACE,{"disambiguationData":[TD([[makeQuery(id+"F0.imprint","IMPRINT",EDGE,{"derivedFrom":sQuery(id+"F0.wireOp",EDGE,"E627")}),-1.0]])]});
            var Q49;
            Q49=makeQuery(id+"F0.imprint","IMPRINT",FACE,{"disambiguationData":[TD([[makeQuery(id+"F0.imprint","IMPRINT",EDGE,{"derivedFrom":sQuery(id+"F0.wireOp",EDGE,"E611")}),-1.0]])]});
            var Q50;
            Q50=makeQuery(id+"F0.imprint","IMPRINT",FACE,{"disambiguationData":[TD([[makeQuery(id+"F0.imprint","IMPRINT",EDGE,{"derivedFrom":sQuery(id+"F0.wireOp",EDGE,"E563")}),-1.0]])]});
            var Q51;
            Q51=makeQuery(id+"F0.imprint","IMPRINT",FACE,{"disambiguationData":[TD([[makeQuery(id+"F0.imprint","IMPRINT",EDGE,{"derivedFrom":sQuery(id+"F0.wireOp",EDGE,"E497")}),-1.0]])]});
            extrude(context, id + "F2", {"entities" : qUnion([Q0, Q1, Q2, Q3, Q4, Q5, Q6, Q7, Q8, Q9, Q10, Q11, Q12, Q13, Q14, Q15, Q16, Q17, Q18, Q19, Q20, Q21, Q22, Q23, Q24, Q25, Q26, Q27, Q28, Q29, Q30, Q31, Q32, Q33, Q34, Q35, Q36, Q37, Q38, Q39, Q40, Q41, Q42, Q43, Q44, Q45, Q46, Q47, Q48, Q49, Q50, Q51]), "operationType" : NewBodyOperationType.ADD, "oppositeDirection" : true, "depth" : 0.8 * mm, "offsetDistance" : 25.4 * mm});
        }
    });
